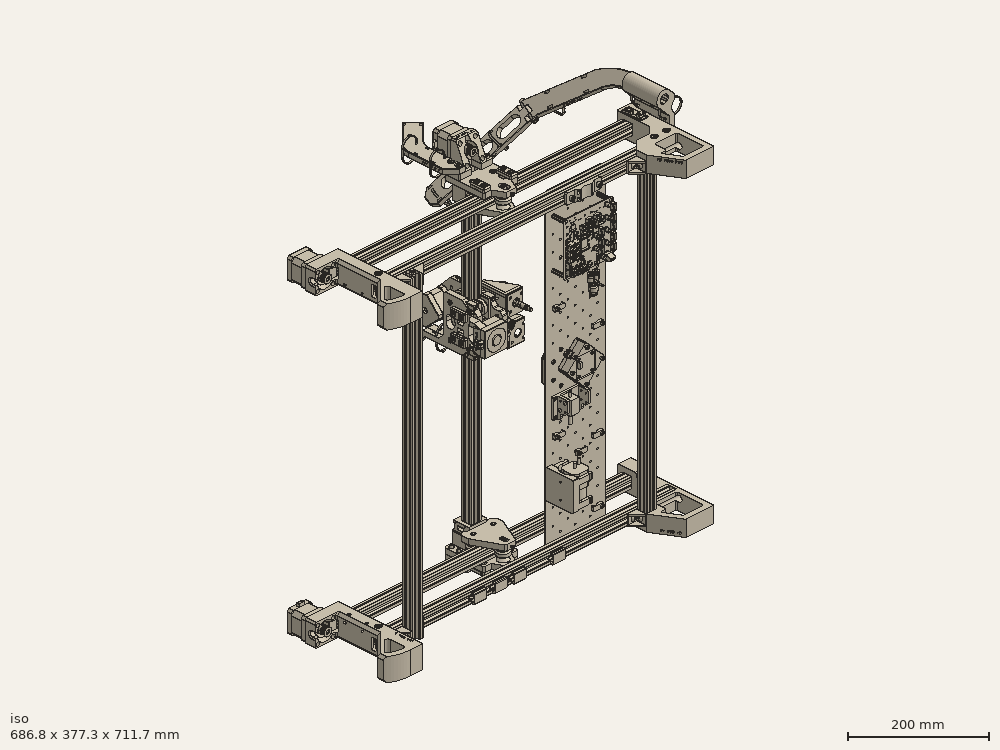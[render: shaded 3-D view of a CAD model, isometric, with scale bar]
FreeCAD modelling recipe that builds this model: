
FCSTD DOCUMENT  (FreeCAD 0.19R24291 (Git))
Label: assembly
Comment: LumenPnP
License: All rights reserved
LicenseURL: http://en.wikipedia.org/wiki/All_rights_reserved
objects: Part::FeaturePython×410, App::DocumentObjectGroup×16, Spreadsheet::Sheet×2
note: 410 computed .brp shape members not serialized (recipe doc carries the construction recipe); baked Part::Feature solids carry a one-line shape summary decoded from their .brp

FEATURE [Part::FeaturePython] b_MakerBot_LimitSwitchBoard1_001_001  label="MakerBot LimitSwitchBoard1_MakerBot LimitSwitchBoard_002"  # a2plus imported part (geometry in sourceFile) (typed FeaturePython)
  Placement = pos=(-192.209,155.993,-27.8326) rot=(0,0,-1;1.5708rad)
  Visibility1 = true
  a2p_Version = V0.1
  fixedPosition = false
  objectType = a2pPart
  sourceFile = ./OTS/OTS-0019_limit-switch-PCBA.STEP
  sourcePart = MakerBot LimitSwitchBoard
  subassemblyImport = false
  timeLastImport = 1.64563e+09
  updateColors = true
FEATURE [Part::FeaturePython] b_FDM_0005_y_gantry_001_  label="FDM-0005_y-gantry_Body_001"  # a2plus imported part (geometry in sourceFile) (typed FeaturePython)
  Placement = pos=(-209.128,133.935,11.9352) rot=(0,1,0;3.14159rad)
  Visibility1 = true
  a2p_Version = V0.1
  fixedPosition = false
  objectType = a2pPart
  sourceFile = ./FDM/FDM-0005_y-gantry.FCStd
  sourcePart = Body
  subassemblyImport = false
  timeLastImport = 1.64563e+09
  updateColors = true
FEATURE [Part::FeaturePython] b_OTS_0009_20x20_v_slot_600mm1_001_003  label="OTS-0009_20x20_v_slot_600mm1_20x20_v_slot_600mm v2_004"  # a2plus imported part (geometry in sourceFile) (typed FeaturePython)
  Placement = pos=(-219.183,133.936,0.0573608) rot=(0,0,1;0rad)
  Visibility1 = true
  a2p_Version = V0.1
  fixedPosition = false
  objectType = a2pPart
  sourceFile = ./OTS/OTS-0010_20x20-v-slot-600mm.step
  sourcePart = 20x20_v_slot_600mm v2
  subassemblyImport = false
  timeLastImport = 1.64563e+09
  updateColors = true
FEATURE [Part::FeaturePython] b_FDM_0005_y_gantry_001_001  label="FDM-0005_y-gantry_Body_002"  # a2plus imported part (geometry in sourceFile) (typed FeaturePython)
  Placement = pos=(-209.114,134.019,-612.218) rot=(0,0,1;0rad)
  Visibility1 = true
  a2p_Version = V0.1
  fixedPosition = false
  objectType = a2pPart
  sourceFile = ./FDM/FDM-0005_y-gantry.FCStd
  sourcePart = Body
  subassemblyImport = false
  timeLastImport = 1.64563e+09
  updateColors = true
FEATURE [Part::FeaturePython] b_FDM_0006_x_motor_mount_001_  label="FDM-0006_x-motor-mount_Body_001"  # a2plus imported part (geometry in sourceFile) (typed FeaturePython)
  Placement = pos=(-209.153,133.985,21.9455) rot=(0,1,0;3.14159rad)
  Visibility1 = true
  a2p_Version = V0.1
  fixedPosition = false
  objectType = a2pPart
  sourceFile = ./FDM/FDM-0006_x-motor-mount.FCStd
  sourcePart = Body
  subassemblyImport = false
  timeLastImport = 1.64668e+09
  updateColors = true
FEATURE [Part::FeaturePython] b_FDM_0013_x_idler_mount_001_  label="FDM-0013_x-idler-mount_Body_001"  # a2plus imported part (geometry in sourceFile) (typed FeaturePython)
  Placement = pos=(-209.106,124.037,-622.237) rot=(0,0,1;0rad)
  Visibility1 = true
  a2p_Version = V0.1
  fixedPosition = false
  objectType = a2pPart
  sourceFile = ./FDM/FDM-0013_x-idler-mount.FCStd
  sourcePart = Body
  subassemblyImport = false
  timeLastImport = 1.64563e+09
  updateColors = true
FEATURE [Part::FeaturePython] b_FDM_0010_y_gantry_umbilical_mount_001_  label="FDM-0010_y-gantry-umbilical-mount_Body_001"  # a2plus imported part (geometry in sourceFile) (typed FeaturePython)
  Placement = pos=(-260.596,133.978,22.038) rot=(0,0.707107,0.707107;3.14159rad)
  Visibility1 = true
  a2p_Version = V0.1
  fixedPosition = false
  objectType = a2pPart
  sourceFile = ./FDM/FDM-0010_y-gantry-umbilical-mount.FCStd
  sourcePart = Body
  subassemblyImport = false
  timeLastImport = 1.64563e+09
  updateColors = true
FEATURE [Part::FeaturePython] b_FDM_0008_y_gantry_support_001_  label="FDM-0008_y-gantry-support_Body_001"  # a2plus imported part (geometry in sourceFile) (typed FeaturePython)
  Placement = pos=(-209.134,74.2154,-32.0603) rot=(0,0,1;0rad)
  Visibility1 = true
  a2p_Version = V0.1
  fixedPosition = false
  objectType = a2pPart
  sourceFile = ./FDM/FDM-0008_y-gantry-support.FCStd
  sourcePart = Body
  subassemblyImport = false
  timeLastImport = 1.64563e+09
  updateColors = true
FEATURE [Part::FeaturePython] b_FDM_0008_y_gantry_support_001_001  label="FDM-0008_y-gantry-support_Body_002"  # a2plus imported part (geometry in sourceFile) (typed FeaturePython)
  Placement = pos=(-209.119,74.2225,-568.145) rot=(0,1,0;3.14159rad)
  Visibility1 = true
  a2p_Version = V0.1
  fixedPosition = false
  objectType = a2pPart
  sourceFile = ./FDM/FDM-0008_y-gantry-support.FCStd
  sourcePart = Body
  subassemblyImport = false
  timeLastImport = 1.64563e+09
  updateColors = true
FEATURE [Part::FeaturePython] b_FDM_0009_roller_spacer_001_  label="FDM-0009_roller-spacer_Body_001"  # a2plus imported part (geometry in sourceFile) (typed FeaturePython)
  Placement = pos=(-209.128,80.348,-22.0728) rot=(1,0,0;1.5708rad)
  Visibility1 = true
  a2p_Version = V0.1
  fixedPosition = false
  objectType = a2pPart
  sourceFile = ./FDM/FDM-0009_roller-spacer.FCStd
  sourcePart = Body
  subassemblyImport = false
  timeLastImport = 1.64563e+09
  updateColors = true
FEATURE [Part::FeaturePython] b_v_slot_roller1_001_  label="v-slot-roller1_Fusion_001"  # a2plus imported part (geometry in sourceFile) (typed FeaturePython)
  Placement = pos=(-213.864,116.699,-10.7746) rot=(-1,0,0;1.5708rad)
  Visibility1 = true
  a2p_Version = V0.1
  fixedPosition = false
  objectType = a2pPart
  sourceFile = ./OTS/OTS-0011_v-slot-roller.step
  sourcePart = Fusion
  subassemblyImport = false
  timeLastImport = 1.64563e+09
  updateColors = true
FEATURE [Part::FeaturePython] b_v_slot_roller1_001_001  label="v-slot-roller1_Fusion_002"  # a2plus imported part (geometry in sourceFile) (typed FeaturePython)
  Placement = pos=(-173.877,116.658,-10.7212) rot=(-1,0,0;1.5708rad)
  Visibility1 = true
  a2p_Version = V0.1
  fixedPosition = false
  objectType = a2pPart
  sourceFile = ./OTS/OTS-0011_v-slot-roller.step
  sourcePart = Fusion
  subassemblyImport = false
  timeLastImport = 1.64563e+09
  updateColors = true
FEATURE [Part::FeaturePython] b_FDM_0009_roller_spacer_001_001  label="FDM-0009_roller-spacer_Body_002"  # a2plus imported part (geometry in sourceFile) (typed FeaturePython)
  Placement = pos=(-209.167,80.3524,1.94462) rot=(-1,0,0;1.5708rad)
  Visibility1 = true
  a2p_Version = V0.1
  fixedPosition = false
  objectType = a2pPart
  sourceFile = ./FDM/FDM-0009_roller-spacer.FCStd
  sourcePart = Body
  subassemblyImport = false
  timeLastImport = 1.64563e+09
  updateColors = true
FEATURE [Part::FeaturePython] b_v_slot_roller1_001_002  label="v-slot-roller1_Fusion_003"  # a2plus imported part (geometry in sourceFile) (typed FeaturePython)
  Placement = pos=(-193.862,77.3523,-10.791) rot=(-1,0,0;1.5708rad)
  Visibility1 = true
  a2p_Version = V0.1
  fixedPosition = false
  objectType = a2pPart
  sourceFile = ./OTS/OTS-0011_v-slot-roller.step
  sourcePart = Fusion
  subassemblyImport = false
  timeLastImport = 1.64563e+09
  updateColors = true
FEATURE [Part::FeaturePython] Screw003  label="M5x40-Screw"  # Fasteners workbench fastener (typed FeaturePython)
  Placement = pos=(-189.16,119.74,6.95) rot=(0,0,1;0rad)
  Visibility1 = true
  diameter = 6
  invert = false
  length = 12
  lengthCustom = 40
  matchOuter = false
  offset = 0
  thread = false
  type = 33
FEATURE [Part::FeaturePython] Screw004  label="M5x40-Screw291"  # Fasteners workbench fastener (typed FeaturePython)
  Placement = pos=(-229.11,119.74,6.95) rot=(0,0,1;0rad)
  Visibility1 = true
  diameter = 6
  invert = false
  length = 12
  lengthCustom = 40
  matchOuter = false
  offset = 0
  thread = false
  type = 33
FEATURE [Part::FeaturePython] Screw005  label="M5x40-Screw292"  # Fasteners workbench fastener (typed FeaturePython)
  Placement = pos=(-209.15,80.34,6.95) rot=(0,0,1;0rad)
  Visibility1 = true
  diameter = 6
  invert = false
  length = 12
  lengthCustom = 40
  matchOuter = false
  offset = 0
  thread = false
  type = 33
FEATURE [Part::FeaturePython] Nut003  label="M5-Nut"  # Fasteners workbench fastener (typed FeaturePython)
  Placement = pos=(-229.05,119.689,-28.1459) rot=(-0.258819,0.965926,0;3.14159rad)
  Visibility1 = true
  diameter = 7
  invert = false
  matchOuter = false
  offset = 0
  thread = false
  type = 7
FEATURE [Part::FeaturePython] Nut004  label="M5-Nut208"  # Fasteners workbench fastener (typed FeaturePython)
  Placement = pos=(-189.008,119.713,-28.1459) rot=(-0.258819,0.965926,0;3.14159rad)
  Visibility1 = true
  diameter = 7
  invert = false
  matchOuter = false
  offset = 0
  thread = false
  type = 7
FEATURE [Part::FeaturePython] Nut005  label="M5-Nut209"  # Fasteners workbench fastener (typed FeaturePython)
  Placement = pos=(-209.108,80.3492,-28.1459) rot=(-0.258819,0.965926,0;3.14159rad)
  Visibility1 = true
  diameter = 7
  invert = false
  matchOuter = false
  offset = 0
  thread = false
  type = 7
FEATURE [Part::FeaturePython] Screw006  label="M3x16-Screw"  # Fasteners workbench fastener (typed FeaturePython)
  Placement = pos=(-209.15,61.89,-26.03) rot=(1,0,0;1.5708rad)
  Visibility1 = true
  diameter = 4
  invert = false
  length = 6
  lengthCustom = 16
  matchOuter = false
  offset = 0
  thread = false
  type = 33
FEATURE [Part::FeaturePython] Screw007  label="M3x16-Screw036"  # Fasteners workbench fastener (typed FeaturePython)
  Placement = pos=(-209.15,61.89,5.93) rot=(1,0,0;1.5708rad)
  Visibility1 = true
  diameter = 4
  invert = false
  length = 6
  lengthCustom = 16
  matchOuter = false
  offset = 0
  thread = false
  type = 33
FEATURE [Part::FeaturePython] Nut006  label="M3-Nut"  # Fasteners workbench fastener (typed FeaturePython)
  Placement = pos=(-209.156,68.38,5.75438) rot=(0.935113,-0.250563,0.250563;1.63783rad)
  Visibility1 = true
  diameter = 4
  invert = false
  matchOuter = false
  offset = 0
  thread = false
  type = 7
FEATURE [Part::FeaturePython] Nut007  label="M3-Nut178"  # Fasteners workbench fastener (typed FeaturePython)
  Placement = pos=(-209.069,68.45,-26.1349) rot=(0.935113,-0.250563,0.250563;1.63783rad)
  Visibility1 = true
  diameter = 4
  invert = false
  matchOuter = false
  offset = 0
  thread = false
  type = 7
FEATURE [Part::FeaturePython] Nut008  label="M5-Nut210"  # Fasteners workbench fastener (typed FeaturePython)
  Placement = pos=(-181.652,141.373,6.70406) rot=(-0.258819,0.965926,0;3.14159rad)
  Visibility1 = true
  diameter = 7
  invert = false
  matchOuter = false
  offset = 0
  thread = false
  type = 7
FEATURE [Part::FeaturePython] Nut009  label="M5-Nut211"  # Fasteners workbench fastener (typed FeaturePython)
  Placement = pos=(-181.604,156.47,6.70406) rot=(-0.258819,0.965926,0;3.14159rad)
  Visibility1 = true
  diameter = 7
  invert = false
  matchOuter = false
  offset = 0
  thread = false
  type = 7
FEATURE [Part::FeaturePython] Nut010  label="M5-Nut212"  # Fasteners workbench fastener (typed FeaturePython)
  Placement = pos=(-236.604,156.412,6.70406) rot=(-0.258819,0.965926,0;3.14159rad)
  Visibility1 = true
  diameter = 7
  invert = false
  matchOuter = false
  offset = 0
  thread = false
  type = 7
FEATURE [Part::FeaturePython] Nut011  label="M5-Nut213"  # Fasteners workbench fastener (typed FeaturePython)
  Placement = pos=(-236.631,141.42,6.70406) rot=(-0.258819,0.965926,0;3.14159rad)
  Visibility1 = true
  diameter = 7
  invert = false
  matchOuter = false
  offset = 0
  thread = false
  type = 7
FEATURE [Part::FeaturePython] Screw008  label="M5x25-Screw"  # Fasteners workbench fastener (typed FeaturePython)
  Placement = pos=(-236.29,141.5,27.32) rot=(0,0,1;0rad)
  Visibility1 = true
  diameter = 6
  invert = false
  length = 6
  lengthCustom = 25
  matchOuter = false
  offset = 0
  thread = false
  type = 33
FEATURE [Part::FeaturePython] Screw009  label="M5x25-Screw068"  # Fasteners workbench fastener (typed FeaturePython)
  Placement = pos=(-181.43,141.29,22.2) rot=(0,0,1;0rad)
  Visibility1 = true
  diameter = 6
  invert = false
  length = 6
  lengthCustom = 25
  matchOuter = false
  offset = 0
  thread = false
  type = 33
FEATURE [Part::FeaturePython] Screw010  label="M5x25-Screw069"  # Fasteners workbench fastener (typed FeaturePython)
  Placement = pos=(-181.43,156.5,22.2) rot=(0,0,1;0rad)
  Visibility1 = true
  diameter = 6
  invert = false
  length = 6
  lengthCustom = 25
  matchOuter = false
  offset = 0
  thread = false
  type = 33
FEATURE [Part::FeaturePython] Screw011  label="M5x25-Screw070"  # Fasteners workbench fastener (typed FeaturePython)
  Placement = pos=(-236.29,156.25,27.32) rot=(0,0,1;0rad)
  Visibility1 = true
  diameter = 6
  invert = false
  length = 6
  lengthCustom = 25
  matchOuter = false
  offset = 0
  thread = false
  type = 33
FEATURE [Part::FeaturePython] Screw012  label="M5x25-Screw071"  # Fasteners workbench fastener (typed FeaturePython)
  Placement = pos=(-181.5,156.55,-622.24) rot=(0,1,0;3.14159rad)
  Visibility1 = true
  diameter = 6
  invert = false
  length = 6
  lengthCustom = 25
  matchOuter = false
  offset = 0
  thread = false
  type = 33
FEATURE [Part::FeaturePython] Screw013  label="M5x25-Screw072"  # Fasteners workbench fastener (typed FeaturePython)
  Placement = pos=(-181.5,141.61,-622.18) rot=(0,1,0;3.14159rad)
  Visibility1 = true
  diameter = 6
  invert = false
  length = 6
  lengthCustom = 25
  matchOuter = false
  offset = 0
  thread = false
  type = 33
FEATURE [Part::FeaturePython] Screw014  label="M5x25-Screw073"  # Fasteners workbench fastener (typed FeaturePython)
  Placement = pos=(-236.54,141.56,-622.22) rot=(0,1,0;3.14159rad)
  Visibility1 = true
  diameter = 6
  invert = false
  length = 6
  lengthCustom = 25
  matchOuter = false
  offset = 0
  thread = false
  type = 33
FEATURE [Part::FeaturePython] Screw015  label="M5x25-Screw074"  # Fasteners workbench fastener (typed FeaturePython)
  Placement = pos=(-236.54,156.5,-622.24) rot=(0,1,0;3.14159rad)
  Visibility1 = true
  diameter = 6
  invert = false
  length = 6
  lengthCustom = 25
  matchOuter = false
  offset = 0
  thread = false
  type = 33
FEATURE [Part::FeaturePython] Nut012  label="M5-Nut214"  # Fasteners workbench fastener (typed FeaturePython)
  Placement = pos=(-236.619,141.519,-603.606) rot=(-0.258819,0.965926,0;3.14159rad)
  Visibility1 = true
  diameter = 7
  invert = false
  matchOuter = false
  offset = 0
  thread = false
  type = 7
FEATURE [Part::FeaturePython] Nut013  label="M5-Nut215"  # Fasteners workbench fastener (typed FeaturePython)
  Placement = pos=(-236.602,156.529,-603.536) rot=(-0.258819,0.965926,0;3.14159rad)
  Visibility1 = true
  diameter = 7
  invert = false
  matchOuter = false
  offset = 0
  thread = false
  type = 7
FEATURE [Part::FeaturePython] Nut014  label="M5-Nut216"  # Fasteners workbench fastener (typed FeaturePython)
  Placement = pos=(-181.656,156.52,-603.666) rot=(-0.258819,0.965926,0;3.14159rad)
  Visibility1 = true
  diameter = 7
  invert = false
  matchOuter = false
  offset = 0
  thread = false
  type = 7
FEATURE [Part::FeaturePython] Nut015  label="M5-Nut217"  # Fasteners workbench fastener (typed FeaturePython)
  Placement = pos=(-181.56,141.553,-603.646) rot=(-0.258819,0.965926,0;3.14159rad)
  Visibility1 = true
  diameter = 7
  invert = false
  matchOuter = false
  offset = 0
  thread = false
  type = 7
FEATURE [Part::FeaturePython] Screw016  label="M5x40-Screw293"  # Fasteners workbench fastener (typed FeaturePython)
  Placement = pos=(-189.09,119.82,-607.25) rot=(0,1,0;3.14159rad)
  Visibility1 = true
  diameter = 6
  invert = false
  length = 12
  lengthCustom = 40
  matchOuter = false
  offset = 0
  thread = false
  type = 33
FEATURE [Part::FeaturePython] b_v_slot_roller1_001_006  label="v-slot-roller1_Fusion_007"  # a2plus imported part (geometry in sourceFile) (typed FeaturePython)
  Placement = pos=(-186.117,135.005,-590.83) rot=(0.57735,0.57735,-0.57735;4.18879rad)
  Visibility1 = true
  a2p_Version = V0.1
  fixedPosition = false
  objectType = a2pPart
  sourceFile = ./OTS/OTS-0011_v-slot-roller.step
  sourcePart = Fusion
  subassemblyImport = false
  timeLastImport = 1.64563e+09
  updateColors = true
FEATURE [Part::FeaturePython] b_v_slot_roller1_001_007  label="v-slot-roller1_Fusion_008"  # a2plus imported part (geometry in sourceFile) (typed FeaturePython)
  Placement = pos=(-213.81,116.722,-590.853) rot=(-1,0,0;1.5708rad)
  Visibility1 = true
  a2p_Version = V0.1
  fixedPosition = false
  objectType = a2pPart
  sourceFile = ./OTS/OTS-0011_v-slot-roller.step
  sourcePart = Fusion
  subassemblyImport = false
  timeLastImport = 1.64563e+09
  updateColors = true
FEATURE [Part::FeaturePython] Screw017  label="M5x40-Screw294"  # Fasteners workbench fastener (typed FeaturePython)
  Placement = pos=(-229.1,119.82,-607.25) rot=(0,1,0;3.14159rad)
  Visibility1 = true
  diameter = 6
  invert = false
  length = 12
  lengthCustom = 40
  matchOuter = false
  offset = 0
  thread = false
  type = 33
FEATURE [Part::FeaturePython] Screw018  label="M5x40-Screw295"  # Fasteners workbench fastener (typed FeaturePython)
  Placement = pos=(-209.12,80.38,-607.25) rot=(0,1,0;3.14159rad)
  Visibility1 = true
  diameter = 6
  invert = false
  length = 12
  lengthCustom = 40
  matchOuter = false
  offset = 0
  thread = false
  type = 33
FEATURE [Part::FeaturePython] b_v_slot_roller1_001_008  label="v-slot-roller1_Fusion_009"  # a2plus imported part (geometry in sourceFile) (typed FeaturePython)
  Placement = pos=(-193.81,77.3723,-590.853) rot=(-1,0,0;1.5708rad)
  Visibility1 = true
  a2p_Version = V0.1
  fixedPosition = false
  objectType = a2pPart
  sourceFile = ./OTS/OTS-0011_v-slot-roller.step
  sourcePart = Fusion
  subassemblyImport = false
  timeLastImport = 1.64563e+09
  updateColors = true
FEATURE [Part::FeaturePython] Nut016  label="M5-Nut218"  # Fasteners workbench fastener (typed FeaturePython)
  Placement = pos=(-209.08,80.4002,-568.626) rot=(-0.258819,0.965926,0;3.14159rad)
  Visibility1 = true
  diameter = 7
  invert = false
  matchOuter = false
  offset = 0
  thread = false
  type = 7
FEATURE [Part::FeaturePython] Nut017  label="M5-Nut219"  # Fasteners workbench fastener (typed FeaturePython)
  Placement = pos=(-189.034,119.779,-568.626) rot=(-0.258819,0.965926,0;3.14159rad)
  Visibility1 = true
  diameter = 7
  invert = false
  matchOuter = false
  offset = 0
  thread = false
  type = 7
FEATURE [Part::FeaturePython] Nut018  label="M5-Nut220"  # Fasteners workbench fastener (typed FeaturePython)
  Placement = pos=(-229.099,119.753,-568.626) rot=(-0.258819,0.965926,0;3.14159rad)
  Visibility1 = true
  diameter = 7
  invert = false
  matchOuter = false
  offset = 0
  thread = false
  type = 7
FEATURE [Part::FeaturePython] Screw019  label="M3x16-Screw037"  # Fasteners workbench fastener (typed FeaturePython)
  Placement = pos=(-209.15,61.89,-574.13) rot=(1,0,0;1.5708rad)
  Visibility1 = true
  diameter = 4
  invert = false
  length = 6
  lengthCustom = 16
  matchOuter = false
  offset = 0
  thread = false
  type = 33
FEATURE [Part::FeaturePython] Screw020  label="M3x16-Screw043"  # Fasteners workbench fastener (typed FeaturePython)
  Placement = pos=(-209.12,61.89,-605.22) rot=(1,0,0;1.5708rad)
  Visibility1 = true
  diameter = 4
  invert = false
  length = 6
  lengthCustom = 16
  matchOuter = false
  offset = 0
  thread = false
  type = 33
FEATURE [Part::FeaturePython] Nut019  label="M3-Nut179"  # Fasteners workbench fastener (typed FeaturePython)
  Placement = pos=(-209.236,68.44,-574.367) rot=(0.935113,-0.250563,0.250563;1.63783rad)
  Visibility1 = true
  diameter = 4
  invert = false
  matchOuter = false
  offset = 0
  thread = false
  type = 7
FEATURE [Part::FeaturePython] Nut020  label="M3-Nut232"  # Fasteners workbench fastener (typed FeaturePython)
  Placement = pos=(-209.133,68.46,-605.236) rot=(0.57735,-0.57735,0.57735;2.0944rad)
  Visibility1 = true
  diameter = 4
  invert = false
  matchOuter = false
  offset = 0
  thread = false
  type = 7
FEATURE [Part::FeaturePython] b_FDM_0009_roller_spacer_001_002  label="FDM-0009_roller-spacer_Body_003"  # a2plus imported part (geometry in sourceFile) (typed FeaturePython)
  Placement = pos=(-209.167,80.3524,-578.105) rot=(-1,0,0;1.5708rad)
  Visibility1 = true
  a2p_Version = V0.1
  fixedPosition = false
  objectType = a2pPart
  sourceFile = ./FDM/FDM-0009_roller-spacer.FCStd
  sourcePart = Body
  subassemblyImport = false
  timeLastImport = 1.64563e+09
  updateColors = true
FEATURE [Part::FeaturePython] b_FDM_0009_roller_spacer_001_003  label="FDM-0009_roller-spacer_Body_004"  # a2plus imported part (geometry in sourceFile) (typed FeaturePython)
  Placement = pos=(-209.167,80.3524,-602.155) rot=(0,0.707107,0.707107;3.14159rad)
  Visibility1 = true
  a2p_Version = V0.1
  fixedPosition = false
  objectType = a2pPart
  sourceFile = ./FDM/FDM-0009_roller-spacer.FCStd
  sourcePart = Body
  subassemblyImport = false
  timeLastImport = 1.64563e+09
  updateColors = true
FEATURE [Part::FeaturePython] Screw021  label="M5x40-Screw289"  # Fasteners workbench fastener (typed FeaturePython)
  Placement = pos=(-194.1,163.97,-634.23) rot=(0,0.707107,0.707107;3.14159rad)
  Visibility1 = true
  diameter = 6
  invert = false
  length = 12
  lengthCustom = 40
  matchOuter = false
  offset = 0
  thread = false
  type = 33
FEATURE [Part::FeaturePython] Screw022  label="M5x10-Screw"  # Fasteners workbench fastener (typed FeaturePython)
  Placement = pos=(-209.22,158.94,-18.1) rot=(-1,0,0;1.5708rad)
  Visibility1 = true
  diameter = 6
  invert = false
  length = 1
  lengthCustom = 10
  matchOuter = false
  offset = 0
  thread = false
  type = 33
FEATURE [Part::FeaturePython] b_M5_tslot_nut1_001_  label="M5-tslot-nut1_T_Slot_Nut_Dropin_M5 v1_001"  # a2plus imported part (geometry in sourceFile) (typed FeaturePython)
  Placement = pos=(-209.412,148.905,-18.0282) rot=(0.57735,-0.57735,-0.57735;4.18879rad)
  Visibility1 = true
  a2p_Version = V0.1
  fixedPosition = false
  objectType = a2pPart
  sourceFile = ./FST/FST-0016_M5-tslot-nut.step
  sourcePart = T_Slot_Nut_Dropin_M5 v1
  subassemblyImport = false
  timeLastImport = 1.64563e+09
  updateColors = true
FEATURE [Part::FeaturePython] b_M5_tslot_nut1_001_001  label="M5-tslot-nut1_T_Slot_Nut_Dropin_M5 v1_002"  # a2plus imported part (geometry in sourceFile) (typed FeaturePython)
  Placement = pos=(-209.412,148.905,-582.128) rot=(0.57735,-0.57735,-0.57735;4.18879rad)
  Visibility1 = true
  a2p_Version = V0.1
  fixedPosition = false
  objectType = a2pPart
  sourceFile = ./FST/FST-0016_M5-tslot-nut.step
  sourcePart = T_Slot_Nut_Dropin_M5 v1
  subassemblyImport = false
  timeLastImport = 1.64563e+09
  updateColors = true
FEATURE [Part::FeaturePython] Screw023  label="M5x10-Screw187"  # Fasteners workbench fastener (typed FeaturePython)
  Placement = pos=(-209.22,158.94,-582.17) rot=(-1,0,0;1.5708rad)
  Visibility1 = true
  diameter = 6
  invert = false
  length = 1
  lengthCustom = 10
  matchOuter = false
  offset = 0
  thread = false
  type = 33
FEATURE [Part::FeaturePython] Screw025  label="M5x10-Screw188"  # Fasteners workbench fastener (typed FeaturePython)
  Placement = pos=(-236.1,91.45,15.24) rot=(0,0,1;0rad)
  Visibility1 = true
  diameter = 6
  invert = false
  length = 1
  lengthCustom = 10
  matchOuter = false
  offset = 0
  thread = false
  type = 33
FEATURE [Part::FeaturePython] b_FDM_0027_belt_clamp_001_  label="FDM-0027_belt-clamp_Body_001"  # a2plus imported part (geometry in sourceFile) (typed FeaturePython)
  Placement = pos=(-236.126,98.9408,12.0481) rot=(0,0,1;0rad)
  Visibility1 = true
  a2p_Version = V0.1
  fixedPosition = false
  objectType = a2pPart
  sourceFile = ./FDM/FDM-0027_belt-clamp.FCStd
  sourcePart = Body
  subassemblyImport = false
  timeLastImport = 1.64563e+09
  updateColors = true
FEATURE [Part::FeaturePython] Screw026  label="M5x10-Screw189"  # Fasteners workbench fastener (typed FeaturePython)
  Placement = pos=(-236.1,106.47,15.24) rot=(0,0,1;0rad)
  Visibility1 = true
  diameter = 6
  invert = false
  length = 1
  lengthCustom = 10
  matchOuter = false
  offset = 0
  thread = false
  type = 33
FEATURE [Part::FeaturePython] Screw027  label="M5x10-Screw190"  # Fasteners workbench fastener (typed FeaturePython)
  Placement = pos=(-182.19,106.47,15.24) rot=(0,0,1;0rad)
  Visibility1 = true
  diameter = 6
  invert = false
  length = 1
  lengthCustom = 10
  matchOuter = false
  offset = 0
  thread = false
  type = 33
FEATURE [Part::FeaturePython] Screw028  label="M5x10-Screw191"  # Fasteners workbench fastener (typed FeaturePython)
  Placement = pos=(-182.19,91.5,15.24) rot=(0,0,1;0rad)
  Visibility1 = true
  diameter = 6
  invert = false
  length = 1
  lengthCustom = 10
  matchOuter = false
  offset = 0
  thread = false
  type = 33
FEATURE [Part::FeaturePython] b_FDM_0027_belt_clamp_001_001  label="FDM-0027_belt-clamp_Body_002"  # a2plus imported part (geometry in sourceFile) (typed FeaturePython)
  Placement = pos=(-182.176,98.9408,12.0481) rot=(0,0,1;0rad)
  Visibility1 = true
  a2p_Version = V0.1
  fixedPosition = false
  objectType = a2pPart
  sourceFile = ./FDM/FDM-0027_belt-clamp.FCStd
  sourcePart = Body
  subassemblyImport = false
  timeLastImport = 1.64563e+09
  updateColors = true
FEATURE [Part::FeaturePython] Screw121  label="M3x8-Screw"  # Fasteners workbench fastener (typed FeaturePython)
  Placement = pos=(-190.65,158.35,-32.97) rot=(0,1,0;1.5708rad)
  Visibility1 = true
  diameter = 1
  invert = false
  length = 1
  lengthCustom = 8
  matchOuter = false
  offset = 0
  thread = false
  type = 39
FEATURE [Part::FeaturePython] Screw122  label="M3x8-Screw273"  # Fasteners workbench fastener (typed FeaturePython)
  Placement = pos=(-190.65,139.49,-33.02) rot=(0,1,0;1.5708rad)
  Visibility1 = true
  diameter = 1
  invert = false
  length = 1
  lengthCustom = 8
  matchOuter = false
  offset = 0
  thread = false
  type = 39
FEATURE [Part::FeaturePython] Screw099  label="M3x8-Screw278"  # Fasteners workbench fastener (typed FeaturePython)
  Placement = pos=(-224.63,158.88,58.97) rot=(0.57735,0.57735,-0.57735;2.0944rad)
  Visibility1 = true
  diameter = 1
  invert = false
  length = 1
  lengthCustom = 8
  matchOuter = false
  offset = 0
  thread = false
  type = 39
FEATURE [Part::FeaturePython] Screw097  label="M3x8-Screw279"  # Fasteners workbench fastener (typed FeaturePython)
  Placement = pos=(-224.63,158.88,27.96) rot=(0.57735,0.57735,-0.57735;2.0944rad)
  Visibility1 = true
  diameter = 1
  invert = false
  length = 1
  lengthCustom = 8
  matchOuter = false
  offset = 0
  thread = false
  type = 39
FEATURE [Part::FeaturePython] Screw100  label="M3x8-Screw280"  # Fasteners workbench fastener (typed FeaturePython)
  Placement = pos=(-193.61,158.88,58.97) rot=(0.57735,0.57735,-0.57735;2.0944rad)
  Visibility1 = true
  diameter = 1
  invert = false
  length = 1
  lengthCustom = 8
  matchOuter = false
  offset = 0
  thread = false
  type = 39
FEATURE [Part::FeaturePython] Screw098  label="M3x8-Screw281"  # Fasteners workbench fastener (typed FeaturePython)
  Placement = pos=(-193.61,158.88,27.96) rot=(0.57735,0.57735,-0.57735;2.0944rad)
  Visibility1 = true
  diameter = 1
  invert = false
  length = 1
  lengthCustom = 8
  matchOuter = false
  offset = 0
  thread = false
  type = 39
FEATURE [Part::FeaturePython] Screw059  label="M5x25-Screw075"  # Fasteners workbench fastener (typed FeaturePython)
  Placement = pos=(-209.27,154.08,-634.17) rot=(0,0.707107,0.707107;3.14159rad)
  Visibility1 = true
  diameter = 6
  invert = false
  length = 6
  lengthCustom = 25
  matchOuter = false
  offset = 0
  thread = false
  type = 33
FEATURE [Part::FeaturePython] b_front_leg_tensioner_001_001  label="front-leg-tensioner_Body_002"  # a2plus imported part (geometry in sourceFile) (typed FeaturePython)
  Placement = pos=(-189.226,134.067,-629.163) rot=(0,1,0;3.14159rad)
  Visibility1 = true
  a2p_Version = V0.1
  fixedPosition = false
  objectType = a2pPart
  sourceFile = ./FDM/FDM-0037_belt-tension-arm.FCStd
  sourcePart = Body
  subassemblyImport = false
  timeLastImport = 1.64563e+09
  updateColors = true
FEATURE [Part::FeaturePython] Screw060  label="M3x16-Screw039"  # Fasteners workbench fastener (typed FeaturePython)
  Placement = pos=(-224.21,144.08,-638.25) rot=(1,0,0;3.14159rad)
  Visibility1 = true
  diameter = 4
  invert = false
  length = 6
  lengthCustom = 16
  matchOuter = false
  offset = 0
  thread = false
  type = 33
FEATURE [Part::FeaturePython] Screw058  label="M5x10-Screw192"  # Fasteners workbench fastener (typed FeaturePython)
  Placement = pos=(-236.11,106.53,-615.37) rot=(0,1,0;3.14159rad)
  Visibility1 = true
  diameter = 6
  invert = false
  length = 1
  lengthCustom = 10
  matchOuter = false
  offset = 0
  thread = false
  type = 33
FEATURE [Part::FeaturePython] Screw057  label="M5x10-Screw193"  # Fasteners workbench fastener (typed FeaturePython)
  Placement = pos=(-236.11,91.54,-615.37) rot=(0,1,0;3.14159rad)
  Visibility1 = true
  diameter = 6
  invert = false
  length = 1
  lengthCustom = 10
  matchOuter = false
  offset = 0
  thread = false
  type = 33
FEATURE [Part::FeaturePython] Screw056  label="M5x10-Screw194"  # Fasteners workbench fastener (typed FeaturePython)
  Placement = pos=(-182.19,91.54,-615.37) rot=(0,1,0;3.14159rad)
  Visibility1 = true
  diameter = 6
  invert = false
  length = 1
  lengthCustom = 10
  matchOuter = false
  offset = 0
  thread = false
  type = 33
FEATURE [Part::FeaturePython] b_FDM_0027_belt_clamp_001_005  label="FDM-0027_belt-clamp_Body_006"  # a2plus imported part (geometry in sourceFile) (typed FeaturePython)
  Placement = pos=(-182.156,98.9408,-612.402) rot=(0,1,0;3.14159rad)
  Visibility1 = true
  a2p_Version = V0.1
  fixedPosition = false
  objectType = a2pPart
  sourceFile = ./FDM/FDM-0027_belt-clamp.FCStd
  sourcePart = Body
  subassemblyImport = false
  timeLastImport = 1.64563e+09
  updateColors = true
FEATURE [Part::FeaturePython] b_FDM_0027_belt_clamp_001_004  label="FDM-0027_belt-clamp_Body_005"  # a2plus imported part (geometry in sourceFile) (typed FeaturePython)
  Placement = pos=(-236.126,99.0108,-612.402) rot=(0,1,0;3.14159rad)
  Visibility1 = true
  a2p_Version = V0.1
  fixedPosition = false
  objectType = a2pPart
  sourceFile = ./FDM/FDM-0027_belt-clamp.FCStd
  sourcePart = Body
  subassemblyImport = false
  timeLastImport = 1.64563e+09
  updateColors = true
FEATURE [Part::FeaturePython] b_Nema_17_42A02C_v21_001_001  label="Nema 17 42A02C v21_ Nema 17 42A02C v2_002"  # a2plus imported part (geometry in sourceFile) (typed FeaturePython)
  Placement = pos=(-209.138,153.958,43.4338) rot=(0.57735,0.57735,-0.57735;2.0944rad)
  Visibility1 = true
  a2p_Version = V0.1
  fixedPosition = false
  objectType = a2pPart
  sourceFile = ./OTS/OTS-0012_nema17-stepper.step
  sourcePart =  Nema 17 42A02C v2
  subassemblyImport = false
  timeLastImport = 1.64563e+09
  updateColors = true
FEATURE [Part::FeaturePython] Nut043  label="M5-Nut472"  # Fasteners workbench fastener (typed FeaturePython)
  Placement = pos=(-209.269,134.219,-634.166) rot=(1,0,0;1.5708rad)
  Visibility1 = true
  diameter = 3
  invert = false
  matchOuter = false
  offset = 0
  thread = false
  type = 5
FEATURE [Part::FeaturePython] Nut042  label="M5-Nut471"  # Fasteners workbench fastener (typed FeaturePython)
  Placement = pos=(-194.15,128.957,-634.224) rot=(-0.186157,-0.694747,0.694747;3.50969rad)
  Visibility1 = true
  diameter = 3
  invert = false
  matchOuter = false
  offset = 0
  thread = false
  type = 5
FEATURE [Part::FeaturePython] b_Gates_2GT_20T_Toothed_Pulley1_001_001  label="Gates_2GT_20T_Toothed_Pulley1_Gates_2GT_20T_Toothed_Pulley_002"  # a2plus imported part (geometry in sourceFile) (typed FeaturePython)
  Placement = pos=(-209.139,155.221,43.4196) rot=(0,0,1;3.14159rad)
  Visibility1 = true
  a2p_Version = V0.1
  fixedPosition = false
  objectType = a2pPart
  sourceFile = ./OTS/OTS-0017_GT2-20-tooth-pulley.STEP
  sourcePart = Gates_2GT_20T_Toothed_Pulley
  subassemblyImport = false
  timeLastImport = 1.64563e+09
  updateColors = true
FEATURE [Part::FeaturePython] b_Gates_2GT_20T_Toothed_Idler1_001_002  label="Gates_2GT_20T_Toothed_Idler1_Gates_2GT_20T_Toothed_Idler_003"  # a2plus imported part (geometry in sourceFile) (typed FeaturePython)
  Placement = pos=(-209.286,138.99,-634.179) rot=(0,0,1;0rad)
  Visibility1 = true
  a2p_Version = V0.1
  fixedPosition = false
  objectType = a2pPart
  sourceFile = ./OTS/OTS-0016_GT2-20-tooth-idler.STEP
  sourcePart = Gates_2GT_20T_Toothed_Idler
  subassemblyImport = false
  timeLastImport = 1.64563e+09
  updateColors = true
FEATURE [Part::FeaturePython] Screw055  label="M5x10-Screw195"  # Fasteners workbench fastener (typed FeaturePython)
  Placement = pos=(-182.19,106.47,-615.37) rot=(0,1,0;3.14159rad)
  Visibility1 = true
  diameter = 6
  invert = false
  length = 1
  lengthCustom = 10
  matchOuter = false
  offset = 0
  thread = false
  type = 33
FEATURE [Part::FeaturePython] Nut037  label="M5-Nut223"  # Fasteners workbench fastener (typed FeaturePython)
  Placement = pos=(-182.185,91.4364,8.89406) rot=(-0.258819,0.965926,0;3.14159rad)
  Visibility1 = true
  diameter = 7
  invert = false
  matchOuter = false
  offset = 0
  thread = false
  type = 7
FEATURE [Part::FeaturePython] Nut035  label="M5-Nut224"  # Fasteners workbench fastener (typed FeaturePython)
  Placement = pos=(-236.086,106.516,8.89406) rot=(-0.258819,0.965926,0;3.14159rad)
  Visibility1 = true
  diameter = 7
  invert = false
  matchOuter = false
  offset = 0
  thread = false
  type = 7
FEATURE [Part::FeaturePython] Nut041  label="M5-Nut225"  # Fasteners workbench fastener (typed FeaturePython)
  Placement = pos=(-236.093,106.547,-605.676) rot=(-0.258819,0.965926,0;3.14159rad)
  Visibility1 = true
  diameter = 7
  invert = false
  matchOuter = false
  offset = 0
  thread = false
  type = 7
FEATURE [Part::FeaturePython] Nut040  label="M5-Nut226"  # Fasteners workbench fastener (typed FeaturePython)
  Placement = pos=(-236.072,91.571,-605.676) rot=(-0.258819,0.965926,0;3.14159rad)
  Visibility1 = true
  diameter = 7
  invert = false
  matchOuter = false
  offset = 0
  thread = false
  type = 7
FEATURE [Part::FeaturePython] Nut036  label="M5-Nut227"  # Fasteners workbench fastener (typed FeaturePython)
  Placement = pos=(-182.149,106.434,8.89406) rot=(-0.258819,0.965926,0;3.14159rad)
  Visibility1 = true
  diameter = 7
  invert = false
  matchOuter = false
  offset = 0
  thread = false
  type = 7
FEATURE [Part::FeaturePython] Nut034  label="M5-Nut228"  # Fasteners workbench fastener (typed FeaturePython)
  Placement = pos=(-236.073,91.5127,8.89406) rot=(-0.258819,0.965926,0;3.14159rad)
  Visibility1 = true
  diameter = 7
  invert = false
  matchOuter = false
  offset = 0
  thread = false
  type = 7
FEATURE [Part::FeaturePython] Nut039  label="M5-Nut229"  # Fasteners workbench fastener (typed FeaturePython)
  Placement = pos=(-182.149,106.514,-605.676) rot=(-0.258819,0.965926,0;3.14159rad)
  Visibility1 = true
  diameter = 7
  invert = false
  matchOuter = false
  offset = 0
  thread = false
  type = 7
FEATURE [Part::FeaturePython] Nut038  label="M5-Nut230"  # Fasteners workbench fastener (typed FeaturePython)
  Placement = pos=(-182.168,91.527,-605.676) rot=(-0.258819,0.965926,0;3.14159rad)
  Visibility1 = true
  diameter = 7
  invert = false
  matchOuter = false
  offset = 0
  thread = false
  type = 7
FEATURE [Part::FeaturePython] Nut044  label="M3-Nut181"  # Fasteners workbench fastener (typed FeaturePython)
  Placement = pos=(-224.209,144.071,-632.154) rot=(0,0,1;0.523599rad)
  Visibility1 = true
  diameter = 4
  invert = false
  matchOuter = false
  offset = 0
  thread = false
  type = 7
FEATURE [Part::FeaturePython] b_OTS_0005_00_zip_tie_001_004  label="OTS-0005-00_zip-tie_Body_005"  # a2plus imported part (geometry in sourceFile) (typed FeaturePython)
  Placement = pos=(-250.941,228.177,50.7715) rot=(1,0,0;1.5708rad)
  a2p_Version = V0.1
  fixedPosition = false
  objectType = a2pPart
  sourceFile = ./OTS/OTS-0005-00_zip-tie.FCStd
  sourcePart = Body
  subassemblyImport = false
  timeLastImport = 1.64563e+09
  updateColors = true
FEATURE [Part::FeaturePython] b_OTS_0005_00_zip_tie_001_005  label="OTS-0005-00_zip-tie_Body_006"  # a2plus imported part (geometry in sourceFile) (typed FeaturePython)
  Placement = pos=(-250.941,172.877,50.7715) rot=(1,0,0;1.5708rad)
  a2p_Version = V0.1
  fixedPosition = false
  objectType = a2pPart
  sourceFile = ./OTS/OTS-0005-00_zip-tie.FCStd
  sourcePart = Body
  subassemblyImport = false
  timeLastImport = 1.64563e+09
  updateColors = true
FEATURE [Part::FeaturePython] b_MakerBot_LimitSwitchBoard1_001_002  label="MakerBot LimitSwitchBoard1_MakerBot LimitSwitchBoard_003"  # a2plus imported part (geometry in sourceFile) (typed FeaturePython)
  Placement = pos=(-187.439,201.553,-280.333) rot=(0.57735,0.57735,0.57735;4.18879rad)
  Visibility1 = true
  a2p_Version = V0.1
  fixedPosition = false
  objectType = a2pPart
  sourceFile = ./OTS/OTS-0019_limit-switch-PCBA.STEP
  sourcePart = MakerBot LimitSwitchBoard
  subassemblyImport = false
  timeLastImport = 1.64563e+09
  updateColors = true
FEATURE [Part::FeaturePython] b_OTS_0002_00_usb_webcam_001_  label="OTS-0002-00_usb-webcam_Body_001"  # a2plus imported part (geometry in sourceFile) (typed FeaturePython)
  Placement = pos=(-221.423,101.39,-237.284) rot=(0.57735,0.57735,-0.57735;2.0944rad)
  Visibility1 = true
  a2p_Version = V0.1
  fixedPosition = false
  objectType = a2pPart
  sourceFile = ./OTS/OTS-0002-00_usb-webcam.FCStd
  sourcePart = Body
  subassemblyImport = false
  timeLastImport = 1.64563e+09
  updateColors = true
FEATURE [Part::FeaturePython] b_FDM_0011_x_gantry_front_001_  label="FDM-0011_x-gantry-front_Body_001"  # a2plus imported part (geometry in sourceFile) (typed FeaturePython)
  Placement = pos=(-197.353,123.214,-236.743) rot=(0,1,0;1.5708rad)
  Visibility1 = true
  a2p_Version = V0.1
  fixedPosition = false
  objectType = a2pPart
  sourceFile = ./FDM/FDM-0011_x-gantry-front.FCStd
  sourcePart = Body
  subassemblyImport = false
  timeLastImport = 1.64668e+09
  updateColors = true
FEATURE [Part::FeaturePython] b_FDM_0012_x_gantry_back_001_  label="FDM-0012_x-gantry-back_Body_001"  # a2plus imported part (geometry in sourceFile) (typed FeaturePython)
  Placement = pos=(-231.252,123.314,-236.82) rot=(0,1,0;1.5708rad)
  Visibility1 = true
  a2p_Version = V0.1
  fixedPosition = true
  objectType = a2pPart
  sourceFile = ./FDM/FDM-0012_x-gantry-back.FCStd
  sourcePart = Body
  subassemblyImport = false
  timeLastImport = 1.64563e+09
  updateColors = true
FEATURE [Part::FeaturePython] b_FDM_0014_down_camera_mount_001_  label="FDM-0014_down-camera-mount_Body_001"  # a2plus imported part (geometry in sourceFile) (typed FeaturePython)
  Placement = pos=(-221.392,104.569,-237.094) rot=(0.57735,0.57735,0.57735;4.18879rad)
  Visibility1 = true
  a2p_Version = V0.1
  fixedPosition = false
  objectType = a2pPart
  sourceFile = ./FDM/FDM-0014_down-camera-mount.FCStd
  sourcePart = Body
  subassemblyImport = false
  timeLastImport = 1.64563e+09
  updateColors = true
FEATURE [Part::FeaturePython] b_FDM_0015_down_light_mount_001_  label="FDM-0015_down-light-mount_Body_001"  # a2plus imported part (geometry in sourceFile) (typed FeaturePython)
  Placement = pos=(-221.445,81.0718,-237.05) rot=(0.57735,-0.57735,-0.57735;4.18879rad)
  Visibility1 = true
  a2p_Version = V0.1
  fixedPosition = false
  objectType = a2pPart
  sourceFile = ./FDM/FDM-0015_down-light-mount.FCStd
  sourcePart = Body
  subassemblyImport = false
  timeLastImport = 1.64677e+09
  updateColors = true
FEATURE [Part::FeaturePython] b_v_slot_roller1_001_003  label="v-slot-roller1_Fusion_004"  # a2plus imported part (geometry in sourceFile) (typed FeaturePython)
  Placement = pos=(-209.423,180.083,-208.819) rot=(0,0,1;1.5708rad)
  Visibility1 = true
  a2p_Version = V0.1
  fixedPosition = false
  objectType = a2pPart
  sourceFile = ./OTS/OTS-0011_v-slot-roller.step
  sourcePart = Fusion
  subassemblyImport = false
  timeLastImport = 1.64563e+09
  updateColors = true
FEATURE [Part::FeaturePython] b_v_slot_roller1_001_004  label="v-slot-roller1_Fusion_005"  # a2plus imported part (geometry in sourceFile) (typed FeaturePython)
  Placement = pos=(-209.423,180.083,-270.819) rot=(0,0,1;1.5708rad)
  Visibility1 = true
  a2p_Version = V0.1
  fixedPosition = false
  objectType = a2pPart
  sourceFile = ./OTS/OTS-0011_v-slot-roller.step
  sourcePart = Fusion
  subassemblyImport = false
  timeLastImport = 1.64563e+09
  updateColors = true
FEATURE [Part::FeaturePython] b_FDM_0027_belt_clamp_001_002  label="FDM-0027_belt-clamp_Body_003"  # a2plus imported part (geometry in sourceFile) (typed FeaturePython)
  Placement = pos=(-231.252,143.964,-215.82) rot=(-0.707107,0,0.707107;3.14159rad)
  Visibility1 = true
  a2p_Version = V0.1
  fixedPosition = false
  objectType = a2pPart
  sourceFile = ./FDM/FDM-0027_belt-clamp.FCStd
  sourcePart = Body
  subassemblyImport = false
  timeLastImport = 1.64563e+09
  updateColors = true
FEATURE [Part::FeaturePython] Nut021  label="M5-Nut476"  # Fasteners workbench fastener (typed FeaturePython)
  Placement = pos=(-225.2,151.517,-257.836) rot=(0.250563,-0.935113,-0.250563;1.63783rad)
  Visibility1 = true
  diameter = 7
  invert = false
  matchOuter = false
  offset = 0
  thread = false
  type = 7
FEATURE [Part::FeaturePython] Nut022  label="M5-Nut475"  # Fasteners workbench fastener (typed FeaturePython)
  Placement = pos=(-225.2,136.591,-257.776) rot=(0.250563,-0.935113,-0.250563;1.63783rad)
  Visibility1 = true
  diameter = 7
  invert = false
  matchOuter = false
  offset = 0
  thread = false
  type = 7
FEATURE [Part::FeaturePython] Screw038  label="M5x10-Screw222"  # Fasteners workbench fastener (typed FeaturePython)
  Placement = pos=(-234.23,136.48,-257.84) rot=(0.57735,0.57735,-0.57735;4.18879rad)
  Visibility1 = true
  diameter = 6
  invert = false
  length = 1
  lengthCustom = 10
  matchOuter = false
  offset = 0
  thread = false
  type = 33
FEATURE [Part::FeaturePython] Screw039  label="M5x10-Screw223"  # Fasteners workbench fastener (typed FeaturePython)
  Placement = pos=(-234.23,151.54,-257.74) rot=(0.57735,0.57735,-0.57735;4.18879rad)
  Visibility1 = true
  diameter = 6
  invert = false
  length = 1
  lengthCustom = 10
  matchOuter = false
  offset = 0
  thread = false
  type = 33
FEATURE [Part::FeaturePython] Nut023  label="M5-Nut473"  # Fasteners workbench fastener (typed FeaturePython)
  Placement = pos=(-225.2,136.517,-215.834) rot=(0.250563,-0.935113,-0.250563;1.63783rad)
  Visibility1 = true
  diameter = 7
  invert = false
  matchOuter = false
  offset = 0
  thread = false
  type = 7
FEATURE [Part::FeaturePython] Nut024  label="M5-Nut474"  # Fasteners workbench fastener (typed FeaturePython)
  Placement = pos=(-225.2,151.519,-215.794) rot=(0.250563,-0.935113,-0.250563;1.63783rad)
  Visibility1 = true
  diameter = 7
  invert = false
  matchOuter = false
  offset = 0
  thread = false
  type = 7
FEATURE [Part::FeaturePython] Screw040  label="M5x10-Screw225"  # Fasteners workbench fastener (typed FeaturePython)
  Placement = pos=(-234.23,151.54,-215.86) rot=(0.57735,0.57735,-0.57735;4.18879rad)
  Visibility1 = true
  diameter = 6
  invert = false
  length = 1
  lengthCustom = 10
  matchOuter = false
  offset = 0
  thread = false
  type = 33
FEATURE [Part::FeaturePython] b_FDM_0027_belt_clamp_001_003  label="FDM-0027_belt-clamp_Body_004"  # a2plus imported part (geometry in sourceFile) (typed FeaturePython)
  Placement = pos=(-231.252,144.064,-257.82) rot=(0,-1,0;1.5708rad)
  Visibility1 = true
  a2p_Version = V0.1
  fixedPosition = false
  objectType = a2pPart
  sourceFile = ./FDM/FDM-0027_belt-clamp.FCStd
  sourcePart = Body
  subassemblyImport = false
  timeLastImport = 1.64563e+09
  updateColors = true
FEATURE [Part::FeaturePython] Screw123  label="M3x8-Screw242"  # Fasteners workbench fastener (typed FeaturePython)
  Placement = pos=(-185.17,196.26,-282.62) rot=(0,1,0;1.5708rad)
  Visibility1 = true
  diameter = 1
  invert = false
  length = 1
  lengthCustom = 8
  matchOuter = false
  offset = 0
  thread = false
  type = 39
FEATURE [Part::FeaturePython] Screw124  label="M3x8-Screw248"  # Fasteners workbench fastener (typed FeaturePython)
  Placement = pos=(-185.17,196.26,-263.78) rot=(0,1,0;1.5708rad)
  Visibility1 = true
  diameter = 1
  invert = false
  length = 1
  lengthCustom = 8
  matchOuter = false
  offset = 0
  thread = false
  type = 39
FEATURE [Part::FeaturePython] b_Nema_17_42A02C_v21_001_  label="Nema 17 42A02C v21_ Nema 17 42A02C v2_001"  # a2plus imported part (geometry in sourceFile) (typed FeaturePython)
  Placement = pos=(-187.252,212.248,-236.776) rot=(0.681153,0.268444,0.681153;2.61707rad)
  Visibility1 = true
  a2p_Version = V0.1
  fixedPosition = false
  objectType = a2pPart
  sourceFile = ./OTS/OTS-0012_nema17-stepper.step
  sourcePart =  Nema 17 42A02C v2
  subassemblyImport = false
  timeLastImport = 1.64563e+09
  updateColors = true
FEATURE [Part::FeaturePython] b_Gates_2GT_20T_Toothed_Idler1_001_  label="Gates_2GT_20T_Toothed_Idler1_Gates_2GT_20T_Toothed_Idler_001"  # a2plus imported part (geometry in sourceFile) (typed FeaturePython)
  Placement = pos=(-185,99.0503,-236.78) rot=(0,0,-1;1.5708rad)
  Visibility1 = true
  a2p_Version = V0.1
  fixedPosition = false
  objectType = a2pPart
  sourceFile = ./OTS/OTS-0016_GT2-20-tooth-idler.STEP
  sourcePart = Gates_2GT_20T_Toothed_Idler
  subassemblyImport = false
  timeLastImport = 1.64563e+09
  updateColors = true
FEATURE [Part::FeaturePython] Screw045  label="M3x14-Screw"  # Fasteners workbench fastener (typed FeaturePython)
  Placement = pos=(-183.29,183.99,-216.76) rot=(0,1,0;1.5708rad)
  Visibility1 = true
  diameter = 1
  invert = false
  length = 9
  lengthCustom = 14
  matchOuter = false
  offset = 0
  thread = false
  type = 39
FEATURE [Part::FeaturePython] Screw046  label="M3x14-Screw076"  # Fasteners workbench fastener (typed FeaturePython)
  Placement = pos=(-183.29,143.9,-216.76) rot=(0,1,0;1.5708rad)
  Visibility1 = true
  diameter = 1
  invert = false
  length = 9
  lengthCustom = 14
  matchOuter = false
  offset = 0
  thread = false
  type = 39
FEATURE [Part::FeaturePython] Screw047  label="M3x14-Screw075"  # Fasteners workbench fastener (typed FeaturePython)
  Placement = pos=(-183.29,103.98,-216.76) rot=(0,1,0;1.5708rad)
  Visibility1 = true
  diameter = 1
  invert = false
  length = 9
  lengthCustom = 14
  matchOuter = false
  offset = 0
  thread = false
  type = 39
FEATURE [Part::FeaturePython] Screw049  label="M3x14-Screw077"  # Fasteners workbench fastener (typed FeaturePython)
  Placement = pos=(-183.29,143.94,-256.82) rot=(0,1,0;1.5708rad)
  Visibility1 = true
  diameter = 1
  invert = false
  length = 9
  lengthCustom = 14
  matchOuter = false
  offset = 0
  thread = false
  type = 39
FEATURE [Part::FeaturePython] Screw050  label="M3x14-Screw078"  # Fasteners workbench fastener (typed FeaturePython)
  Placement = pos=(-183.29,183.95,-256.82) rot=(0,1,0;1.5708rad)
  Visibility1 = true
  diameter = 1
  invert = false
  length = 9
  lengthCustom = 14
  matchOuter = false
  offset = 0
  thread = false
  type = 39
FEATURE [Part::FeaturePython] Screw086  label="M3x8-Screw249"  # Fasteners workbench fastener (typed FeaturePython)
  Placement = pos=(-191.38,190.34,-236.74) rot=(0,1,0;1.5708rad)
  Visibility1 = true
  diameter = 1
  invert = false
  length = 1
  lengthCustom = 8
  matchOuter = false
  offset = 0
  thread = false
  type = 39
FEATURE [Part::FeaturePython] Screw087  label="M3x8-Screw255"  # Fasteners workbench fastener (typed FeaturePython)
  Placement = pos=(-191.38,212.29,-258.75) rot=(0,1,0;1.5708rad)
  Visibility1 = true
  diameter = 1
  invert = false
  length = 1
  lengthCustom = 8
  matchOuter = false
  offset = 0
  thread = false
  type = 39
FEATURE [Part::FeaturePython] Screw088  label="M3x8-Screw256"  # Fasteners workbench fastener (typed FeaturePython)
  Placement = pos=(-191.38,212.25,-214.83) rot=(0,1,0;1.5708rad)
  Visibility1 = true
  diameter = 1
  invert = false
  length = 1
  lengthCustom = 8
  matchOuter = false
  offset = 0
  thread = false
  type = 39
FEATURE [Part::FeaturePython] Nut032  label="M3-Nut188"  # Fasteners workbench fastener (typed FeaturePython)
  Placement = pos=(-196.87,104.003,-216.74) rot=(-0.250563,0.935113,-0.250563;1.63783rad)
  Visibility1 = true
  diameter = 4
  invert = false
  matchOuter = false
  offset = 0
  thread = false
  type = 7
FEATURE [Part::FeaturePython] Nut028  label="M3-Nut189"  # Fasteners workbench fastener (typed FeaturePython)
  Placement = pos=(-196.87,143.899,-216.738) rot=(-0.250563,0.935113,-0.250563;1.63783rad)
  Visibility1 = true
  diameter = 4
  invert = false
  matchOuter = false
  offset = 0
  thread = false
  type = 7
FEATURE [Part::FeaturePython] Nut027  label="M3-Nut190"  # Fasteners workbench fastener (typed FeaturePython)
  Placement = pos=(-196.87,183.96,-216.75) rot=(-0.250563,0.935113,-0.250563;1.63783rad)
  Visibility1 = true
  diameter = 4
  invert = false
  matchOuter = false
  offset = 0
  thread = false
  type = 7
FEATURE [Part::FeaturePython] Nut031  label="M3-Nut191"  # Fasteners workbench fastener (typed FeaturePython)
  Placement = pos=(-196.87,184.111,-256.628) rot=(-0.250563,0.935113,-0.250563;1.63783rad)
  Visibility1 = true
  diameter = 4
  invert = false
  matchOuter = false
  offset = 0
  thread = false
  type = 7
FEATURE [Part::FeaturePython] Nut029  label="M3-Nut192"  # Fasteners workbench fastener (typed FeaturePython)
  Placement = pos=(-196.87,104.059,-256.702) rot=(-0.250563,0.935113,-0.250563;1.63783rad)
  Visibility1 = true
  diameter = 4
  invert = false
  matchOuter = false
  offset = 0
  thread = false
  type = 7
FEATURE [Part::FeaturePython] Nut030  label="M3-Nut193"  # Fasteners workbench fastener (typed FeaturePython)
  Placement = pos=(-196.87,144.204,-256.67) rot=(-0.250563,0.935113,-0.250563;1.63783rad)
  Visibility1 = true
  diameter = 4
  invert = false
  matchOuter = false
  offset = 0
  thread = false
  type = 7
FEATURE [Part::FeaturePython] Screw044  label="M5x25-Screw084"  # Fasteners workbench fastener (typed FeaturePython)
  Placement = pos=(-174.752,99.2534,-236.782) rot=(0,1,0;1.5708rad)
  Visibility1 = true
  baseObject = -> b_FDM_0011_x_gantry_front_001_ [Edge1081]
  diameter = 6
  invert = false
  length = 6
  lengthCustom = 25
  matchOuter = false
  offset = 10.5
  thread = false
  type = 33
FEATURE [Part::FeaturePython] b_v_slot_roller1_001_005  label="v-slot-roller1_Fusion_006"  # a2plus imported part (geometry in sourceFile) (typed FeaturePython)
  Placement = pos=(-210.523,140.88,-208.379) rot=(0,0,1;1.5708rad)
  Visibility1 = true
  a2p_Version = V0.1
  fixedPosition = false
  objectType = a2pPart
  sourceFile = ./OTS/OTS-0011_v-slot-roller.step
  sourcePart = Fusion
  subassemblyImport = false
  timeLastImport = 1.64563e+09
  updateColors = true
FEATURE [Part::FeaturePython] Screw041  label="M5x10-Screw224"  # Fasteners workbench fastener (typed FeaturePython)
  Placement = pos=(-234.23,136.48,-215.89) rot=(0.57735,0.57735,-0.57735;4.18879rad)
  Visibility1 = true
  diameter = 6
  invert = false
  length = 1
  lengthCustom = 10
  matchOuter = false
  offset = 0
  thread = false
  type = 33
FEATURE [Part::FeaturePython] b_Gates_2GT_20T_Toothed_Pulley1_001_  label="Gates_2GT_20T_Toothed_Pulley1_Gates_2GT_20T_Toothed_Pulley_001"  # a2plus imported part (geometry in sourceFile) (typed FeaturePython)
  Placement = pos=(-192,212.28,-236.79) rot=(0,0,-1;1.5708rad)
  Visibility1 = true
  a2p_Version = V0.1
  fixedPosition = false
  objectType = a2pPart
  sourceFile = ./OTS/OTS-0017_GT2-20-tooth-pulley.STEP
  sourcePart = Gates_2GT_20T_Toothed_Pulley
  subassemblyImport = false
  timeLastImport = 1.64563e+09
  updateColors = true
FEATURE [Part::FeaturePython] b_FDM_0040_z_gantry_backplate_left_001_  label="FDM-0040_z-gantry-backplate-left_001"  # a2plus imported part (geometry in sourceFile) (typed FeaturePython)
  Placement = pos=(-177.8,114.9,-198.5) rot=(0,1,0;1.5708rad)
  a2p_Version = V0.1
  fixedPosition = false
  objectType = a2pPart
  sourceFile = .\FDM\FDM-0040_z-gantry-backplate-left.FCStd
  subassemblyImport = false
  timeLastImport = 1.64563e+09
  updateColors = true
FEATURE [Part::FeaturePython] Screw144  label="M3x8-Screw308"  # Fasteners workbench fastener (typed FeaturePython)
  Placement = pos=(-171.94,152.98,-209.22) rot=(0,1,0;1.5708rad)
  Visibility1 = true
  diameter = 1
  invert = false
  length = 1
  lengthCustom = 8
  matchOuter = false
  offset = 0
  thread = false
  type = 39
FEATURE [Part::FeaturePython] Screw146  label="M3x8-Screw309"  # Fasteners workbench fastener (typed FeaturePython)
  Placement = pos=(-171.94,152.87,-224.25) rot=(0,1,0;1.5708rad)
  Visibility1 = true
  diameter = 1
  invert = false
  length = 1
  lengthCustom = 8
  matchOuter = false
  offset = 0
  thread = false
  type = 39
FEATURE [Part::FeaturePython] b_FDM_0017_z_gantry_left_001_  label="FDM-0017_z-gantry-left_Body_001"  # a2plus imported part (geometry in sourceFile) (typed FeaturePython)
  Placement = pos=(-174.9,114.907,-198.489) rot=(0,1,0;1.5708rad)
  Visibility1 = true
  a2p_Version = V0.1
  fixedPosition = false
  objectType = a2pPart
  sourceFile = ./FDM/FDM-0017_z-gantry-left.FCStd
  sourcePart = Body
  subassemblyImport = false
  timeLastImport = 1.64668e+09
  updateColors = true
FEATURE [Part::FeaturePython] b_OTS_0001_00_CP40_nozzle_holder_001_  label="OTS-0001-00_CP40-nozzle-holder_Body_001"  # a2plus imported part (geometry in sourceFile) (typed FeaturePython)
  Placement = pos=(-155.29,77.1245,-212.648) rot=(0,0,1;0rad)
  Visibility1 = true
  a2p_Version = V0.1
  fixedPosition = false
  objectType = a2pPart
  sourceFile = ./OTS/OTS-0001-00_CP40-nozzle-holder.FCStd
  sourcePart = Body
  subassemblyImport = false
  timeLastImport = 1.64082e+09
  updateColors = true
FEATURE [Part::FeaturePython] b_MS4M_M51_001_  label="MS4M-M51_MS4M-M5_001"  # a2plus imported part (geometry in sourceFile) (typed FeaturePython)
  Placement = pos=(-155.33,151.852,-212.752) rot=(0,0,1;0rad)
  Visibility1 = true
  a2p_Version = V0.1
  fixedPosition = false
  objectType = a2pPart
  sourceFile = ./OTS/OTS-0018_pneumatic-coupler-MS4M-M5.STEP
  sourcePart = MS4M-M5
  subassemblyImport = false
  timeLastImport = 1.64563e+09
  updateColors = true
FEATURE [Part::FeaturePython] b_smc_stepper1_001_  label="nema11-hollow-shaft-stepper"  # a2plus imported part (geometry in sourceFile) (typed FeaturePython)
  Placement = pos=(-155.327,131.695,-212.608) rot=(1,0,0;1.5708rad)
  Visibility1 = true
  a2p_Version = V0.1
  fixedPosition = false
  objectType = a2pPart
  sourceFile = ./OTS/OTS-0013_nema11-hollow-shaft-stepper.stp
  subassemblyImport = false
  timeLastImport = 1.64563e+09
  updateColors = true
FEATURE [Part::FeaturePython] Screw148  label="M3x8-Screw304"  # Fasteners workbench fastener (typed FeaturePython)
  Placement = pos=(-171.94,149.05,-249.42) rot=(0,1,0;1.5708rad)
  Visibility1 = true
  diameter = 1
  invert = false
  length = 1
  lengthCustom = 8
  matchOuter = false
  offset = 0
  thread = false
  type = 39
FEATURE [Part::FeaturePython] Screw149  label="M3x8-Screw305"  # Fasteners workbench fastener (typed FeaturePython)
  Placement = pos=(-171.94,149.05,-264.41) rot=(0,1,0;1.5708rad)
  Visibility1 = true
  diameter = 1
  invert = false
  length = 1
  lengthCustom = 8
  matchOuter = false
  offset = 0
  thread = false
  type = 39
FEATURE [Part::FeaturePython] b_FDM_0041_z_gantry_backplate_right_001_  label="FDM-0041_z-gantry-backplate-right_Body_001"  # a2plus imported part (geometry in sourceFile) (typed FeaturePython)
  Placement = pos=(-178.019,111.086,-275.233) rot=(0,1,0;1.5708rad)
  a2p_Version = V0.1
  fixedPosition = false
  objectType = a2pPart
  sourceFile = ./FDM/FDM-0041_z-gantry-backplate-right.FCStd
  sourcePart = Body
  subassemblyImport = false
  timeLastImport = 1.64563e+09
  updateColors = true
FEATURE [Part::FeaturePython] b_FDM_0039_z_gantry_right_001_  label="FDM-0039_z-gantry-right_Body_001"  # a2plus imported part (geometry in sourceFile) (typed FeaturePython)
  Placement = pos=(-174.979,111.087,-275.15) rot=(0,1,0;1.5708rad)
  a2p_Version = V0.1
  fixedPosition = false
  objectType = a2pPart
  sourceFile = ./FDM/FDM-0039_z-gantry-right.FCStd
  sourcePart = Body
  subassemblyImport = false
  timeLastImport = 1.64668e+09
  updateColors = true
FEATURE [Part::FeaturePython] Screw048  label="M3x14-Screw079"  # Fasteners workbench fastener (typed FeaturePython)
  Placement = pos=(-183.29,103.98,-256.82) rot=(0,1,0;1.5708rad)
  Visibility1 = true
  diameter = 1
  invert = false
  length = 9
  lengthCustom = 14
  matchOuter = false
  offset = 0
  thread = false
  type = 39
FEATURE [Part::FeaturePython] Screw085  label="M3x8-Screw254"  # Fasteners workbench fastener (typed FeaturePython)
  Placement = pos=(-191.38,234.2,-236.74) rot=(0,1,0;1.5708rad)
  Visibility1 = true
  diameter = 1
  invert = false
  length = 1
  lengthCustom = 8
  matchOuter = false
  offset = 0
  thread = false
  type = 39
FEATURE [Part::FeaturePython] b_OTS_0005_00_zip_tie_001_006  label="OTS-0005-00_zip-tie_Body_007"  # a2plus imported part (geometry in sourceFile) (typed FeaturePython)
  Placement = pos=(-216.241,242.077,-301.428) rot=(0,0.707107,-0.707107;3.14159rad)
  a2p_Version = V0.1
  fixedPosition = false
  objectType = a2pPart
  sourceFile = ./OTS/OTS-0005-00_zip-tie.FCStd
  sourcePart = Body
  subassemblyImport = false
  timeLastImport = 1.64563e+09
  updateColors = true
FEATURE [Part::FeaturePython] b_OTS_0005_00_zip_tie_001_007  label="OTS-0005-00_zip-tie_Body_008"  # a2plus imported part (geometry in sourceFile) (typed FeaturePython)
  Placement = pos=(-216.241,194.377,-301.428) rot=(0,0.707107,-0.707107;3.14159rad)
  a2p_Version = V0.1
  fixedPosition = false
  objectType = a2pPart
  sourceFile = ./OTS/OTS-0005-00_zip-tie.FCStd
  sourcePart = Body
  subassemblyImport = false
  timeLastImport = 1.64563e+09
  updateColors = true
FEATURE [Part::FeaturePython] b_FDM_0009_roller_spacer_001_004  label="FDM-0009_roller-spacer_001"  # a2plus imported part (geometry in sourceFile) (typed FeaturePython)
  Placement = pos=(-196.252,164.814,-205.82) rot=(-0.57735,0.57735,-0.57735;4.18879rad)
  a2p_Version = V0.1
  fixedPosition = false
  objectType = a2pPart
  sourceFile = .\FDM\FDM-0009_roller-spacer.FCStd
  subassemblyImport = false
  timeLastImport = 1.64563e+09
  updateColors = true
FEATURE [Part::FeaturePython] b_FDM_0009_roller_spacer_001_005  label="FDM-0009_roller-spacer_002"  # a2plus imported part (geometry in sourceFile) (typed FeaturePython)
  Placement = pos=(-196.252,164.814,-267.82) rot=(-0.57735,0.57735,-0.57735;4.18879rad)
  a2p_Version = V0.1
  fixedPosition = false
  objectType = a2pPart
  sourceFile = .\FDM\FDM-0009_roller-spacer.FCStd
  subassemblyImport = false
  timeLastImport = 1.64563e+09
  updateColors = true
FEATURE [Part::FeaturePython] b_FDM_0043_001_  label="FDM-0043_001"  # a2plus imported part (geometry in sourceFile) (typed FeaturePython)
  Placement = pos=(-202.352,125.61,-236.63) rot=(0,1,0;1.5708rad)
  a2p_Version = V0.1
  fixedPosition = false
  objectType = a2pPart
  sourceFile = ./FDM/FDM-0044_x-gantry-tension-bar.FCStd
  subassemblyImport = false
  timeLastImport = 1.64563e+09
  updateColors = true
FEATURE [Part::FeaturePython] Screw164  label="M3x30-Screw"  # Fasteners workbench fastener (typed FeaturePython)
  Placement = pos=(-204.352,125.61,-205.38) rot=(0,-1,0;1.5708rad)
  baseObject = -> b_FDM_0043_001_ [Edge665]
  diameter = 4
  invert = false
  length = 9
  lengthCustom = 30
  matchOuter = false
  offset = 0
  thread = false
  type = 33
FEATURE [Part::FeaturePython] Screw165  label="M3x30-Screw111"  # Fasteners workbench fastener (typed FeaturePython)
  Placement = pos=(-192.352,121.01,-195.38) rot=(1,0,0;1.5708rad)
  baseObject = -> b_FDM_0043_001_ [Edge671]
  diameter = 4
  invert = false
  length = 9
  lengthCustom = 30
  matchOuter = false
  offset = 0
  thread = false
  type = 33
FEATURE [Part::FeaturePython] b_FDM_0043_001_001  label="FDM-0043_002"  # a2plus imported part (geometry in sourceFile) (typed FeaturePython)
  Placement = pos=(-216.445,125.95,-237.23) rot=(0.000545,-1,0.000545;1.5708rad)
  a2p_Version = V0.1
  fixedPosition = false
  objectType = a2pPart
  sourceFile = ./FDM/FDM-0044_x-gantry-tension-bar.FCStd
  subassemblyImport = false
  timeLastImport = 1.64563e+09
  updateColors = true
FEATURE [Part::FeaturePython] Screw166  label="M3x30-Screw112"  # Fasteners workbench fastener (typed FeaturePython)
  Placement = pos=(-226.29,121.01,-195.38) rot=(1,0,0;1.5708rad)
  baseObject = -> b_FDM_0043_001_001 [Edge60]
  diameter = 4
  invert = false
  length = 9
  lengthCustom = 30
  matchOuter = false
  offset = 0
  thread = false
  type = 33
FEATURE [Part::FeaturePython] Screw167  label="M3x30-Screw113"  # Fasteners workbench fastener (typed FeaturePython)
  Placement = pos=(-226.287,121.01,-277.88) rot=(1,0,0;1.5708rad)
  baseObject = -> b_FDM_0043_001_001 [Edge69]
  diameter = 4
  invert = false
  length = 9
  lengthCustom = 30
  matchOuter = false
  offset = 0
  thread = false
  type = 33
FEATURE [Part::FeaturePython] Screw  label="M5x40-Screw283"  # Fasteners workbench fastener (typed FeaturePython)
  Placement = pos=(-191.252,164.814,-267.82) rot=(0,1,0;1.5708rad)
  diameter = 6
  invert = true
  length = 9
  lengthCustom = 40
  matchOuter = false
  offset = 0
  thread = false
  type = 33
FEATURE [Part::FeaturePython] Screw168  label="M5x40-Screw296"  # Fasteners workbench fastener (typed FeaturePython)
  Placement = pos=(-192.252,164.814,-205.82) rot=(0,1,0;1.5708rad)
  diameter = 6
  invert = true
  length = 9
  lengthCustom = 40
  matchOuter = false
  offset = 0
  thread = false
  type = 33
FEATURE [Part::FeaturePython] Screw169  label="M5x40-Screw285"  # Fasteners workbench fastener (typed FeaturePython)
  Placement = pos=(-191.25,125.61,-205.38) rot=(0,1,0;1.5708rad)
  diameter = 6
  invert = true
  length = 9
  lengthCustom = 40
  matchOuter = false
  offset = 0
  thread = false
  type = 33
FEATURE [Part::FeaturePython] Screw170  label="M5x40-Screw286"  # Fasteners workbench fastener (typed FeaturePython)
  Placement = pos=(-191.331,125.61,-267.88) rot=(0,1,0;1.5708rad)
  diameter = 6
  invert = true
  length = 9
  lengthCustom = 40
  matchOuter = false
  offset = 0
  thread = false
  type = 33
FEATURE [Part::FeaturePython] Nut068  label="M3-Nut267"  # Fasteners workbench fastener (typed FeaturePython)
  Placement = pos=(-226.287,146.5,-195.38) rot=(1,0,0;1.5708rad)
  diameter = 4
  invert = false
  matchOuter = false
  offset = 0
  thread = false
  type = 7
FEATURE [Part::FeaturePython] Nut069  label="M3-Nut265"  # Fasteners workbench fastener (typed FeaturePython)
  Placement = pos=(-226.287,146.5,-278.08) rot=(1,0,0;1.5708rad)
  diameter = 4
  invert = false
  matchOuter = false
  offset = 0
  thread = false
  type = 7
FEATURE [Part::FeaturePython] Nut070  label="M3-Nut196"  # Fasteners workbench fastener (typed FeaturePython)
  Placement = pos=(-192.653,146.5,-277.881) rot=(1,0,0;1.5708rad)
  diameter = 4
  invert = false
  matchOuter = false
  offset = 0
  thread = false
  type = 7
FEATURE [Part::FeaturePython] Nut071  label="M3-Nut197"  # Fasteners workbench fastener (typed FeaturePython)
  Placement = pos=(-192.653,146.5,-195.381) rot=(1,0,0;1.5708rad)
  diameter = 4
  invert = false
  matchOuter = false
  offset = 0
  thread = false
  type = 7
FEATURE [Part::FeaturePython] Screw171  label="M3x14-Screw104"  # Fasteners workbench fastener (typed FeaturePython)
  Placement = pos=(-236.252,118.069,-259.574) rot=(0,-1,0;1.5708rad)
  baseObject = -> b_FDM_0014_down_camera_mount_001_ [Edge38]
  diameter = 1
  invert = false
  length = 9
  lengthCustom = 14
  matchOuter = false
  offset = 0
  thread = false
  type = 39
FEATURE [Part::FeaturePython] Nut077  label="M3-Nut268"  # Fasteners workbench fastener (typed FeaturePython)
  Placement = pos=(-226.18,118.324,-214.319) rot=(0,-1,0;1.5708rad)
  diameter = 4
  invert = false
  matchOuter = false
  offset = 0
  thread = false
  type = 7
FEATURE [Part::FeaturePython] Nut079  label="M3-Nut264"  # Fasteners workbench fastener (typed FeaturePython)
  Placement = pos=(-226.18,118.32,-259.319) rot=(-0.250563,-0.935113,0.250563;1.63783rad)
  diameter = 4
  invert = false
  matchOuter = false
  offset = 0
  thread = false
  type = 7
FEATURE [Part::FeaturePython] b_OTS_0011_v_slot_roller1_001_  label="OTS-0011_v-slot-roller1_001"  # a2plus imported part (geometry in sourceFile) (typed FeaturePython)
  Placement = pos=(-210.523,140.88,-270.879) rot=(0,0,1;1.5708rad)
  a2p_Version = V0.1
  fixedPosition = false
  objectType = a2pPart
  sourceFile = .\OTS\OTS-0011_v-slot-roller.step
  subassemblyImport = false
  timeLastImport = 1.64563e+09
  updateColors = true
FEATURE [Part::FeaturePython] Screw125  label="M3x8-Screw263"  # Fasteners workbench fastener (typed FeaturePython)
  Placement = pos=(64.09,109.94,11.7) rot=(0,0,1;0rad)
  Visibility1 = true
  diameter = 1
  invert = false
  length = 1
  lengthCustom = 8
  matchOuter = false
  offset = 0
  thread = false
  type = 39
FEATURE [Part::FeaturePython] Screw126  label="M3x8-Screw264"  # Fasteners workbench fastener (typed FeaturePython)
  Placement = pos=(64.09,90.95,11.84) rot=(0,0,1;0rad)
  Visibility1 = true
  diameter = 1
  invert = false
  length = 1
  lengthCustom = 8
  matchOuter = false
  offset = 0
  thread = false
  type = 39
FEATURE [Part::FeaturePython] Screw101  label="M5x25-Screw080"  # Fasteners workbench fastener (typed FeaturePython)
  Placement = pos=(95.23,64.96,-4.92) rot=(0.57735,-0.57735,0.57735;4.18879rad)
  Visibility1 = true
  diameter = 6
  invert = false
  length = 6
  lengthCustom = 25
  matchOuter = false
  offset = 0
  thread = false
  type = 33
FEATURE [Part::FeaturePython] Screw102  label="M5x25-Screw081"  # Fasteners workbench fastener (typed FeaturePython)
  Placement = pos=(95.23,49.94,-4.92) rot=(0.57735,-0.57735,0.57735;4.18879rad)
  Visibility1 = true
  diameter = 6
  invert = false
  length = 6
  lengthCustom = 25
  matchOuter = false
  offset = 0
  thread = false
  type = 33
FEATURE [Part::FeaturePython] b_M5_tslot_nut1_001_008  label="M5-tslot-nut1_T_Slot_Nut_Dropin_M5 v1_009"  # a2plus imported part (geometry in sourceFile) (typed FeaturePython)
  Placement = pos=(70.1584,105.165,-9.94821) rot=(0,0.707107,0.707107;3.14159rad)
  Visibility1 = true
  a2p_Version = V0.1
  fixedPosition = false
  objectType = a2pPart
  sourceFile = ./FST/FST-0016_M5-tslot-nut.step
  sourcePart = T_Slot_Nut_Dropin_M5 v1
  subassemblyImport = false
  timeLastImport = 1.64563e+09
  updateColors = true
FEATURE [Part::FeaturePython] Nut048  label="M3-Nut202"  # Fasteners workbench fastener (typed FeaturePython)
  Placement = pos=(93.169,99.99,-24.9656) rot=(0.57735,0.57735,0.57735;2.0944rad)
  Visibility1 = true
  diameter = 4
  invert = false
  matchOuter = false
  offset = 0
  thread = false
  type = 7
FEATURE [Part::FeaturePython] Nut045  label="M5-Nut467"  # Fasteners workbench fastener (typed FeaturePython)
  Placement = pos=(97.4915,83.9035,5.03877) rot=(-0.186157,-0.694747,0.694747;3.50969rad)
  Visibility1 = true
  diameter = 3
  invert = false
  matchOuter = false
  offset = 0
  thread = false
  type = 5
FEATURE [Part::FeaturePython] b_Gates_2GT_20T_Toothed_Idler1_001_001  label="Gates_2GT_20T_Toothed_Idler1_Gates_2GT_20T_Toothed_Idler_002"  # a2plus imported part (geometry in sourceFile) (typed FeaturePython)
  Placement = pos=(97.7236,95.0003,-10.0586) rot=(0,0,1;0rad)
  Visibility1 = true
  a2p_Version = V0.1
  fixedPosition = false
  objectType = a2pPart
  sourceFile = ./OTS/OTS-0016_GT2-20-tooth-idler.STEP
  sourcePart = Gates_2GT_20T_Toothed_Idler
  subassemblyImport = false
  timeLastImport = 1.64563e+09
  updateColors = true
FEATURE [Part::FeaturePython] Nut033  label="M5-Nut466"  # Fasteners workbench fastener (typed FeaturePython)
  Placement = pos=(97.5692,89.9635,-9.97594) rot=(0,0.707107,-0.707107;3.14159rad)
  Visibility1 = true
  diameter = 3
  invert = false
  matchOuter = false
  offset = 0
  thread = false
  type = 5
FEATURE [Part::FeaturePython] Screw052  label="M3x16-Screw041"  # Fasteners workbench fastener (typed FeaturePython)
  Placement = pos=(102.16,100,-24.99) rot=(0.57735,0.57735,0.57735;2.0944rad)
  Visibility1 = true
  diameter = 4
  invert = false
  length = 6
  lengthCustom = 16
  matchOuter = false
  offset = 0
  thread = false
  type = 33
FEATURE [Part::FeaturePython] Screw053  label="M5x10-Screw206"  # Fasteners workbench fastener (typed FeaturePython)
  Placement = pos=(70.16,114.96,-9.89) rot=(-1,0,0;1.5708rad)
  Visibility1 = true
  diameter = 6
  invert = false
  length = 1
  lengthCustom = 10
  matchOuter = false
  offset = 0
  thread = false
  type = 33
FEATURE [Part::FeaturePython] Screw054  label="M5x25-Screw082"  # Fasteners workbench fastener (typed FeaturePython)
  Placement = pos=(97.57,109.98,-9.99) rot=(-1,0,0;1.5708rad)
  Visibility1 = true
  diameter = 6
  invert = false
  length = 6
  lengthCustom = 25
  matchOuter = false
  offset = 0
  thread = false
  type = 33
FEATURE [Part::FeaturePython] Screw035  label="M5x10-Screw207"  # Fasteners workbench fastener (typed FeaturePython)
  Placement = pos=(45.15,30.1,4.92) rot=(0,0,1;0rad)
  Visibility1 = true
  diameter = 6
  invert = false
  length = 1
  lengthCustom = 10
  matchOuter = false
  offset = 0
  thread = false
  type = 33
FEATURE [Part::FeaturePython] Screw036  label="M5x10-Screw208"  # Fasteners workbench fastener (typed FeaturePython)
  Placement = pos=(70.14,30.1,4.92) rot=(0,0,1;0rad)
  Visibility1 = true
  diameter = 6
  invert = false
  length = 1
  lengthCustom = 10
  matchOuter = false
  offset = 0
  thread = false
  type = 33
FEATURE [Part::FeaturePython] Screw037  label="M5x10-Screw209"  # Fasteners workbench fastener (typed FeaturePython)
  Placement = pos=(25.33,9.99,-9.96) rot=(0,1,0;1.5708rad)
  Visibility1 = true
  diameter = 6
  invert = false
  length = 1
  lengthCustom = 10
  matchOuter = false
  offset = 0
  thread = false
  type = 33
FEATURE [Part::FeaturePython] Screw051  label="M5x40-Screw288"  # Fasteners workbench fastener (typed FeaturePython)
  Placement = pos=(97.58,119.74,4.98) rot=(-1,0,0;1.5708rad)
  Visibility1 = true
  diameter = 6
  invert = false
  length = 12
  lengthCustom = 40
  matchOuter = false
  offset = 0
  thread = false
  type = 33
FEATURE [Part::FeaturePython] b_M5_tslot_nut1_001_009  label="M5-tslot-nut1_T_Slot_Nut_Dropin_M5 v1_010"  # a2plus imported part (geometry in sourceFile) (typed FeaturePython)
  Placement = pos=(70.1584,30.1746,-4.76821) rot=(0,0,1;3.14159rad)
  Visibility1 = true
  a2p_Version = V0.1
  fixedPosition = false
  objectType = a2pPart
  sourceFile = ./FST/FST-0016_M5-tslot-nut.step
  sourcePart = T_Slot_Nut_Dropin_M5 v1
  subassemblyImport = false
  timeLastImport = 1.64563e+09
  updateColors = true
FEATURE [Part::FeaturePython] b_M5_tslot_nut1_001_010  label="M5-tslot-nut1_T_Slot_Nut_Dropin_M5 v1_011"  # a2plus imported part (geometry in sourceFile) (typed FeaturePython)
  Placement = pos=(45.2084,30.1746,-4.76821) rot=(0,0,1;3.14159rad)
  Visibility1 = true
  a2p_Version = V0.1
  fixedPosition = false
  objectType = a2pPart
  sourceFile = ./FST/FST-0016_M5-tslot-nut.step
  sourcePart = T_Slot_Nut_Dropin_M5 v1
  subassemblyImport = false
  timeLastImport = 1.64563e+09
  updateColors = true
FEATURE [Part::FeaturePython] b_M5_tslot_nut1_001_011  label="M5-tslot-nut1_T_Slot_Nut_Dropin_M5 v1_012"  # a2plus imported part (geometry in sourceFile) (typed FeaturePython)
  Placement = pos=(15.0384,9.95457,-9.85821) rot=(0.707107,0,0.707107;3.14159rad)
  Visibility1 = true
  a2p_Version = V0.1
  fixedPosition = false
  objectType = a2pPart
  sourceFile = ./FST/FST-0016_M5-tslot-nut.step
  sourcePart = T_Slot_Nut_Dropin_M5 v1
  subassemblyImport = false
  timeLastImport = 1.64563e+09
  updateColors = true
FEATURE [Part::FeaturePython] b_FDM_0001_front_left_leg_001_  label="FDM-0001_front-left-leg_Body_001"  # a2plus imported part (geometry in sourceFile) (typed FeaturePython)
  Placement = pos=(0.0519684,19.9889,-19.9755) rot=(0,0,1;0rad)
  Visibility1 = true
  a2p_Version = V0.1
  fixedPosition = false
  objectType = a2pPart
  sourceFile = ./FDM/FDM-0001_front-left-leg.FCStd
  sourcePart = Body
  subassemblyImport = false
  timeLastImport = 1.64563e+09
  updateColors = true
FEATURE [Part::FeaturePython] b_front_leg_tensioner_001_  label="front-leg-tensioner_Body_001"  # a2plus imported part (geometry in sourceFile) (typed FeaturePython)
  Placement = pos=(92.5935,89.9815,10.0388) rot=(0,1,0;1.5708rad)
  Visibility1 = true
  a2p_Version = V0.1
  fixedPosition = false
  objectType = a2pPart
  sourceFile = ./FDM/FDM-0037_belt-tension-arm.FCStd
  sourcePart = Body
  subassemblyImport = false
  timeLastImport = 1.64563e+09
  updateColors = true
FEATURE [Part::FeaturePython] b_FDM_0007_frame_umbilical_mount_001_  label="FDM-0007_frame-umbilical-mount_Body_001"  # a2plus imported part (geometry in sourceFile) (typed FeaturePython)
  Placement = pos=(85.0258,109.915,-19.9467) rot=(0.57735,0.57735,-0.57735;2.0944rad)
  Visibility1 = true
  a2p_Version = V0.1
  fixedPosition = false
  objectType = a2pPart
  sourceFile = ./FDM/FDM-0007_frame-umbilical-mount.FCStd
  sourcePart = Body
  subassemblyImport = false
  timeLastImport = 1.64563e+09
  updateColors = true
FEATURE [Part::FeaturePython] b_MakerBot_LimitSwitchBoard1_001_  label="MakerBot LimitSwitchBoard1_MakerBot LimitSwitchBoard_001"  # a2plus imported part (geometry in sourceFile) (typed FeaturePython)
  Placement = pos=(69.4012,93.4234,10.0674) rot=(0.57735,0.57735,0.57735;2.0944rad)
  Visibility1 = true
  a2p_Version = V0.1
  fixedPosition = false
  objectType = a2pPart
  sourceFile = ./OTS/OTS-0019_limit-switch-PCBA.STEP
  sourcePart = MakerBot LimitSwitchBoard
  subassemblyImport = false
  timeLastImport = 1.64563e+09
  updateColors = true
FEATURE [Part::FeaturePython] b_OTS_0005_00_zip_tie_001_002  label="OTS-0005-00_zip-tie_Body_003"  # a2plus imported part (geometry in sourceFile) (typed FeaturePython)
  Placement = pos=(116.859,105.377,30.0715) rot=(0.57735,0.57735,-0.57735;2.0944rad)
  a2p_Version = V0.1
  fixedPosition = false
  objectType = a2pPart
  sourceFile = ./OTS/OTS-0005-00_zip-tie.FCStd
  sourcePart = Body
  subassemblyImport = false
  timeLastImport = 1.64563e+09
  updateColors = true
FEATURE [Part::FeaturePython] b_OTS_0005_00_zip_tie_001_003  label="OTS-0005-00_zip-tie_Body_004"  # a2plus imported part (geometry in sourceFile) (typed FeaturePython)
  Placement = pos=(116.859,49.1766,30.0715) rot=(0.57735,0.57735,-0.57735;2.0944rad)
  a2p_Version = V0.1
  fixedPosition = false
  objectType = a2pPart
  sourceFile = ./OTS/OTS-0005-00_zip-tie.FCStd
  sourcePart = Body
  subassemblyImport = false
  timeLastImport = 1.64563e+09
  updateColors = true
FEATURE [Part::FeaturePython] b_FDM_0002_front_right_leg_001_001  label="FDM-0002_front-right-leg_Body_001"  # a2plus imported part (geometry in sourceFile) (typed FeaturePython)
  Placement = pos=(0.021554,20.0136,-580.091) rot=(0,0,1;0rad)
  a2p_Version = V0.1
  fixedPosition = false
  objectType = a2pPart
  sourceFile = ./FDM/FDM-0002_front-right-leg.FCStd
  sourcePart = Body
  subassemblyImport = false
  timeLastImport = 1.64563e+09
  updateColors = true
FEATURE [Part::FeaturePython] Screw061  label="M5x40-Screw287"  # Fasteners workbench fastener (typed FeaturePython)
  Placement = pos=(97.58,119.74,-605.12) rot=(-1,0,0;1.5708rad)
  Visibility1 = true
  diameter = 6
  invert = false
  length = 12
  lengthCustom = 40
  matchOuter = false
  offset = 0
  thread = false
  type = 33
FEATURE [Part::FeaturePython] b_front_leg_tensioner_001_002  label="front-leg-tensioner_Body_003"  # a2plus imported part (geometry in sourceFile) (typed FeaturePython)
  Placement = pos=(92.5035,110.071,-610.041) rot=(0.707107,0,0.707107;3.14159rad)
  Visibility1 = true
  a2p_Version = V0.1
  fixedPosition = false
  objectType = a2pPart
  sourceFile = ./FDM/FDM-0037_belt-tension-arm.FCStd
  sourcePart = Body
  subassemblyImport = false
  timeLastImport = 1.64563e+09
  updateColors = true
FEATURE [Part::FeaturePython] b_Gates_2GT_20T_Toothed_Idler1_001_003  label="Gates_2GT_20T_Toothed_Idler1_Gates_2GT_20T_Toothed_Idler_004"  # a2plus imported part (geometry in sourceFile) (typed FeaturePython)
  Placement = pos=(97.7236,95.0003,-590.059) rot=(0,0,1;0rad)
  Visibility1 = true
  a2p_Version = V0.1
  fixedPosition = false
  objectType = a2pPart
  sourceFile = ./OTS/OTS-0016_GT2-20-tooth-idler.STEP
  sourcePart = Gates_2GT_20T_Toothed_Idler
  subassemblyImport = false
  timeLastImport = 1.64563e+09
  updateColors = true
FEATURE [Part::FeaturePython] Nut046  label="M5-Nut469"  # Fasteners workbench fastener (typed FeaturePython)
  Placement = pos=(97.4581,83.9035,-605.043) rot=(-0.186157,-0.694747,0.694747;3.50969rad)
  Visibility1 = true
  diameter = 3
  invert = false
  matchOuter = false
  offset = 0
  thread = false
  type = 5
FEATURE [Part::FeaturePython] Screw062  label="M5x25-Screw083"  # Fasteners workbench fastener (typed FeaturePython)
  Placement = pos=(97.57,109.98,-590.06) rot=(-1,0,0;1.5708rad)
  Visibility1 = true
  diameter = 6
  invert = false
  length = 6
  lengthCustom = 25
  matchOuter = false
  offset = 0
  thread = false
  type = 33
FEATURE [Part::FeaturePython] Nut047  label="M5-Nut468"  # Fasteners workbench fastener (typed FeaturePython)
  Placement = pos=(97.5092,89.9635,-590.046) rot=(0,0.707107,-0.707107;3.14159rad)
  Visibility1 = true
  diameter = 3
  invert = false
  matchOuter = false
  offset = 0
  thread = false
  type = 5
FEATURE [Part::FeaturePython] Screw063  label="M3x16-Screw042"  # Fasteners workbench fastener (typed FeaturePython)
  Placement = pos=(101,100,-574.97) rot=(0.57735,0.57735,0.57735;2.0944rad)
  Visibility1 = true
  diameter = 4
  invert = false
  length = 6
  lengthCustom = 16
  matchOuter = false
  offset = 0
  thread = false
  type = 33
FEATURE [Part::FeaturePython] Nut049  label="M3-Nut203"  # Fasteners workbench fastener (typed FeaturePython)
  Placement = pos=(93.169,99.99,-575.026) rot=(0.57735,0.57735,0.57735;2.0944rad)
  Visibility1 = true
  diameter = 4
  invert = false
  matchOuter = false
  offset = 0
  thread = false
  type = 7
FEATURE [Part::FeaturePython] Screw064  label="M5x10-Screw210"  # Fasteners workbench fastener (typed FeaturePython)
  Placement = pos=(70.16,114.96,-590.19) rot=(-1,0,0;1.5708rad)
  Visibility1 = true
  diameter = 6
  invert = false
  length = 1
  lengthCustom = 10
  matchOuter = false
  offset = 0
  thread = false
  type = 33
FEATURE [Part::FeaturePython] Screw070  label="M5x10-Screw211"  # Fasteners workbench fastener (typed FeaturePython)
  Placement = pos=(70,29.99,-605) rot=(1,0,0;3.14159rad)
  Visibility1 = true
  diameter = 6
  invert = false
  length = 1
  lengthCustom = 10
  matchOuter = false
  offset = 0
  thread = false
  type = 33
FEATURE [Part::FeaturePython] Screw071  label="M5x10-Screw212"  # Fasteners workbench fastener (typed FeaturePython)
  Placement = pos=(44.99,29.99,-605) rot=(1,0,0;3.14159rad)
  Visibility1 = true
  diameter = 6
  invert = false
  length = 1
  lengthCustom = 10
  matchOuter = false
  offset = 0
  thread = false
  type = 33
FEATURE [Part::FeaturePython] Screw072  label="M5x10-Screw213"  # Fasteners workbench fastener (typed FeaturePython)
  Placement = pos=(24.98,10.2,-589.91) rot=(0.707107,0,0.707107;3.14159rad)
  Visibility1 = true
  diameter = 6
  invert = false
  length = 1
  lengthCustom = 10
  matchOuter = false
  offset = 0
  thread = false
  type = 33
FEATURE [Part::FeaturePython] b_M5_tslot_nut1_001_012  label="M5-tslot-nut1_T_Slot_Nut_Dropin_M5 v1_013"  # a2plus imported part (geometry in sourceFile) (typed FeaturePython)
  Placement = pos=(15.0384,10.1446,-590.068) rot=(0.707107,0,0.707107;3.14159rad)
  Visibility1 = true
  a2p_Version = V0.1
  fixedPosition = false
  objectType = a2pPart
  sourceFile = ./FST/FST-0016_M5-tslot-nut.step
  sourcePart = T_Slot_Nut_Dropin_M5 v1
  subassemblyImport = false
  timeLastImport = 1.64563e+09
  updateColors = true
FEATURE [Part::FeaturePython] b_M5_tslot_nut1_001_013  label="M5-tslot-nut1_T_Slot_Nut_Dropin_M5 v1_014"  # a2plus imported part (geometry in sourceFile) (typed FeaturePython)
  Placement = pos=(70.0184,30.1846,-595.208) rot=(1,0,0;3.14159rad)
  Visibility1 = true
  a2p_Version = V0.1
  fixedPosition = false
  objectType = a2pPart
  sourceFile = ./FST/FST-0016_M5-tslot-nut.step
  sourcePart = T_Slot_Nut_Dropin_M5 v1
  subassemblyImport = false
  timeLastImport = 1.64563e+09
  updateColors = true
FEATURE [Part::FeaturePython] b_M5_tslot_nut1_001_014  label="M5-tslot-nut1_T_Slot_Nut_Dropin_M5 v1_015"  # a2plus imported part (geometry in sourceFile) (typed FeaturePython)
  Placement = pos=(44.9784,30.1846,-595.208) rot=(1,0,0;3.14159rad)
  Visibility1 = true
  a2p_Version = V0.1
  fixedPosition = false
  objectType = a2pPart
  sourceFile = ./FST/FST-0016_M5-tslot-nut.step
  sourcePart = T_Slot_Nut_Dropin_M5 v1
  subassemblyImport = false
  timeLastImport = 1.64563e+09
  updateColors = true
FEATURE [Part::FeaturePython] b_M5_tslot_nut1_001_015  label="M5-tslot-nut1_T_Slot_Nut_Dropin_M5 v1_016"  # a2plus imported part (geometry in sourceFile) (typed FeaturePython)
  Placement = pos=(70.0484,105.085,-589.988) rot=(-1,0,0;1.5708rad)
  Visibility1 = true
  a2p_Version = V0.1
  fixedPosition = false
  objectType = a2pPart
  sourceFile = ./FST/FST-0016_M5-tslot-nut.step
  sourcePart = T_Slot_Nut_Dropin_M5 v1
  subassemblyImport = false
  timeLastImport = 1.64563e+09
  updateColors = true
FEATURE [Part::FeaturePython] Screw089  label="M3x8-Screw265"  # Fasteners workbench fastener (typed FeaturePython)
  Placement = pos=(-531.08,115.09,5.54) rot=(0.57735,0.57735,-0.57735;2.0944rad)
  Visibility1 = true
  diameter = 1
  invert = false
  length = 1
  lengthCustom = 8
  matchOuter = false
  offset = 0
  thread = false
  type = 39
FEATURE [Part::FeaturePython] Screw090  label="M3x8-Screw266"  # Fasteners workbench fastener (typed FeaturePython)
  Placement = pos=(-562.08,115.09,5.54) rot=(0.57735,0.57735,-0.57735;2.0944rad)
  Visibility1 = true
  diameter = 1
  invert = false
  length = 1
  lengthCustom = 8
  matchOuter = false
  offset = 0
  thread = false
  type = 39
FEATURE [Part::FeaturePython] Screw091  label="M3x8-Screw267"  # Fasteners workbench fastener (typed FeaturePython)
  Placement = pos=(-562.08,115.09,-25.34) rot=(0.57735,0.57735,-0.57735;2.0944rad)
  Visibility1 = true
  diameter = 1
  invert = false
  length = 1
  lengthCustom = 8
  matchOuter = false
  offset = 0
  thread = false
  type = 39
FEATURE [Part::FeaturePython] Screw092  label="M3x8-Screw268"  # Fasteners workbench fastener (typed FeaturePython)
  Placement = pos=(-531.13,115.09,-25.34) rot=(0.57735,0.57735,-0.57735;2.0944rad)
  Visibility1 = true
  diameter = 1
  invert = false
  length = 1
  lengthCustom = 8
  matchOuter = false
  offset = 0
  thread = false
  type = 39
FEATURE [Part::FeaturePython] b_Nema_17_42A02C_v21_001_002  label="Nema 17 42A02C v21_ Nema 17 42A02C v2_003"  # a2plus imported part (geometry in sourceFile) (typed FeaturePython)
  Placement = pos=(-546.538,110.248,-9.83619) rot=(1,0,0;1.5708rad)
  Visibility1 = true
  a2p_Version = V0.1
  fixedPosition = false
  objectType = a2pPart
  sourceFile = ./OTS/OTS-0012_nema17-stepper.step
  sourcePart =  Nema 17 42A02C v2
  subassemblyImport = false
  timeLastImport = 1.64563e+09
  updateColors = true
FEATURE [Part::FeaturePython] b_Gates_2GT_20T_Toothed_Pulley1_001_002  label="Gates_2GT_20T_Toothed_Pulley1_Gates_2GT_20T_Toothed_Pulley_003"  # a2plus imported part (geometry in sourceFile) (typed FeaturePython)
  Placement = pos=(-546.519,111.281,-9.82042) rot=(0,0,1;3.14159rad)
  Visibility1 = true
  a2p_Version = V0.1
  fixedPosition = false
  objectType = a2pPart
  sourceFile = ./OTS/OTS-0017_GT2-20-tooth-pulley.STEP
  sourcePart = Gates_2GT_20T_Toothed_Pulley
  subassemblyImport = false
  timeLastImport = 1.64563e+09
  updateColors = true
FEATURE [Part::FeaturePython] Screw029  label="M5x10-Screw214"  # Fasteners workbench fastener (typed FeaturePython)
  Placement = pos=(-510.06,115.05,-9.89) rot=(-1,0,0;1.5708rad)
  Visibility1 = true
  diameter = 6
  invert = false
  length = 1
  lengthCustom = 10
  matchOuter = false
  offset = 0
  thread = false
  type = 33
FEATURE [Part::FeaturePython] Screw030  label="M5x10-Screw215"  # Fasteners workbench fastener (typed FeaturePython)
  Placement = pos=(-510.06,30.11,6.57) rot=(0,0,1;0rad)
  Visibility1 = true
  diameter = 6
  invert = false
  length = 1
  lengthCustom = 10
  matchOuter = false
  offset = 0
  thread = false
  type = 33
FEATURE [Part::FeaturePython] Screw031  label="M5x10-Screw216"  # Fasteners workbench fastener (typed FeaturePython)
  Placement = pos=(-510.06,30.11,-26.33) rot=(1,0,0;3.14159rad)
  Visibility1 = true
  diameter = 6
  invert = false
  length = 1
  lengthCustom = 10
  matchOuter = false
  offset = 0
  thread = false
  type = 33
FEATURE [Part::FeaturePython] b_M5_tslot_nut1_001_002  label="M5-tslot-nut1_T_Slot_Nut_Dropin_M5 v1_003"  # a2plus imported part (geometry in sourceFile) (typed FeaturePython)
  Placement = pos=(-510.062,105.175,-9.95821) rot=(-1,0,0;1.5708rad)
  Visibility1 = true
  a2p_Version = V0.1
  fixedPosition = false
  objectType = a2pPart
  sourceFile = ./FST/FST-0016_M5-tslot-nut.step
  sourcePart = T_Slot_Nut_Dropin_M5 v1
  subassemblyImport = false
  timeLastImport = 1.64563e+09
  updateColors = true
FEATURE [Part::FeaturePython] b_M5_tslot_nut1_001_003  label="M5-tslot-nut1_T_Slot_Nut_Dropin_M5 v1_004"  # a2plus imported part (geometry in sourceFile) (typed FeaturePython)
  Placement = pos=(-510.062,30.0846,-4.86821) rot=(0,0,1;0rad)
  Visibility1 = true
  a2p_Version = V0.1
  fixedPosition = false
  objectType = a2pPart
  sourceFile = ./FST/FST-0016_M5-tslot-nut.step
  sourcePart = T_Slot_Nut_Dropin_M5 v1
  subassemblyImport = false
  timeLastImport = 1.64563e+09
  updateColors = true
FEATURE [Part::FeaturePython] b_M5_tslot_nut1_001_004  label="M5-tslot-nut1_T_Slot_Nut_Dropin_M5 v1_005"  # a2plus imported part (geometry in sourceFile) (typed FeaturePython)
  Placement = pos=(-510.062,30.0846,-14.8982) rot=(1,0,0;3.14159rad)
  Visibility1 = true
  a2p_Version = V0.1
  fixedPosition = false
  objectType = a2pPart
  sourceFile = ./FST/FST-0016_M5-tslot-nut.step
  sourcePart = T_Slot_Nut_Dropin_M5 v1
  subassemblyImport = false
  timeLastImport = 1.64563e+09
  updateColors = true
FEATURE [Part::FeaturePython] b_FDM_0003_back_left_leg_001_  label="FDM-0003_back-left-leg_Body_001"  # a2plus imported part (geometry in sourceFile) (typed FeaturePython)
  Placement = pos=(-500.067,-49.8885,-31.4133) rot=(0,0,1;0rad)
  Visibility1 = true
  a2p_Version = V0.1
  fixedPosition = false
  objectType = a2pPart
  sourceFile = ./FDM/FDM-0003_back-left-leg.FCStd
  sourcePart = Body
  subassemblyImport = false
  timeLastImport = 1.64563e+09
  updateColors = true
FEATURE [App::DocumentObjectGroup] Group006  label="Back-Left-Leg"
  Group = -> [Screw089,Screw090,Screw091,Screw092,b_Nema_17_42A02C_v21_001_002,b_Gates_2GT_20T_Toothed_Pulley1_001_002,Screw029,Screw030,Screw031,b_M5_tslot_nut1_001_002,b_M5_tslot_nut1_001_003,b_M5_tslot_nut1_001_004,b_FDM_0003_back_left_leg_001_]
FEATURE [Part::FeaturePython] b_FDM_0004_back_right_leg_001_  label="FDM-0004_back-right-leg_Body_001"  # a2plus imported part (geometry in sourceFile) (typed FeaturePython)
  Placement = pos=(-500.064,-49.9003,-611.504) rot=(0,0,1;0rad)
  Visibility1 = true
  a2p_Version = V0.1
  fixedPosition = false
  objectType = a2pPart
  sourceFile = ./FDM/FDM-0004_back-right-leg.FCStd
  sourcePart = Body
  subassemblyImport = false
  timeLastImport = 1.64563e+09
  updateColors = true
FEATURE [Part::FeaturePython] b_Gates_2GT_20T_Toothed_Pulley1_001_003  label="Gates_2GT_20T_Toothed_Pulley1_Gates_2GT_20T_Toothed_Pulley_004"  # a2plus imported part (geometry in sourceFile) (typed FeaturePython)
  Placement = pos=(-546.519,111.281,-590.02) rot=(0,0,1;3.14159rad)
  Visibility1 = true
  a2p_Version = V0.1
  fixedPosition = false
  objectType = a2pPart
  sourceFile = ./OTS/OTS-0017_GT2-20-tooth-pulley.STEP
  sourcePart = Gates_2GT_20T_Toothed_Pulley
  subassemblyImport = false
  timeLastImport = 1.64563e+09
  updateColors = true
FEATURE [Part::FeaturePython] Screw096  label="M3x8-Screw269"  # Fasteners workbench fastener (typed FeaturePython)
  Placement = pos=(-531.08,115.09,-574.62) rot=(0.57735,0.57735,-0.57735;2.0944rad)
  Visibility1 = true
  diameter = 1
  invert = false
  length = 1
  lengthCustom = 8
  matchOuter = false
  offset = 0
  thread = false
  type = 39
FEATURE [Part::FeaturePython] Screw093  label="M3x8-Screw270"  # Fasteners workbench fastener (typed FeaturePython)
  Placement = pos=(-562.08,115.09,-574.62) rot=(0.57735,0.57735,-0.57735;2.0944rad)
  Visibility1 = true
  diameter = 1
  invert = false
  length = 1
  lengthCustom = 8
  matchOuter = false
  offset = 0
  thread = false
  type = 39
FEATURE [Part::FeaturePython] Screw094  label="M3x8-Screw271"  # Fasteners workbench fastener (typed FeaturePython)
  Placement = pos=(-562.08,115.09,-605.65) rot=(0.57735,0.57735,-0.57735;2.0944rad)
  Visibility1 = true
  diameter = 1
  invert = false
  length = 1
  lengthCustom = 8
  matchOuter = false
  offset = 0
  thread = false
  type = 39
FEATURE [Part::FeaturePython] Screw095  label="M3x8-Screw272"  # Fasteners workbench fastener (typed FeaturePython)
  Placement = pos=(-531.13,115.09,-605.65) rot=(0.57735,0.57735,-0.57735;2.0944rad)
  Visibility1 = true
  diameter = 1
  invert = false
  length = 1
  lengthCustom = 8
  matchOuter = false
  offset = 0
  thread = false
  type = 39
FEATURE [Part::FeaturePython] b_Nema_17_42A02C_v21_001_003  label="Nema 17 42A02C v21_ Nema 17 42A02C v2_004"  # a2plus imported part (geometry in sourceFile) (typed FeaturePython)
  Placement = pos=(-546.538,110.248,-590.076) rot=(0,0.707107,-0.707107;3.14159rad)
  Visibility1 = true
  a2p_Version = V0.1
  fixedPosition = false
  objectType = a2pPart
  sourceFile = ./OTS/OTS-0012_nema17-stepper.step
  sourcePart =  Nema 17 42A02C v2
  subassemblyImport = false
  timeLastImport = 1.64563e+09
  updateColors = true
FEATURE [Part::FeaturePython] Screw032  label="M5x10-Screw217"  # Fasteners workbench fastener (typed FeaturePython)
  Placement = pos=(-510.06,30.11,-606.44) rot=(1,0,0;3.14159rad)
  Visibility1 = true
  diameter = 6
  invert = false
  length = 1
  lengthCustom = 10
  matchOuter = false
  offset = 0
  thread = false
  type = 33
FEATURE [Part::FeaturePython] Screw033  label="M5x10-Screw218"  # Fasteners workbench fastener (typed FeaturePython)
  Placement = pos=(-510.06,30.11,-573.54) rot=(0,0,1;0rad)
  Visibility1 = true
  diameter = 6
  invert = false
  length = 1
  lengthCustom = 10
  matchOuter = false
  offset = 0
  thread = false
  type = 33
FEATURE [Part::FeaturePython] Screw034  label="M5x10-Screw219"  # Fasteners workbench fastener (typed FeaturePython)
  Placement = pos=(-510.06,115.05,-589.94) rot=(-1,0,0;1.5708rad)
  Visibility1 = true
  diameter = 6
  invert = false
  length = 1
  lengthCustom = 10
  matchOuter = false
  offset = 0
  thread = false
  type = 33
FEATURE [Part::FeaturePython] b_M5_tslot_nut1_001_007  label="M5-tslot-nut1_T_Slot_Nut_Dropin_M5 v1_008"  # a2plus imported part (geometry in sourceFile) (typed FeaturePython)
  Placement = pos=(-510.062,30.0846,-595.338) rot=(1,0,0;3.14159rad)
  Visibility1 = true
  a2p_Version = V0.1
  fixedPosition = false
  objectType = a2pPart
  sourceFile = ./FST/FST-0016_M5-tslot-nut.step
  sourcePart = T_Slot_Nut_Dropin_M5 v1
  subassemblyImport = false
  timeLastImport = 1.64563e+09
  updateColors = true
FEATURE [Part::FeaturePython] b_M5_tslot_nut1_001_006  label="M5-tslot-nut1_T_Slot_Nut_Dropin_M5 v1_007"  # a2plus imported part (geometry in sourceFile) (typed FeaturePython)
  Placement = pos=(-510.062,30.0846,-585.028) rot=(0,0,1;0rad)
  Visibility1 = true
  a2p_Version = V0.1
  fixedPosition = false
  objectType = a2pPart
  sourceFile = ./FST/FST-0016_M5-tslot-nut.step
  sourcePart = T_Slot_Nut_Dropin_M5 v1
  subassemblyImport = false
  timeLastImport = 1.64563e+09
  updateColors = true
FEATURE [Part::FeaturePython] b_M5_tslot_nut1_001_005  label="M5-tslot-nut1_T_Slot_Nut_Dropin_M5 v1_006"  # a2plus imported part (geometry in sourceFile) (typed FeaturePython)
  Placement = pos=(-510.062,105.175,-590.098) rot=(-1,0,0;1.5708rad)
  Visibility1 = true
  a2p_Version = V0.1
  fixedPosition = false
  objectType = a2pPart
  sourceFile = ./FST/FST-0016_M5-tslot-nut.step
  sourcePart = T_Slot_Nut_Dropin_M5 v1
  subassemblyImport = false
  timeLastImport = 1.64563e+09
  updateColors = true
FEATURE [App::DocumentObjectGroup] Group007  label="Back-Right-Leg"
  Group = -> [b_FDM_0004_back_right_leg_001_,b_Gates_2GT_20T_Toothed_Pulley1_001_003,Screw096,Screw093,Screw094,Screw095,b_Nema_17_42A02C_v21_001_003,Screw032,Screw033,Screw034,b_M5_tslot_nut1_001_007,b_M5_tslot_nut1_001_006,b_M5_tslot_nut1_001_005]
FEATURE [Part::FeaturePython] b_M5_tslot_nut1_001_028  label="M5-tslot-nut1_T_Slot_Nut_Dropin_M5 v1_029"  # a2plus imported part (geometry in sourceFile) (typed FeaturePython)
  Placement = pos=(-139.79,24.9946,-10.0282) rot=(0,0.707107,-0.707107;3.14159rad)
  Visibility1 = true
  a2p_Version = V0.1
  fixedPosition = false
  objectType = a2pPart
  sourceFile = ./FST/FST-0016_M5-tslot-nut.step
  sourcePart = T_Slot_Nut_Dropin_M5 v1
  subassemblyImport = false
  timeLastImport = 1.64563e+09
  updateColors = true
FEATURE [Part::FeaturePython] b_M5_tslot_nut1_001_029  label="M5-tslot-nut1_T_Slot_Nut_Dropin_M5 v1_030"  # a2plus imported part (geometry in sourceFile) (typed FeaturePython)
  Placement = pos=(-82.6716,24.9946,-10.0282) rot=(0,0.707107,-0.707107;3.14159rad)
  Visibility1 = true
  a2p_Version = V0.1
  fixedPosition = false
  objectType = a2pPart
  sourceFile = ./FST/FST-0016_M5-tslot-nut.step
  sourcePart = T_Slot_Nut_Dropin_M5 v1
  subassemblyImport = false
  timeLastImport = 1.64563e+09
  updateColors = true
FEATURE [Part::FeaturePython] Screw103  label="M5x10-Screw220"  # Fasteners workbench fastener (typed FeaturePython)
  Placement = pos=(-137.73,14.98,-9.98) rot=(1,0,0;1.5708rad)
  Visibility1 = true
  diameter = 6
  invert = false
  length = 1
  lengthCustom = 10
  matchOuter = false
  offset = 0
  thread = false
  type = 33
FEATURE [Part::FeaturePython] Screw104  label="M5x10-Screw221"  # Fasteners workbench fastener (typed FeaturePython)
  Placement = pos=(-82.71,14.98,-9.98) rot=(1,0,0;1.5708rad)
  Visibility1 = true
  diameter = 6
  invert = false
  length = 1
  lengthCustom = 10
  matchOuter = false
  offset = 0
  thread = false
  type = 33
FEATURE [Part::FeaturePython] b_M5_tslot_nut1_001_024  label="M5-tslot-nut1_T_Slot_Nut_Dropin_M5 v1_025"  # a2plus imported part (geometry in sourceFile) (typed FeaturePython)
  Placement = pos=(-441.862,24.9746,-589.918) rot=(1,0,0;1.5708rad)
  Visibility1 = true
  a2p_Version = V0.1
  fixedPosition = false
  objectType = a2pPart
  sourceFile = ./FST/FST-0016_M5-tslot-nut.step
  sourcePart = T_Slot_Nut_Dropin_M5 v1
  subassemblyImport = false
  timeLastImport = 1.64563e+09
  updateColors = true
FEATURE [Part::FeaturePython] b_M5_tslot_nut1_001_025  label="M5-tslot-nut1_T_Slot_Nut_Dropin_M5 v1_026"  # a2plus imported part (geometry in sourceFile) (typed FeaturePython)
  Placement = pos=(-456.992,9.95457,-589.918) rot=(0.707107,0,0.707107;3.14159rad)
  Visibility1 = true
  a2p_Version = V0.1
  fixedPosition = false
  objectType = a2pPart
  sourceFile = ./FST/FST-0016_M5-tslot-nut.step
  sourcePart = T_Slot_Nut_Dropin_M5 v1
  subassemblyImport = false
  timeLastImport = 1.64563e+09
  updateColors = true
FEATURE [Part::FeaturePython] b_M5_tslot_nut1_001_026  label="M5-tslot-nut1_T_Slot_Nut_Dropin_M5 v1_027"  # a2plus imported part (geometry in sourceFile) (typed FeaturePython)
  Placement = pos=(-466.842,9.95457,-589.918) rot=(0,-1,0;1.5708rad)
  Visibility1 = true
  a2p_Version = V0.1
  fixedPosition = false
  objectType = a2pPart
  sourceFile = ./FST/FST-0016_M5-tslot-nut.step
  sourcePart = T_Slot_Nut_Dropin_M5 v1
  subassemblyImport = false
  timeLastImport = 1.64563e+09
  updateColors = true
FEATURE [Part::FeaturePython] b_M5_tslot_nut1_001_027  label="M5-tslot-nut1_T_Slot_Nut_Dropin_M5 v1_028"  # a2plus imported part (geometry in sourceFile) (typed FeaturePython)
  Placement = pos=(-481.962,25.0246,-589.918) rot=(0,0.707107,-0.707107;3.14159rad)
  Visibility1 = true
  a2p_Version = V0.1
  fixedPosition = false
  objectType = a2pPart
  sourceFile = ./FST/FST-0016_M5-tslot-nut.step
  sourcePart = T_Slot_Nut_Dropin_M5 v1
  subassemblyImport = false
  timeLastImport = 1.64563e+09
  updateColors = true
FEATURE [Part::FeaturePython] Screw081  label="M5x8-Screw085"  # Fasteners workbench fastener (typed FeaturePython)
  Placement = pos=(-474.99,9.91,-589.97) rot=(0,-1,0;1.5708rad)
  Visibility1 = true
  diameter = 3
  invert = false
  length = 0
  lengthCustom = 8
  matchOuter = false
  offset = 0
  thread = false
  type = 39
FEATURE [Part::FeaturePython] Screw082  label="M5x8-Screw086"  # Fasteners workbench fastener (typed FeaturePython)
  Placement = pos=(-448.83,9.91,-589.97) rot=(0.707107,0,0.707107;3.14159rad)
  Visibility1 = true
  diameter = 3
  invert = false
  length = 0
  lengthCustom = 8
  matchOuter = false
  offset = 0
  thread = false
  type = 39
FEATURE [Part::FeaturePython] Screw083  label="M5x8-Screw087"  # Fasteners workbench fastener (typed FeaturePython)
  Placement = pos=(-441.8,16.93,-589.88) rot=(0.57735,-0.57735,0.57735;2.0944rad)
  Visibility1 = true
  diameter = 3
  invert = false
  length = 0
  lengthCustom = 8
  matchOuter = false
  offset = 0
  thread = false
  type = 39
FEATURE [Part::FeaturePython] Screw084  label="M5x8-Screw088"  # Fasteners workbench fastener (typed FeaturePython)
  Placement = pos=(-481.98,16.93,-589.88) rot=(0.57735,-0.57735,0.57735;2.0944rad)
  Visibility1 = true
  diameter = 3
  invert = false
  length = 0
  lengthCustom = 8
  matchOuter = false
  offset = 0
  thread = false
  type = 39
FEATURE [Part::FeaturePython] Screw077  label="M5x8-Screw089"  # Fasteners workbench fastener (typed FeaturePython)
  Placement = pos=(-474.99,9.97,-10.02) rot=(0,-1,0;1.5708rad)
  Visibility1 = true
  diameter = 3
  invert = false
  length = 0
  lengthCustom = 8
  matchOuter = false
  offset = 0
  thread = false
  type = 39
FEATURE [Part::FeaturePython] Screw078  label="M5x8-Screw090"  # Fasteners workbench fastener (typed FeaturePython)
  Placement = pos=(-482.04,16.85,-10.02) rot=(0.57735,-0.57735,0.57735;2.0944rad)
  Visibility1 = true
  diameter = 3
  invert = false
  length = 0
  lengthCustom = 8
  matchOuter = false
  offset = 0
  thread = false
  type = 39
FEATURE [Part::FeaturePython] Screw079  label="M5x8-Screw091"  # Fasteners workbench fastener (typed FeaturePython)
  Placement = pos=(-442,16.85,-10.02) rot=(0.57735,-0.57735,0.57735;2.0944rad)
  Visibility1 = true
  diameter = 3
  invert = false
  length = 0
  lengthCustom = 8
  matchOuter = false
  offset = 0
  thread = false
  type = 39
FEATURE [Part::FeaturePython] Screw080  label="M5x8-Screw092"  # Fasteners workbench fastener (typed FeaturePython)
  Placement = pos=(-448.9,9.98,-10.02) rot=(0.707107,0,0.707107;3.14159rad)
  Visibility1 = true
  diameter = 3
  invert = false
  length = 0
  lengthCustom = 8
  matchOuter = false
  offset = 0
  thread = false
  type = 39
FEATURE [Part::FeaturePython] b_M5_tslot_nut1_001_020  label="M5-tslot-nut1_T_Slot_Nut_Dropin_M5 v1_021"  # a2plus imported part (geometry in sourceFile) (typed FeaturePython)
  Placement = pos=(-456.952,9.95457,-9.70821) rot=(0,1,0;1.5708rad)
  Visibility1 = true
  a2p_Version = V0.1
  fixedPosition = false
  objectType = a2pPart
  sourceFile = ./FST/FST-0016_M5-tslot-nut.step
  sourcePart = T_Slot_Nut_Dropin_M5 v1
  subassemblyImport = false
  timeLastImport = 1.64563e+09
  updateColors = true
FEATURE [Part::FeaturePython] b_M5_tslot_nut1_001_021  label="M5-tslot-nut1_T_Slot_Nut_Dropin_M5 v1_022"  # a2plus imported part (geometry in sourceFile) (typed FeaturePython)
  Placement = pos=(-466.872,9.95457,-9.70821) rot=(0.707107,0,-0.707107;3.14159rad)
  Visibility1 = true
  a2p_Version = V0.1
  fixedPosition = false
  objectType = a2pPart
  sourceFile = ./FST/FST-0016_M5-tslot-nut.step
  sourcePart = T_Slot_Nut_Dropin_M5 v1
  subassemblyImport = false
  timeLastImport = 1.64563e+09
  updateColors = true
FEATURE [Part::FeaturePython] b_M5_tslot_nut1_001_022  label="M5-tslot-nut1_T_Slot_Nut_Dropin_M5 v1_023"  # a2plus imported part (geometry in sourceFile) (typed FeaturePython)
  Placement = pos=(-482.042,25.1246,-9.70821) rot=(1,0,0;1.5708rad)
  Visibility1 = true
  a2p_Version = V0.1
  fixedPosition = false
  objectType = a2pPart
  sourceFile = ./FST/FST-0016_M5-tslot-nut.step
  sourcePart = T_Slot_Nut_Dropin_M5 v1
  subassemblyImport = false
  timeLastImport = 1.64563e+09
  updateColors = true
FEATURE [Part::FeaturePython] b_M5_tslot_nut1_001_023  label="M5-tslot-nut1_T_Slot_Nut_Dropin_M5 v1_024"  # a2plus imported part (geometry in sourceFile) (typed FeaturePython)
  Placement = pos=(-441.942,25.1246,-9.70821) rot=(1,0,0;1.5708rad)
  Visibility1 = true
  a2p_Version = V0.1
  fixedPosition = false
  objectType = a2pPart
  sourceFile = ./FST/FST-0016_M5-tslot-nut.step
  sourcePart = T_Slot_Nut_Dropin_M5 v1
  subassemblyImport = false
  timeLastImport = 1.64563e+09
  updateColors = true
FEATURE [Part::FeaturePython] b_2020CornerBracket1_001_002  label="2020CornerBracket1_FusionComponent_003"  # a2plus imported part (geometry in sourceFile) (typed FeaturePython)
  Placement = pos=(-472.055,19.9154,-580.008) rot=(0.57735,-0.57735,0.57735;2.0944rad)
  Visibility1 = true
  a2p_Version = V0.1
  fixedPosition = false
  objectType = a2pPart
  sourceFile = ./OTS/OTS-0015_20x20-corner-bracket.step
  sourcePart = FusionComponent
  subassemblyImport = false
  timeLastImport = 1.64563e+09
  updateColors = true
FEATURE [Part::FeaturePython] b_2020CornerBracket1_001_003  label="2020CornerBracket1_FusionComponent_004"  # a2plus imported part (geometry in sourceFile) (typed FeaturePython)
  Placement = pos=(-451.845,19.9154,-599.918) rot=(0.57735,0.57735,-0.57735;2.0944rad)
  Visibility1 = true
  a2p_Version = V0.1
  fixedPosition = false
  objectType = a2pPart
  sourceFile = ./OTS/OTS-0015_20x20-corner-bracket.step
  sourcePart = FusionComponent
  subassemblyImport = false
  timeLastImport = 1.64563e+09
  updateColors = true
FEATURE [Part::FeaturePython] b_2020CornerBracket1_001_004  label="2020CornerBracket1_FusionComponent_005"  # a2plus imported part (geometry in sourceFile) (typed FeaturePython)
  Placement = pos=(-451.845,19.9154,-20.0179) rot=(0.57735,0.57735,-0.57735;2.0944rad)
  Visibility1 = true
  a2p_Version = V0.1
  fixedPosition = false
  objectType = a2pPart
  sourceFile = ./OTS/OTS-0015_20x20-corner-bracket.step
  sourcePart = FusionComponent
  subassemblyImport = false
  timeLastImport = 1.64563e+09
  updateColors = true
FEATURE [Part::FeaturePython] b_2020CornerBracket1_001_005  label="2020CornerBracket1_FusionComponent_006"  # a2plus imported part (geometry in sourceFile) (typed FeaturePython)
  Placement = pos=(-472.055,19.9154,-0.00786224) rot=(0.57735,-0.57735,0.57735;2.0944rad)
  Visibility1 = true
  a2p_Version = V0.1
  fixedPosition = false
  objectType = a2pPart
  sourceFile = ./OTS/OTS-0015_20x20-corner-bracket.step
  sourcePart = FusionComponent
  subassemblyImport = false
  timeLastImport = 1.64563e+09
  updateColors = true
FEATURE [Part::FeaturePython] b_OTS_0009_20x20_v_slot_600mm1_001_006  label="OTS-0009_20x20_v_slot_600mm1_20x20_v_slot_600mm v2_007"  # a2plus imported part (geometry in sourceFile) (typed FeaturePython)
  Placement = pos=(-471.91,0,0) rot=(0,0,1;0rad)
  Visibility1 = true
  a2p_Version = V0.1
  fixedPosition = true
  objectType = a2pPart
  sourceFile = ./OTS/OTS-0010_20x20-v-slot-600mm.step
  sourcePart = 20x20_v_slot_600mm v2
  subassemblyImport = false
  timeLastImport = 1.64563e+09
  updateColors = true
FEATURE [Part::FeaturePython] b_2020CornerBracket1_001_001  label="2020CornerBracket1_FusionComponent_002"  # a2plus imported part (geometry in sourceFile) (typed FeaturePython)
  Placement = pos=(-0.0247107,19.9154,-580.008) rot=(0.57735,-0.57735,0.57735;2.0944rad)
  Visibility1 = true
  a2p_Version = V0.1
  fixedPosition = false
  objectType = a2pPart
  sourceFile = ./OTS/OTS-0015_20x20-corner-bracket.step
  sourcePart = FusionComponent
  subassemblyImport = false
  timeLastImport = 1.64563e+09
  updateColors = true
FEATURE [Part::FeaturePython] Screw073  label="M5x8-Screw093"  # Fasteners workbench fastener (typed FeaturePython)
  Placement = pos=(-3.07,9.97,-10.02) rot=(0,-1,0;1.5708rad)
  Visibility1 = true
  diameter = 3
  invert = false
  length = 0
  lengthCustom = 8
  matchOuter = false
  offset = 0
  thread = false
  type = 39
FEATURE [Part::FeaturePython] Screw074  label="M5x8-Screw"  # Fasteners workbench fastener (typed FeaturePython)
  Placement = pos=(-10.13,17.05,-10.02) rot=(0.57735,-0.57735,0.57735;2.0944rad)
  Visibility1 = true
  diameter = 3
  invert = false
  length = 0
  lengthCustom = 8
  matchOuter = false
  offset = 0
  thread = false
  type = 39
FEATURE [Part::FeaturePython] b_2020CornerBracket1_001_  label="2020CornerBracket1_FusionComponent_001"  # a2plus imported part (geometry in sourceFile) (typed FeaturePython)
  Placement = pos=(-0.0247107,20.0654,0.0521378) rot=(0.57735,-0.57735,0.57735;2.0944rad)
  Visibility1 = true
  a2p_Version = V0.1
  fixedPosition = false
  objectType = a2pPart
  sourceFile = ./OTS/OTS-0015_20x20-corner-bracket.step
  sourcePart = FusionComponent
  subassemblyImport = false
  timeLastImport = 1.64563e+09
  updateColors = true
FEATURE [Part::FeaturePython] b_M5_tslot_nut1_001_016  label="M5-tslot-nut1_T_Slot_Nut_Dropin_M5 v1_017"  # a2plus imported part (geometry in sourceFile) (typed FeaturePython)
  Placement = pos=(4.9684,9.95457,-9.85821) rot=(0.707107,0,-0.707107;3.14159rad)
  Visibility1 = true
  a2p_Version = V0.1
  fixedPosition = false
  objectType = a2pPart
  sourceFile = ./FST/FST-0016_M5-tslot-nut.step
  sourcePart = T_Slot_Nut_Dropin_M5 v1
  subassemblyImport = false
  timeLastImport = 1.64563e+09
  updateColors = true
FEATURE [Part::FeaturePython] b_M5_tslot_nut1_001_017  label="M5-tslot-nut1_T_Slot_Nut_Dropin_M5 v1_018"  # a2plus imported part (geometry in sourceFile) (typed FeaturePython)
  Placement = pos=(-10.1416,24.9946,-10.0282) rot=(0,0.707107,-0.707107;3.14159rad)
  Visibility1 = true
  a2p_Version = V0.1
  fixedPosition = false
  objectType = a2pPart
  sourceFile = ./FST/FST-0016_M5-tslot-nut.step
  sourcePart = T_Slot_Nut_Dropin_M5 v1
  subassemblyImport = false
  timeLastImport = 1.64563e+09
  updateColors = true
FEATURE [Part::FeaturePython] Screw075  label="M5x8-Screw094"  # Fasteners workbench fastener (typed FeaturePython)
  Placement = pos=(-3.07,9.97,-589.77) rot=(0,-1,0;1.5708rad)
  Visibility1 = true
  diameter = 3
  invert = false
  length = 0
  lengthCustom = 8
  matchOuter = false
  offset = 0
  thread = false
  type = 39
FEATURE [Part::FeaturePython] Screw076  label="M5x8-Screw095"  # Fasteners workbench fastener (typed FeaturePython)
  Placement = pos=(-9.87,16.9,-589.89) rot=(0.57735,-0.57735,0.57735;2.0944rad)
  Visibility1 = true
  diameter = 3
  invert = false
  length = 0
  lengthCustom = 8
  matchOuter = false
  offset = 0
  thread = false
  type = 39
FEATURE [Part::FeaturePython] b_M5_tslot_nut1_001_018  label="M5-tslot-nut1_T_Slot_Nut_Dropin_M5 v1_019"  # a2plus imported part (geometry in sourceFile) (typed FeaturePython)
  Placement = pos=(4.9684,9.95457,-589.718) rot=(0.707107,0,-0.707107;3.14159rad)
  Visibility1 = true
  a2p_Version = V0.1
  fixedPosition = false
  objectType = a2pPart
  sourceFile = ./FST/FST-0016_M5-tslot-nut.step
  sourcePart = T_Slot_Nut_Dropin_M5 v1
  subassemblyImport = false
  timeLastImport = 1.64563e+09
  updateColors = true
FEATURE [Part::FeaturePython] b_M5_tslot_nut1_001_019  label="M5-tslot-nut1_T_Slot_Nut_Dropin_M5 v1_020"  # a2plus imported part (geometry in sourceFile) (typed FeaturePython)
  Placement = pos=(-10.0016,24.5446,-589.718) rot=(0,0.707107,-0.707107;3.14159rad)
  Visibility1 = true
  a2p_Version = V0.1
  fixedPosition = false
  objectType = a2pPart
  sourceFile = ./FST/FST-0016_M5-tslot-nut.step
  sourcePart = T_Slot_Nut_Dropin_M5 v1
  subassemblyImport = false
  timeLastImport = 1.64563e+09
  updateColors = true
FEATURE [Part::FeaturePython] b_OTS_0009_20x20_v_slot_600mm1_001_002  label="OTS-0009_20x20_v_slot_600mm1_20x20_v_slot_600mm v2_003"  # a2plus imported part (geometry in sourceFile) (typed FeaturePython)
  Placement = pos=(79.9716,90.0176,0.00959473) rot=(0,1,0;1.5708rad)
  Visibility1 = true
  a2p_Version = V0.1
  fixedPosition = false
  objectType = a2pPart
  sourceFile = ./OTS/OTS-0010_20x20-v-slot-600mm.step
  sourcePart = 20x20_v_slot_600mm v2
  subassemblyImport = false
  timeLastImport = 1.64563e+09
  updateColors = true
FEATURE [Part::FeaturePython] b_OTS_0009_20x20_v_slot_600mm1_001_004  label="OTS-0009_20x20_v_slot_600mm1_20x20_v_slot_600mm v2_005"  # a2plus imported part (geometry in sourceFile) (typed FeaturePython)
  Placement = pos=(79.9849,20.0043,-580.068) rot=(0,1,0;1.5708rad)
  Visibility1 = true
  a2p_Version = V0.1
  fixedPosition = false
  objectType = a2pPart
  sourceFile = ./OTS/OTS-0010_20x20-v-slot-600mm.step
  sourcePart = 20x20_v_slot_600mm v2
  subassemblyImport = false
  timeLastImport = 1.64563e+09
  updateColors = true
FEATURE [Part::FeaturePython] b_OTS_0009_20x20_v_slot_600mm1_001_005  label="OTS-0009_20x20_v_slot_600mm1_20x20_v_slot_600mm v2_006"  # a2plus imported part (geometry in sourceFile) (typed FeaturePython)
  Placement = pos=(79.9481,90.0477,-580.088) rot=(0,1,0;1.5708rad)
  Visibility1 = true
  a2p_Version = V0.1
  fixedPosition = false
  objectType = a2pPart
  sourceFile = ./OTS/OTS-0010_20x20-v-slot-600mm.step
  sourcePart = 20x20_v_slot_600mm v2
  subassemblyImport = false
  timeLastImport = 1.64563e+09
  updateColors = true
FEATURE [Part::FeaturePython] b_OTS_0009_20x20_v_slot_600mm1_001_001  label="OTS-0009_20x20_v_slot_600mm1_20x20_v_slot_600mm v2_002"  # a2plus imported part (geometry in sourceFile) (typed FeaturePython)
  Placement = pos=(80.0926,20.0674,0.0637482) rot=(0,1,0;1.5708rad)
  Visibility1 = true
  a2p_Version = V0.1
  fixedPosition = false
  objectType = a2pPart
  sourceFile = ./OTS/OTS-0010_20x20-v-slot-600mm.step
  sourcePart = 20x20_v_slot_600mm v2
  subassemblyImport = false
  timeLastImport = 1.64563e+09
  updateColors = true
FEATURE [Part::FeaturePython] b_OTS_0009_20x20_v_slot_600mm1_001_  label="OTS-0009_20x20_v_slot_600mm1_20x20_v_slot_600mm v2_001"  # a2plus imported part (geometry in sourceFile) (typed FeaturePython)
  Visibility1 = true
  a2p_Version = V0.1
  fixedPosition = true
  objectType = a2pPart
  sourceFile = ./OTS/OTS-0010_20x20-v-slot-600mm.step
  sourcePart = 20x20_v_slot_600mm v2
  subassemblyImport = false
  timeLastImport = 1.64563e+09
  updateColors = true
FEATURE [Part::FeaturePython] b_FDM_0022_umbilical_guide_001_  label="FDM-0022_umbilical-guide_Body_001"  # a2plus imported part (geometry in sourceFile) (typed FeaturePython)
  Placement = pos=(-111.205,19.9983,-10.0067) rot=(1,0,0;3.14159rad)
  Visibility1 = true
  a2p_Version = V0.1
  fixedPosition = false
  objectType = a2pPart
  sourceFile = ./FDM/FDM-0022_umbilical-guide.FCStd
  sourcePart = Body
  subassemblyImport = false
  timeLastImport = 1.64563e+09
  updateColors = true
FEATURE [Part::FeaturePython] b_FDM_0019_up_light_mount_001_  label="FDM-0019_up-light-mount_Body_001"  # a2plus imported part (geometry in sourceFile) (typed FeaturePython)
  Placement = pos=(-103.979,32.2367,-300.398) rot=(0.57735,-0.57735,0.57735;2.0944rad)
  Visibility1 = true
  a2p_Version = V0.1
  fixedPosition = false
  objectType = a2pPart
  sourceFile = ./FDM/FDM-0019_up-light-mount.FCStd
  sourcePart = Body
  subassemblyImport = false
  timeLastImport = 1.64677e+09
  updateColors = true
FEATURE [Part::FeaturePython] b_FDM_0020_up_camera_mount_001_  label="FDM-0020_up-camera-mount_Body_001"  # a2plus imported part (geometry in sourceFile) (typed FeaturePython)
  Placement = pos=(-104.009,18.7487,-300.369) rot=(0.57735,-0.57735,-0.57735;4.18879rad)
  Visibility1 = true
  a2p_Version = V0.1
  fixedPosition = false
  objectType = a2pPart
  sourceFile = ./FDM/FDM-0020_up-camera-mount.FCStd
  sourcePart = Body
  subassemblyImport = false
  timeLastImport = 1.64563e+09
  updateColors = true
FEATURE [Part::FeaturePython] Screw174  label="M3x30-Screw062"  # Fasteners workbench fastener (typed FeaturePython)
  Placement = pos=(-74.04,43.1,-300.41) rot=(-1,0,0;1.5708rad)
  Visibility1 = true
  diameter = 4
  invert = false
  length = 9
  lengthCustom = 30
  matchOuter = false
  offset = 0
  thread = false
  type = 33
FEATURE [Part::FeaturePython] Screw175  label="M3x30-Screw063"  # Fasteners workbench fastener (typed FeaturePython)
  Placement = pos=(-134.05,43.1,-300.41) rot=(-1,0,0;1.5708rad)
  Visibility1 = true
  diameter = 4
  invert = false
  length = 9
  lengthCustom = 30
  matchOuter = false
  offset = 0
  thread = false
  type = 33
FEATURE [Part::FeaturePython] Screw176  label="M3x30-Screw064"  # Fasteners workbench fastener (typed FeaturePython)
  Placement = pos=(-104.04,43.1,-330.33) rot=(-1,0,0;1.5708rad)
  Visibility1 = true
  diameter = 4
  invert = false
  length = 9
  lengthCustom = 30
  matchOuter = false
  offset = 0
  thread = false
  type = 33
FEATURE [Part::FeaturePython] Screw177  label="M3x30-Screw065"  # Fasteners workbench fastener (typed FeaturePython)
  Placement = pos=(-104,43.1,-270.39) rot=(-1,0,0;1.5708rad)
  Visibility1 = true
  diameter = 4
  invert = false
  length = 9
  lengthCustom = 30
  matchOuter = false
  offset = 0
  thread = false
  type = 33
FEATURE [Part::FeaturePython] Nut052  label="M3-Nut205"  # Fasteners workbench fastener (typed FeaturePython)
  Placement = pos=(-74.0612,15.97,-300.387) rot=(1,0,0;1.5708rad)
  Visibility1 = true
  diameter = 4
  invert = false
  matchOuter = false
  offset = 0
  thread = false
  type = 7
FEATURE [Part::FeaturePython] Nut053  label="M3-Nut206"  # Fasteners workbench fastener (typed FeaturePython)
  Placement = pos=(-104.031,16.27,-270.417) rot=(0.57735,0.57735,-0.57735;2.0944rad)
  Visibility1 = true
  diameter = 4
  invert = false
  matchOuter = false
  offset = 0
  thread = false
  type = 7
FEATURE [Part::FeaturePython] Nut054  label="M3-Nut207"  # Fasteners workbench fastener (typed FeaturePython)
  Placement = pos=(-104.031,16.2,-330.287) rot=(0.57735,0.57735,-0.57735;2.0944rad)
  Visibility1 = true
  diameter = 4
  invert = false
  matchOuter = false
  offset = 0
  thread = false
  type = 7
FEATURE [Part::FeaturePython] Nut055  label="M3-Nut208"  # Fasteners workbench fastener (typed FeaturePython)
  Placement = pos=(-134.051,16.05,-300.387) rot=(1,0,0;1.5708rad)
  Visibility1 = true
  diameter = 4
  invert = false
  matchOuter = false
  offset = 0
  thread = false
  type = 7
FEATURE [Part::FeaturePython] Screw139  label="M3x10-Screw051"  # Fasteners workbench fastener (typed FeaturePython)
  Placement = pos=(-148.95,42.98,-465.5) rot=(0.57735,-0.57735,-0.57735;4.18879rad)
  Visibility1 = true
  diameter = 1
  invert = false
  length = 2
  lengthCustom = 10
  matchOuter = false
  offset = 0
  thread = false
  type = 39
FEATURE [Part::FeaturePython] Screw142  label="M3x10-Screw050"  # Fasteners workbench fastener (typed FeaturePython)
  Placement = pos=(-148.95,42.98,-495.4) rot=(0.57735,-0.57735,-0.57735;4.18879rad)
  Visibility1 = true
  diameter = 1
  invert = false
  length = 2
  lengthCustom = 10
  matchOuter = false
  offset = 0
  thread = false
  type = 39
FEATURE [Part::FeaturePython] Nut057  label="M3-Nut243"  # Fasteners workbench fastener (typed FeaturePython)
  Placement = pos=(-148.95,35.75,-495.5) rot=(0.57735,0.57735,-0.57735;2.0944rad)
  Visibility1 = true
  diameter = 4
  invert = false
  matchOuter = false
  offset = 0
  thread = false
  type = 7
FEATURE [Part::FeaturePython] Nut058  label="M3-Nut244"  # Fasteners workbench fastener (typed FeaturePython)
  Placement = pos=(-148.95,35.75,-465.6) rot=(0.57735,0.57735,-0.57735;2.0944rad)
  Visibility1 = true
  diameter = 4
  invert = false
  matchOuter = false
  offset = 0
  thread = false
  type = 7
FEATURE [Part::FeaturePython] Screw178  label="M5x8-Screw104"  # Fasteners workbench fastener (typed FeaturePython)
  Placement = pos=(-54.33,43.32,-10.02) rot=(0.57735,0.57735,0.57735;4.18879rad)
  Visibility1 = true
  diameter = 3
  invert = false
  length = 0
  lengthCustom = 8
  matchOuter = false
  offset = 0
  thread = false
  type = 39
FEATURE [Part::FeaturePython] Screw179  label="M5x8-Screw105"  # Fasteners workbench fastener (typed FeaturePython)
  Placement = pos=(-153.93,43.19,-10.14) rot=(0.57735,0.57735,0.57735;4.18879rad)
  Visibility1 = true
  diameter = 3
  invert = false
  length = 0
  lengthCustom = 8
  matchOuter = false
  offset = 0
  thread = false
  type = 39
FEATURE [Part::FeaturePython] Screw180  label="M5x8-Screw106"  # Fasteners workbench fastener (typed FeaturePython)
  Placement = pos=(-153.93,43.19,-590.11) rot=(0.57735,0.57735,0.57735;4.18879rad)
  Visibility1 = true
  diameter = 3
  invert = false
  length = 0
  lengthCustom = 8
  matchOuter = false
  offset = 0
  thread = false
  type = 39
FEATURE [Part::FeaturePython] Screw134  label="M5x8-Screw107"  # Fasteners workbench fastener (typed FeaturePython)
  Placement = pos=(-54.35,43.19,-590.11) rot=(0.57735,0.57735,0.57735;4.18879rad)
  Visibility1 = true
  diameter = 3
  invert = false
  length = 0
  lengthCustom = 8
  matchOuter = false
  offset = 0
  thread = false
  type = 39
FEATURE [Part::FeaturePython] b_FDM_0024_nozzle_holder_001_  label="FDM-0024_nozzle-holder_Body_001"  # a2plus imported part (geometry in sourceFile) (typed FeaturePython)
  Placement = pos=(-141.955,42.9477,-115.208) rot=(0,1,0;1.5708rad)
  a2p_Version = V0.1
  fixedPosition = false
  objectType = a2pPart
  sourceFile = ./FDM/FDM-0024_nozzle-holder.FCStd
  sourcePart = Body
  subassemblyImport = false
  timeLastImport = 1.64563e+09
  updateColors = true
FEATURE [Part::FeaturePython] Nut064  label="M3-Nut269"  # Fasteners workbench fastener (typed FeaturePython)
  Placement = pos=(-73.9412,47.93,-120) rot=(0.57735,0.57735,-0.57735;2.0944rad)
  Visibility1 = true
  diameter = 4
  invert = false
  matchOuter = false
  offset = 0
  thread = false
  type = 7
FEATURE [Part::FeaturePython] Nut065  label="M3-Nut270"  # Fasteners workbench fastener (typed FeaturePython)
  Placement = pos=(-103.951,47.93,-120) rot=(0.57735,0.57735,-0.57735;2.0944rad)
  Visibility1 = true
  diameter = 4
  invert = false
  matchOuter = false
  offset = 0
  thread = false
  type = 7
FEATURE [Part::FeaturePython] Nut066  label="M3-Nut271"  # Fasteners workbench fastener (typed FeaturePython)
  Placement = pos=(-133.981,47.93,-120) rot=(0.57735,0.57735,-0.57735;2.0944rad)
  Visibility1 = true
  diameter = 4
  invert = false
  matchOuter = false
  offset = 0
  thread = false
  type = 7
FEATURE [Part::FeaturePython] Screw156  label="M3x8-Screw301"  # Fasteners workbench fastener (typed FeaturePython)
  Placement = pos=(-73.95,39.94,-120) rot=(0.57735,-0.57735,0.57735;2.0944rad)
  Visibility1 = true
  diameter = 1
  invert = false
  length = 1
  lengthCustom = 8
  matchOuter = false
  offset = 0
  thread = false
  type = 39
FEATURE [Part::FeaturePython] Screw157  label="M3x8-Screw302"  # Fasteners workbench fastener (typed FeaturePython)
  Placement = pos=(-103.97,39.94,-120) rot=(0.57735,-0.57735,0.57735;2.0944rad)
  Visibility1 = true
  diameter = 1
  invert = false
  length = 1
  lengthCustom = 8
  matchOuter = false
  offset = 0
  thread = false
  type = 39
FEATURE [Part::FeaturePython] Screw158  label="M3x8-Screw303"  # Fasteners workbench fastener (typed FeaturePython)
  Placement = pos=(-133.99,39.94,-120) rot=(0.57735,-0.57735,0.57735;2.0944rad)
  Visibility1 = true
  diameter = 1
  invert = false
  length = 1
  lengthCustom = 8
  matchOuter = false
  offset = 0
  thread = false
  type = 39
FEATURE [Part::FeaturePython] b_OTS_0002_00_usb_webcam_001_001  label="OTS-0002-00_usb-webcam_Body_002"  # a2plus imported part (geometry in sourceFile) (typed FeaturePython)
  Placement = pos=(-104.103,22.2002,-299.834) rot=(0.57735,0.57735,0.57735;4.18879rad)
  Visibility1 = true
  a2p_Version = V0.1
  fixedPosition = false
  objectType = a2pPart
  sourceFile = ./OTS/OTS-0002-00_usb-webcam.FCStd
  sourcePart = Body
  subassemblyImport = false
  timeLastImport = 1.64563e+09
  updateColors = true
FEATURE [Part::FeaturePython] Screw159  label="M2.5x8-Screw059"  # Fasteners workbench fastener (typed FeaturePython)
  Placement = pos=(-118.1,20.61,-313.87) rot=(0,0.707107,-0.707107;3.14159rad)
  Visibility1 = true
  diameter = 3
  invert = false
  length = 3
  lengthCustom = 8
  matchOuter = false
  offset = 0
  thread = false
  type = 33
FEATURE [Part::FeaturePython] Screw160  label="M2.5x8-Screw060"  # Fasteners workbench fastener (typed FeaturePython)
  Placement = pos=(-118.1,20.61,-285.89) rot=(0,0.707107,-0.707107;3.14159rad)
  Visibility1 = true
  diameter = 3
  invert = false
  length = 3
  lengthCustom = 8
  matchOuter = false
  offset = 0
  thread = false
  type = 33
FEATURE [Part::FeaturePython] Screw161  label="M2.5x8-Screw061"  # Fasteners workbench fastener (typed FeaturePython)
  Placement = pos=(-90.09,20.61,-285.89) rot=(0,0.707107,-0.707107;3.14159rad)
  Visibility1 = true
  diameter = 3
  invert = false
  length = 3
  lengthCustom = 8
  matchOuter = false
  offset = 0
  thread = false
  type = 33
FEATURE [Part::FeaturePython] Screw162  label="M2.5x8-Screw062"  # Fasteners workbench fastener (typed FeaturePython)
  Placement = pos=(-90.09,20.61,-313.87) rot=(0,0.707107,-0.707107;3.14159rad)
  Visibility1 = true
  diameter = 3
  invert = false
  length = 3
  lengthCustom = 8
  matchOuter = false
  offset = 0
  thread = false
  type = 33
FEATURE [Part::FeaturePython] b_CSM_0001_staging_plate_001_  label="CSM-0001_staging-plate_Body_001"  # a2plus imported part (geometry in sourceFile) (typed FeaturePython)
  Placement = pos=(-163.951,42.9729,-0.410743) rot=(0.57735,0.57735,-0.57735;2.0944rad)
  Visibility1 = true
  a2p_Version = V0.1
  fixedPosition = false
  objectType = a2pPart
  sourceFile = ./CSM/CSM-0001_staging-plate.FCStd
  sourcePart = Body
  subassemblyImport = false
  timeLastImport = 1.64563e+09
  updateColors = true
FEATURE [Part::FeaturePython] b_M5_tslot_nut1_001_030  label="M5-tslot-nut1_T_Slot_Nut_Dropin_M5 v1_031"  # a2plus imported part (geometry in sourceFile) (typed FeaturePython)
  Placement = pos=(-54.2216,34.9746,-589.718) rot=(0,0.707107,0.707107;3.14159rad)
  Visibility1 = true
  a2p_Version = V0.1
  fixedPosition = false
  objectType = a2pPart
  sourceFile = ./FST/FST-0016_M5-tslot-nut.step
  sourcePart = T_Slot_Nut_Dropin_M5 v1
  subassemblyImport = false
  timeLastImport = 1.64563e+09
  updateColors = true
FEATURE [Part::FeaturePython] b_M5_tslot_nut1_001_031  label="M5-tslot-nut1_T_Slot_Nut_Dropin_M5 v1_032"  # a2plus imported part (geometry in sourceFile) (typed FeaturePython)
  Placement = pos=(-153.872,34.9746,-589.718) rot=(0,0.707107,0.707107;3.14159rad)
  Visibility1 = true
  a2p_Version = V0.1
  fixedPosition = false
  objectType = a2pPart
  sourceFile = ./FST/FST-0016_M5-tslot-nut.step
  sourcePart = T_Slot_Nut_Dropin_M5 v1
  subassemblyImport = false
  timeLastImport = 1.64563e+09
  updateColors = true
FEATURE [Part::FeaturePython] b_M5_tslot_nut1_001_032  label="M5-tslot-nut1_T_Slot_Nut_Dropin_M5 v1_033"  # a2plus imported part (geometry in sourceFile) (typed FeaturePython)
  Placement = pos=(-153.872,34.9746,-9.85821) rot=(0,0.707107,0.707107;3.14159rad)
  Visibility1 = true
  a2p_Version = V0.1
  fixedPosition = false
  objectType = a2pPart
  sourceFile = ./FST/FST-0016_M5-tslot-nut.step
  sourcePart = T_Slot_Nut_Dropin_M5 v1
  subassemblyImport = false
  timeLastImport = 1.64563e+09
  updateColors = true
FEATURE [Part::FeaturePython] b_M5_tslot_nut1_001_033  label="M5-tslot-nut1_T_Slot_Nut_Dropin_M5 v1_034"  # a2plus imported part (geometry in sourceFile) (typed FeaturePython)
  Placement = pos=(-54.2716,34.9746,-9.85821) rot=(0,0.707107,0.707107;3.14159rad)
  Visibility1 = true
  a2p_Version = V0.1
  fixedPosition = false
  objectType = a2pPart
  sourceFile = ./FST/FST-0016_M5-tslot-nut.step
  sourcePart = T_Slot_Nut_Dropin_M5 v1
  subassemblyImport = false
  timeLastImport = 1.64563e+09
  updateColors = true
FEATURE [Part::FeaturePython] b_OTS_0003_00_vacuum_pump_001_001  label="OTS-0003-00_vacuum-pump_Body_002"  # a2plus imported part (geometry in sourceFile) (typed FeaturePython)
  Placement = pos=(-133.936,10.2256,-481.281) rot=(0,0,-1;1.5708rad)
  Visibility1 = true
  a2p_Version = V0.1
  fixedPosition = false
  objectType = a2pPart
  sourceFile = ./OTS/OTS-0003-00_vacuum-pump.FCStd
  sourcePart = Body
  subassemblyImport = false
  timeLastImport = 1.64563e+09
  updateColors = true
FEATURE [Part::FeaturePython] b_FDM_0025_pump_mount_001_001  label="FDM-0025_pump-mount_Body_002"  # a2plus imported part (geometry in sourceFile) (typed FeaturePython)
  Placement = pos=(-163.524,-15.2591,-452.615) rot=(-1,0,0;1.5708rad)
  Visibility1 = true
  a2p_Version = V0.1
  fixedPosition = false
  objectType = a2pPart
  sourceFile = ./FDM/FDM-0025_pump-mount.FCStd
  sourcePart = Body
  subassemblyImport = false
  timeLastImport = 1.64563e+09
  updateColors = true
FEATURE [Part::FeaturePython] b_24v_3_Way_Solenoid_Valve_0526T_www_fspump_cn_001_  label="24v_3-Way_Solenoid_Valve_0526T_www.fspump.cn_001"  # a2plus imported part (geometry in sourceFile) (typed FeaturePython)
  Placement = pos=(-139.41,33.3489,-368.481) rot=(0.707107,0,0.707107;3.14159rad)
  a2p_Version = V0.1
  fixedPosition = false
  objectType = a2pPart
  sourceFile = ./OTS/OTS-0020-00_24v_3-Way_Solenoid_Valve_0526T_www.fspump.cn.FCStd
  subassemblyImport = false
  timeLastImport = 1.64563e+09
  updateColors = true
FEATURE [Part::FeaturePython] b_OTS_0020_index_motherboard1_001_  label="PCB-0001-00_index_motherboard"  # a2plus imported part (geometry in sourceFile) (typed FeaturePython)
  Placement = pos=(12.3801,14.999,28.6787) rot=(0.57735,0.57735,-0.57735;2.0944rad)
  a2p_Version = V0.1
  fixedPosition = false
  objectType = a2pPart
  sourceFile = ./PCB/PCB-0001-00_index_motherboard.step
  subassemblyImport = false
  timeLastImport = 1.64563e+09
  updateColors = true
FEATURE [Part::FeaturePython] Nut  label="M5-Nut478"  # Fasteners workbench fastener (typed FeaturePython)
  Placement = pos=(-193.752,99.2534,-236.782) rot=(0,-1,0;1.5708rad)
  baseObject = -> Screw044 [Edge16]
  diameter = 3
  invert = true
  matchOuter = false
  offset = -6
  thread = false
  type = 5
FEATURE [Part::FeaturePython] Screw185  label="M2.5x20-Screw"  # Fasteners workbench fastener (typed FeaturePython)
  Placement = pos=(-238.502,103.069,-220.074) rot=(-1,0,0;1.5708rad)
  baseObject = -> b_FDM_0014_down_camera_mount_001_ [Edge333]
  diameter = 3
  invert = false
  length = 8
  lengthCustom = 20
  matchOuter = true
  offset = 2
  thread = false
  type = 34
FEATURE [Part::FeaturePython] Screw186  label="M2.5x20-Screw034"  # Fasteners workbench fastener (typed FeaturePython)
  Placement = pos=(-238.502,103.069,-254.074) rot=(-1,0,0;1.5708rad)
  baseObject = -> b_FDM_0014_down_camera_mount_001_ [Edge337]
  diameter = 3
  invert = false
  length = 8
  lengthCustom = 20
  matchOuter = true
  offset = 2
  thread = false
  type = 34
FEATURE [Part::FeaturePython] Screw187  label="M2.5x20-Screw035"  # Fasteners workbench fastener (typed FeaturePython)
  Placement = pos=(-204.502,103.069,-254.074) rot=(-1,0,0;1.5708rad)
  baseObject = -> b_FDM_0014_down_camera_mount_001_ [Edge107]
  diameter = 3
  invert = false
  length = 8
  lengthCustom = 20
  matchOuter = true
  offset = 2
  thread = false
  type = 34
FEATURE [Part::FeaturePython] Screw188  label="M2.5x20-Screw036"  # Fasteners workbench fastener (typed FeaturePython)
  Placement = pos=(-204.502,103.069,-220.074) rot=(-1,0,0;1.5708rad)
  baseObject = -> b_FDM_0014_down_camera_mount_001_ [Edge343]
  diameter = 3
  invert = false
  length = 8
  lengthCustom = 20
  matchOuter = true
  offset = 2
  thread = false
  type = 34
FEATURE [Part::FeaturePython] Screw189  label="M3x14-Screw105"  # Fasteners workbench fastener (typed FeaturePython)
  Placement = pos=(-236.252,118.069,-214.574) rot=(0,-1,0;1.5708rad)
  baseObject = -> b_FDM_0014_down_camera_mount_001_ [Edge355]
  diameter = 1
  invert = false
  length = 4
  lengthCustom = 14
  matchOuter = true
  offset = 0
  thread = false
  type = 40
FEATURE [App::DocumentObjectGroup] Group013  label="GT2BeltClamp"
  Group = -> [b_FDM_0027_belt_clamp_001_003,b_FDM_0027_belt_clamp_001_002,Screw040,Screw041,Screw038,Screw039]
FEATURE [App::DocumentObjectGroup] Group014  label="Motor"
  Group = -> [b_Nema_17_42A02C_v21_001_,b_Gates_2GT_20T_Toothed_Pulley1_001_,Screw085,Screw086,Screw087,Screw088]
FEATURE [App::DocumentObjectGroup] Group016  label="EndStop"
  Group = -> [b_MakerBot_LimitSwitchBoard1_001_002,Screw123,Screw124]
FEATURE [Part::FeaturePython] b_FDM_0046_umbilical_swivel_base_001_  label="FDM-0046_umbilical-swivel-base_Body_001"  # a2plus imported part (geometry in sourceFile) (typed FeaturePython)
  Placement = pos=(62.725,110.061,49.7822) rot=(0,1,0;2.35619rad)
  a2p_Version = V0.1
  fixedPosition = false
  objectType = a2pPart
  sourceFile = ./FDM/FDM-0046_umbilical-swivel-base.FCStd
  sourcePart = Body
  subassemblyImport = false
  timeLastImport = 1.64563e+09
  updateColors = true
FEATURE [Part::FeaturePython] b_FDM_0047_umbilical_swivel_extension_001_  label="FDM-0047_umbilical-swivel-extension_Body_001"  # a2plus imported part (geometry in sourceFile) (typed FeaturePython)
  Placement = pos=(-8.65789,226.048,-21.6081) rot=(0.194456,0.977599,0.080546;2.37209rad)
  a2p_Version = V0.1
  fixedPosition = false
  objectType = a2pPart
  sourceFile = ./FDM/FDM-0047_umbilical-swivel-extension.FCStd
  sourcePart = Body
  subassemblyImport = false
  timeLastImport = 1.64563e+09
  updateColors = true
FEATURE [Part::FeaturePython] Screw190  label="M5x40-Screw282"  # Fasteners workbench fastener (typed FeaturePython)
  Placement = pos=(8.17264,256.452,-12.0838) rot=(-0.812309,0.496476,0.306047;1.36825rad)
  diameter = 6
  invert = true
  length = 9
  lengthCustom = 40
  matchOuter = false
  offset = 0
  thread = false
  type = 33
FEATURE [Part::FeaturePython] Nut086  label="M5-Nut455"  # Fasteners workbench fastener (typed FeaturePython)
  Placement = pos=(-1.60579,223.505,-21.8483) rot=(0.412043,0.700215,-0.583027;2.86481rad)
  Visibility1 = true
  diameter = 7
  invert = false
  matchOuter = false
  offset = 0
  thread = false
  type = 7
FEATURE [Part::FeaturePython] Screw155  label="M3x10-Screw032"  # Fasteners workbench fastener (typed FeaturePython)
  Placement = pos=(-58.83,42.98,-135.31) rot=(0.57735,-0.57735,-0.57735;4.18879rad)
  Visibility1 = true
  diameter = 1
  invert = false
  length = 9
  lengthCustom = 10
  matchOuter = false
  offset = 0
  thread = false
  type = 39
FEATURE [Part::FeaturePython] Screw154  label="M3x10-Screw031"  # Fasteners workbench fastener (typed FeaturePython)
  Placement = pos=(-148.75,42.98,-135.31) rot=(0.57735,-0.57735,-0.57735;4.18879rad)
  Visibility1 = true
  diameter = 1
  invert = false
  length = 9
  lengthCustom = 10
  matchOuter = false
  offset = 0
  thread = false
  type = 39
FEATURE [Part::FeaturePython] Screw153  label="M3x10-Screw030"  # Fasteners workbench fastener (typed FeaturePython)
  Placement = pos=(-148.75,42.98,-45.39) rot=(0.57735,-0.57735,-0.57735;4.18879rad)
  Visibility1 = true
  diameter = 1
  invert = false
  length = 9
  lengthCustom = 10
  matchOuter = false
  offset = 0
  thread = false
  type = 39
FEATURE [Part::FeaturePython] Screw152  label="M3x10-Screw029"  # Fasteners workbench fastener (typed FeaturePython)
  Placement = pos=(-58.83,42.98,-45.39) rot=(0.57735,-0.57735,-0.57735;4.18879rad)
  Visibility1 = true
  diameter = 1
  invert = false
  length = 9
  lengthCustom = 10
  matchOuter = false
  offset = 0
  thread = false
  type = 39
FEATURE [Part::FeaturePython] Screw191  label="M3x10-Screw041"  # Fasteners workbench fastener (typed FeaturePython)
  Placement = pos=(-58.97,13.5,-45.39) rot=(1,0,0;1.5708rad)
  diameter = 1
  invert = false
  length = 2
  lengthCustom = 10
  matchOuter = false
  offset = 0
  thread = false
  type = 40
FEATURE [Part::FeaturePython] Screw192  label="M3x10-Screw042"  # Fasteners workbench fastener (typed FeaturePython)
  Placement = pos=(-148.62,13.5,-45.34) rot=(1,0,0;1.5708rad)
  diameter = 1
  invert = false
  length = 2
  lengthCustom = 10
  matchOuter = false
  offset = 0
  thread = false
  type = 40
  expr: .Placement.Base.y = 13.5
FEATURE [Part::FeaturePython] Screw193  label="M3x10-Screw043"  # Fasteners workbench fastener (typed FeaturePython)
  Placement = pos=(-148.62,13.5,-135.29) rot=(1,0,0;1.5708rad)
  diameter = 1
  invert = false
  length = 2
  lengthCustom = 10
  matchOuter = false
  offset = 0
  thread = false
  type = 40
FEATURE [Part::FeaturePython] Screw194  label="M3x10-Screw044"  # Fasteners workbench fastener (typed FeaturePython)
  Placement = pos=(-58.77,13.5,-135.29) rot=(1,0,0;1.5708rad)
  diameter = 1
  invert = false
  length = 2
  lengthCustom = 10
  matchOuter = false
  offset = 0
  thread = false
  type = 40
FEATURE [Part::FeaturePython] PcbSpacer  label="M3x5.5x25-Spacer"  # WARN: FeaturePython — macro-defined, semantics opaque (R4)
  Placement = pos=(-148.92,40,-45.39) rot=(1,0,0;1.5708rad)
  diameter = 2
  invert = false
  length = 19
  offset = 0
  width = 1
FEATURE [Part::FeaturePython] PcbSpacer001  label="M3x5.5x25-Spacer001"  # WARN: FeaturePython — macro-defined, semantics opaque (R4)
  Placement = pos=(-148.92,40,-135.34) rot=(1,0,0;1.5708rad)
  diameter = 2
  invert = false
  length = 19
  offset = 0
  width = 1
FEATURE [Part::FeaturePython] PcbSpacer002  label="M3x5.5x25-Spacer002"  # WARN: FeaturePython — macro-defined, semantics opaque (R4)
  Placement = pos=(-58.97,40,-45.39) rot=(1,0,0;1.5708rad)
  diameter = 2
  invert = false
  length = 19
  offset = 0
  width = 1
FEATURE [Part::FeaturePython] PcbSpacer003  label="M3x5.5x25-Spacer003"  # WARN: FeaturePython — macro-defined, semantics opaque (R4)
  Placement = pos=(-58.77,40,-135.34) rot=(1,0,0;1.5708rad)
  diameter = 2
  invert = false
  length = 19
  offset = 0
  width = 1
FEATURE [Part::FeaturePython] b_FDM_0055_datum_board_mount_001_  label="FDM-0055_datum-board-mount_Body_001"  # a2plus imported part (geometry in sourceFile) (typed FeaturePython)
  Placement = pos=(-133.979,42.9044,-270.391) rot=(0.57735,-0.57735,-0.57735;4.18879rad)
  a2p_Version = V0.1
  fixedPosition = false
  objectType = a2pPart
  sourceFile = ./FDM/FDM-0055_datum-board-mount.FCStd
  sourcePart = Body
  subassemblyImport = false
  timeLastImport = 1.64668e+09
  updateColors = true
FEATURE [Part::FeaturePython] Screw195  label="M3x16-Screw044"  # Fasteners workbench fastener (typed FeaturePython)
  Placement = pos=(-133.94,52.9,-330.39) rot=(0,0.707107,0.707107;3.14159rad)
  Visibility1 = true
  diameter = 4
  invert = false
  length = 6
  lengthCustom = 16
  matchOuter = false
  offset = 0
  thread = false
  type = 33
FEATURE [Part::FeaturePython] Nut088  label="M3-Nut233"  # Fasteners workbench fastener (typed FeaturePython)
  Placement = pos=(-133.951,37.57,-330.41) rot=(-1,0,0;1.5708rad)
  diameter = 4
  invert = false
  matchOuter = false
  offset = -2
  thread = false
  type = 7
FEATURE [Part::FeaturePython] Screw196  label="M3x16-Screw048"  # Fasteners workbench fastener (typed FeaturePython)
  Placement = pos=(-133.94,52.9,-270.39) rot=(0,0.707107,0.707107;3.14159rad)
  Visibility1 = true
  diameter = 4
  invert = false
  length = 6
  lengthCustom = 16
  matchOuter = false
  offset = 0
  thread = false
  type = 33
FEATURE [Part::FeaturePython] Screw197  label="M3x16-Screw049"  # Fasteners workbench fastener (typed FeaturePython)
  Placement = pos=(-148.94,52.9,-315.39) rot=(0,0.707107,0.707107;3.14159rad)
  Visibility1 = true
  diameter = 4
  invert = false
  length = 6
  lengthCustom = 16
  matchOuter = false
  offset = 0
  thread = false
  type = 33
FEATURE [Part::FeaturePython] Screw198  label="M3x16-Screw050"  # Fasteners workbench fastener (typed FeaturePython)
  Placement = pos=(-148.94,52.9,-285.39) rot=(0,0.707107,0.707107;3.14159rad)
  Visibility1 = true
  diameter = 4
  invert = false
  length = 6
  lengthCustom = 16
  matchOuter = false
  offset = 0
  thread = false
  type = 33
FEATURE [Part::FeaturePython] Nut089  label="M3-Nut237"  # Fasteners workbench fastener (typed FeaturePython)
  Placement = pos=(-133.951,37.57,-270.41) rot=(-1,0,0;1.5708rad)
  diameter = 4
  invert = false
  matchOuter = false
  offset = -2
  thread = false
  type = 7
FEATURE [Part::FeaturePython] Nut090  label="M3-Nut238"  # Fasteners workbench fastener (typed FeaturePython)
  Placement = pos=(-148.951,37.57,-315.41) rot=(-1,0,0;1.5708rad)
  diameter = 4
  invert = false
  matchOuter = false
  offset = -2
  thread = false
  type = 7
FEATURE [Part::FeaturePython] Nut091  label="M3-Nut239"  # Fasteners workbench fastener (typed FeaturePython)
  Placement = pos=(-148.951,37.57,-285.41) rot=(-1,0,0;1.5708rad)
  diameter = 4
  invert = false
  matchOuter = false
  offset = -2
  thread = false
  type = 7
FEATURE [Part::FeaturePython] Screw199  label="M3x8-Screw306"  # Fasteners workbench fastener (typed FeaturePython)
  Placement = pos=(-171.94,139.05,-249.42) rot=(0,1,0;1.5708rad)
  Visibility1 = true
  diameter = 1
  invert = false
  length = 1
  lengthCustom = 8
  matchOuter = false
  offset = 0
  thread = false
  type = 39
FEATURE [Part::FeaturePython] Screw200  label="M3x8-Screw307"  # Fasteners workbench fastener (typed FeaturePython)
  Placement = pos=(-171.94,139.05,-264.41) rot=(0,1,0;1.5708rad)
  Visibility1 = true
  diameter = 1
  invert = false
  length = 1
  lengthCustom = 8
  matchOuter = false
  offset = 0
  thread = false
  type = 39
FEATURE [App::DocumentObjectGroup] Group010  label="Right-Z-Gantry"
  Group = -> [Screw148,Screw149,b_FDM_0041_z_gantry_backplate_right_001_,b_FDM_0039_z_gantry_right_001_,Screw199,Screw200]
FEATURE [Part::FeaturePython] Screw201  label="M3x8-Screw311"  # Fasteners workbench fastener (typed FeaturePython)
  Placement = pos=(-171.94,143.17,-224.25) rot=(0,1,0;1.5708rad)
  Visibility1 = true
  diameter = 1
  invert = false
  length = 1
  lengthCustom = 8
  matchOuter = false
  offset = 0
  thread = false
  type = 39
FEATURE [Part::FeaturePython] Screw202  label="M3x8-Screw310"  # Fasteners workbench fastener (typed FeaturePython)
  Placement = pos=(-171.94,143.17,-209.15) rot=(0,1,0;1.5708rad)
  Visibility1 = true
  diameter = 1
  invert = false
  length = 1
  lengthCustom = 8
  matchOuter = false
  offset = 0
  thread = false
  type = 39
FEATURE [Part::FeaturePython] b_FDM_0042_valve_mount_001_  label="FDM-0042_valve-mount_001"  # a2plus imported part (geometry in sourceFile) (typed FeaturePython)
  Placement = pos=(-152.52,39.667,-341.576) rot=(-1,0,0;3.14159rad)
  a2p_Version = V0.1
  fixedPosition = false
  objectType = a2pPart
  sourceFile = ./FDM/FDM-0042_valve-mount.FCStd
  subassemblyImport = false
  timeLastImport = 1.64668e+09
  updateColors = true
FEATURE [Part::FeaturePython] Screw203  label="M3x8-Screw318"  # Fasteners workbench fastener (typed FeaturePython)
  Placement = pos=(-144.79,19.64,-347.2) rot=(0.707107,0,-0.707107;3.14159rad)
  Visibility1 = true
  diameter = 1
  invert = false
  length = 1
  lengthCustom = 8
  matchOuter = false
  offset = 0
  thread = false
  type = 39
FEATURE [Part::FeaturePython] Screw204  label="M3x8-Screw313"  # Fasteners workbench fastener (typed FeaturePython)
  Placement = pos=(-144.99,29.64,-362.6) rot=(0.707107,0,-0.707107;3.14159rad)
  Visibility1 = true
  diameter = 1
  invert = false
  length = 1
  lengthCustom = 8
  matchOuter = false
  offset = 0
  thread = false
  type = 39
FEATURE [Part::FeaturePython] Screw205  label="M3x8-Screw314"  # Fasteners workbench fastener (typed FeaturePython)
  Placement = pos=(-148.49,43.04,-375.7) rot=(0.57735,0.57735,0.57735;4.18879rad)
  Visibility1 = true
  diameter = 1
  invert = false
  length = 1
  lengthCustom = 8
  matchOuter = false
  offset = 0
  thread = false
  type = 39
FEATURE [Part::FeaturePython] Screw206  label="M3x8-Screw316"  # Fasteners workbench fastener (typed FeaturePython)
  Placement = pos=(-118.49,43.04,-345.6) rot=(0.57735,0.57735,0.57735;4.18879rad)
  Visibility1 = true
  diameter = 1
  invert = false
  length = 1
  lengthCustom = 8
  matchOuter = false
  offset = 0
  thread = false
  type = 39
FEATURE [Part::FeaturePython] Nut092  label="M3-Nut273"  # Fasteners workbench fastener (typed FeaturePython)
  Placement = pos=(-148.551,35.97,-375.61) rot=(-1,0,0;1.5708rad)
  diameter = 4
  invert = false
  matchOuter = false
  offset = -2
  thread = false
  type = 7
FEATURE [Part::FeaturePython] Nut093  label="M3-Nut276"  # Fasteners workbench fastener (typed FeaturePython)
  Placement = pos=(-118.751,35.97,-345.81) rot=(-1,0,0;1.5708rad)
  diameter = 4
  invert = false
  matchOuter = false
  offset = -2
  thread = false
  type = 7
FEATURE [Part::FeaturePython] Screw207  label="M3x30-Screw108"  # Fasteners workbench fastener (typed FeaturePython)
  Placement = pos=(-74.04,43.1,-180.31) rot=(-1,0,0;1.5708rad)
  Visibility1 = true
  diameter = 4
  invert = false
  length = 9
  lengthCustom = 30
  matchOuter = false
  offset = 0
  thread = false
  type = 33
FEATURE [Part::FeaturePython] Screw208  label="M3x8-Screw317"  # Fasteners workbench fastener (typed FeaturePython)
  Placement = pos=(-148.49,43.04,-345.6) rot=(0.57735,0.57735,0.57735;4.18879rad)
  Visibility1 = true
  diameter = 1
  invert = false
  length = 1
  lengthCustom = 8
  matchOuter = false
  offset = 0
  thread = false
  type = 39
FEATURE [Part::FeaturePython] Nut094  label="M3-Nut275"  # Fasteners workbench fastener (typed FeaturePython)
  Placement = pos=(-148.351,35.97,-345.51) rot=(-1,0,0;1.5708rad)
  diameter = 4
  invert = false
  matchOuter = false
  offset = -2
  thread = false
  type = 7
FEATURE [Part::FeaturePython] Screw209  label="M3x8-Screw315"  # Fasteners workbench fastener (typed FeaturePython)
  Placement = pos=(-118.59,43.04,-375.4) rot=(0.57735,0.57735,0.57735;4.18879rad)
  Visibility1 = true
  diameter = 1
  invert = false
  length = 1
  lengthCustom = 8
  matchOuter = false
  offset = 0
  thread = false
  type = 39
FEATURE [Part::FeaturePython] Nut095  label="M3-Nut274"  # Fasteners workbench fastener (typed FeaturePython)
  Placement = pos=(-118.551,35.97,-375.41) rot=(-1,0,0;1.5708rad)
  diameter = 4
  invert = false
  matchOuter = false
  offset = -2
  thread = false
  type = 7
FEATURE [Part::FeaturePython] Nut096  label="M3-Nut249"  # Fasteners workbench fastener (typed FeaturePython)
  Placement = pos=(-74.0312,27.07,-180.317) rot=(0.57735,0.57735,-0.57735;2.0944rad)
  Visibility1 = true
  diameter = 4
  invert = false
  matchOuter = false
  offset = 0
  thread = false
  type = 7
FEATURE [Part::FeaturePython] Nut097  label="M5-Nut477"  # Fasteners workbench fastener (typed FeaturePython)
  Placement = pos=(-227.808,125.583,-205.48) rot=(-0.250563,-0.935113,0.250563;1.63783rad)
  Visibility1 = true
  diameter = 7
  invert = false
  matchOuter = false
  offset = 0
  thread = false
  type = 7
FEATURE [Part::FeaturePython] Nut098  label="M5-Nut463"  # Fasteners workbench fastener (typed FeaturePython)
  Placement = pos=(-227.808,125.653,-267.758) rot=(-0.250563,-0.935113,0.250563;1.63783rad)
  Visibility1 = true
  diameter = 7
  invert = false
  matchOuter = false
  offset = 0
  thread = false
  type = 7
FEATURE [Part::FeaturePython] Nut099  label="M5-Nut464"  # Fasteners workbench fastener (typed FeaturePython)
  Placement = pos=(-227.808,164.761,-267.821) rot=(-0.250563,-0.935113,0.250563;1.63783rad)
  Visibility1 = true
  diameter = 7
  invert = false
  matchOuter = false
  offset = 0
  thread = false
  type = 7
FEATURE [Part::FeaturePython] Nut100  label="M5-Nut465"  # Fasteners workbench fastener (typed FeaturePython)
  Placement = pos=(-227.808,164.764,-205.815) rot=(-0.250563,-0.935113,0.250563;1.63783rad)
  Visibility1 = true
  diameter = 7
  invert = false
  matchOuter = false
  offset = 0
  thread = false
  type = 7
FEATURE [Part::FeaturePython] b_FDM_0023_peek_cable_guide_001_  label="FDM-0023_peek-cable-guide_001"  # a2plus imported part (geometry in sourceFile) (typed FeaturePython)
  Placement = pos=(-58.8938,36.6196,-555.348) rot=(1,0,0;3.14159rad)
  a2p_Version = V0.1
  fixedPosition = false
  objectType = a2pPart
  sourceFile = ./FDM/FDM-0023_peek-cable-guide.FCStd
  subassemblyImport = false
  timeLastImport = 1.64563e+09
  updateColors = true
FEATURE [Part::FeaturePython] b_FDM_0023_peek_cable_guide_001_001  label="FDM-0023_peek-cable-guide_002"  # a2plus imported part (geometry in sourceFile) (typed FeaturePython)
  Placement = pos=(-58.8938,36.6196,-435.248) rot=(1,0,0;3.14159rad)
  a2p_Version = V0.1
  fixedPosition = false
  objectType = a2pPart
  sourceFile = ./FDM/FDM-0023_peek-cable-guide.FCStd
  subassemblyImport = false
  timeLastImport = 1.64563e+09
  updateColors = true
FEATURE [Part::FeaturePython] b_FDM_0023_peek_cable_guide_001_002  label="FDM-0023_peek-cable-guide_003"  # a2plus imported part (geometry in sourceFile) (typed FeaturePython)
  Placement = pos=(-58.8938,36.6196,-255.048) rot=(1,0,0;3.14159rad)
  a2p_Version = V0.1
  fixedPosition = false
  objectType = a2pPart
  sourceFile = ./FDM/FDM-0023_peek-cable-guide.FCStd
  subassemblyImport = false
  timeLastImport = 1.64563e+09
  updateColors = true
FEATURE [Part::FeaturePython] b_FDM_0023_peek_cable_guide_001_003  label="FDM-0023_peek-cable-guide_004"  # a2plus imported part (geometry in sourceFile) (typed FeaturePython)
  Placement = pos=(-148.894,36.6196,-405.948) rot=(0,0,1;3.14159rad)
  a2p_Version = V0.1
  fixedPosition = false
  objectType = a2pPart
  sourceFile = ./FDM/FDM-0023_peek-cable-guide.FCStd
  subassemblyImport = false
  timeLastImport = 1.64563e+09
  updateColors = true
FEATURE [Part::FeaturePython] b_FDM_0023_peek_cable_guide_001_004  label="FDM-0023_peek-cable-guide_005"  # a2plus imported part (geometry in sourceFile) (typed FeaturePython)
  Placement = pos=(-148.894,36.6196,-195.448) rot=(0,0,1;3.14159rad)
  a2p_Version = V0.1
  fixedPosition = false
  objectType = a2pPart
  sourceFile = ./FDM/FDM-0023_peek-cable-guide.FCStd
  subassemblyImport = false
  timeLastImport = 1.64563e+09
  updateColors = true
FEATURE [Part::FeaturePython] b_FDM_0023_peek_cable_guide_001_005  label="FDM-0023_peek-cable-guide_006"  # a2plus imported part (geometry in sourceFile) (typed FeaturePython)
  Placement = pos=(-103.894,36.6196,-450.348) rot=(0,0,1;3.14159rad)
  a2p_Version = V0.1
  fixedPosition = false
  objectType = a2pPart
  sourceFile = ./FDM/FDM-0023_peek-cable-guide.FCStd
  subassemblyImport = false
  timeLastImport = 1.64563e+09
  updateColors = true
FEATURE [Part::FeaturePython] Nut101  label="M3-Nut250"  # Fasteners workbench fastener (typed FeaturePython)
  Placement = pos=(-148.651,31.45,-195.487) rot=(1,0,0;1.5708rad)
  Visibility1 = true
  diameter = 4
  invert = false
  matchOuter = false
  offset = 0
  thread = false
  type = 7
FEATURE [Part::FeaturePython] Screw210  label="M3x14-Screw090"  # Fasteners workbench fastener (typed FeaturePython)
  Placement = pos=(-148.94,42.8,-195.39) rot=(0,0.707107,0.707107;3.14159rad)
  Visibility1 = true
  diameter = 1
  invert = false
  length = 4
  lengthCustom = 14
  matchOuter = false
  offset = 0
  thread = false
  type = 39
FEATURE [Part::FeaturePython] Screw211  label="M3x14-Screw106"  # Fasteners workbench fastener (typed FeaturePython)
  Placement = pos=(-148.94,42.8,-406.19) rot=(0,0.707107,0.707107;3.14159rad)
  Visibility1 = true
  diameter = 1
  invert = false
  length = 4
  lengthCustom = 14
  matchOuter = false
  offset = 0
  thread = false
  type = 39
FEATURE [Part::FeaturePython] Screw212  label="M3x14-Screw097"  # Fasteners workbench fastener (typed FeaturePython)
  Placement = pos=(-59.04,42.8,-255.39) rot=(0,0.707107,0.707107;3.14159rad)
  Visibility1 = true
  diameter = 1
  invert = false
  length = 4
  lengthCustom = 14
  matchOuter = false
  offset = 0
  thread = false
  type = 39
FEATURE [Part::FeaturePython] Screw213  label="M3x14-Screw098"  # Fasteners workbench fastener (typed FeaturePython)
  Placement = pos=(-103.74,42.8,-450.39) rot=(0,0.707107,0.707107;3.14159rad)
  Visibility1 = true
  diameter = 1
  invert = false
  length = 4
  lengthCustom = 14
  matchOuter = false
  offset = 0
  thread = false
  type = 39
FEATURE [Part::FeaturePython] Screw214  label="M3x14-Screw101"  # Fasteners workbench fastener (typed FeaturePython)
  Placement = pos=(-58.84,42.8,-555.39) rot=(0,0.707107,0.707107;3.14159rad)
  Visibility1 = true
  diameter = 1
  invert = false
  length = 4
  lengthCustom = 14
  matchOuter = false
  offset = 0
  thread = false
  type = 39
FEATURE [Part::FeaturePython] Screw215  label="M3x14-Screw100"  # Fasteners workbench fastener (typed FeaturePython)
  Placement = pos=(-58.84,42.8,-435.19) rot=(0,0.707107,0.707107;3.14159rad)
  Visibility1 = true
  diameter = 1
  invert = false
  length = 4
  lengthCustom = 14
  matchOuter = false
  offset = 0
  thread = false
  type = 39
FEATURE [Part::FeaturePython] Nut102  label="M3-Nut272"  # Fasteners workbench fastener (typed FeaturePython)
  Placement = pos=(-148.651,31.45,-406.087) rot=(1,0,0;1.5708rad)
  Visibility1 = true
  diameter = 4
  invert = false
  matchOuter = false
  offset = 0
  thread = false
  type = 7
FEATURE [Part::FeaturePython] Nut103  label="M3-Nut257"  # Fasteners workbench fastener (typed FeaturePython)
  Placement = pos=(-58.6512,31.45,-255.487) rot=(1,0,0;1.5708rad)
  Visibility1 = true
  diameter = 4
  invert = false
  matchOuter = false
  offset = 0
  thread = false
  type = 7
FEATURE [Part::FeaturePython] Nut104  label="M3-Nut261"  # Fasteners workbench fastener (typed FeaturePython)
  Placement = pos=(-103.851,31.45,-450.487) rot=(1,0,0;1.5708rad)
  Visibility1 = true
  diameter = 4
  invert = false
  matchOuter = false
  offset = 0
  thread = false
  type = 7
FEATURE [Part::FeaturePython] Nut105  label="M3-Nut262"  # Fasteners workbench fastener (typed FeaturePython)
  Placement = pos=(-58.8512,31.45,-435.187) rot=(1,0,0;1.5708rad)
  Visibility1 = true
  diameter = 4
  invert = false
  matchOuter = false
  offset = 0
  thread = false
  type = 7
FEATURE [Part::FeaturePython] Nut106  label="M3-Nut263"  # Fasteners workbench fastener (typed FeaturePython)
  Placement = pos=(-58.8512,31.45,-555.387) rot=(1,0,0;1.5708rad)
  Visibility1 = true
  diameter = 4
  invert = false
  matchOuter = false
  offset = 0
  thread = false
  type = 7
FEATURE [Part::FeaturePython] b_OTS_0005_00_zip_tie_Body_001_  label="OTS-0005-00_zip-tie_Body_001"  # a2plus imported part (geometry in sourceFile) (typed FeaturePython)
  Placement = pos=(-85.5988,312.912,-156.003) rot=(0.691599,0.714463,-0.105987;3.93294rad)
  a2p_Version = V0.1
  fixedPosition = false
  objectType = a2pPart
  sourceFile = ./OTS/OTS-0005-00_zip-tie.FCStd
  sourcePart = Body
  subassemblyImport = false
  timeLastImport = 1.64563e+09
  updateColors = true
FEATURE [Part::FeaturePython] b_OTS_0005_00_zip_tie_Body_001_001  label="OTS-0005-00_zip-tie_Body_002"  # a2plus imported part (geometry in sourceFile) (typed FeaturePython)
  Placement = pos=(-54.977,288.893,-113.363) rot=(0.691599,0.714463,-0.105987;3.93294rad)
  a2p_Version = V0.1
  fixedPosition = false
  objectType = a2pPart
  sourceFile = ./OTS/OTS-0005-00_zip-tie.FCStd
  sourcePart = Body
  subassemblyImport = false
  timeLastImport = 1.64563e+09
  updateColors = true
FEATURE [Part::FeaturePython] b_OTS_0005_00_zip_tie_Body_001_002  label="OTS-0005-00_zip-tie_Body_009"  # a2plus imported part (geometry in sourceFile) (typed FeaturePython)
  Placement = pos=(-17.4078,266.717,-72.7243) rot=(0.691599,0.714463,-0.105987;3.93294rad)
  a2p_Version = V0.1
  fixedPosition = false
  objectType = a2pPart
  sourceFile = ./OTS/OTS-0005-00_zip-tie.FCStd
  sourcePart = Body
  subassemblyImport = false
  timeLastImport = 1.64563e+09
  updateColors = true
FEATURE [Part::FeaturePython] b_OTS_0005_00_zip_tie_Body_001_003  label="OTS-0005-00_zip-tie_Body_010"  # a2plus imported part (geometry in sourceFile) (typed FeaturePython)
  Placement = pos=(53.066,219.575,-23.271) rot=(0.742383,0.669768,0.016681;4.17509rad)
  a2p_Version = V0.1
  fixedPosition = false
  objectType = a2pPart
  sourceFile = ./OTS/OTS-0005-00_zip-tie.FCStd
  sourcePart = Body
  subassemblyImport = false
  timeLastImport = 1.64563e+09
  updateColors = true
FEATURE [Part::FeaturePython] b_PCB_0002_00_Datum_OpenPNPcalibration1_001_  label="PCB-0002-00_Datum-OpenPNPcalibration1_001"  # a2plus imported part (geometry in sourceFile) (typed FeaturePython)
  Placement = pos=(-124.331,51.3924,-260.466) rot=(0.57735,-0.57735,-0.57735;4.18879rad)
  a2p_Version = V0.1
  fixedPosition = false
  objectType = a2pPart
  sourceFile = .\PCB\PCB-0002-00_Datum-OpenPNPcalibration.step
  subassemblyImport = false
  timeLastImport = 1.64563e+09
  updateColors = true
FEATURE [Part::FeaturePython] b_FDM_0016_cable_clip_001_  label="FDM-0016_cable-clip_001"  # a2plus imported part (geometry in sourceFile) (typed FeaturePython)
  Placement = pos=(-334.255,19.7601,-589.786) rot=(0,1,0;1.5708rad)
  a2p_Version = V0.1
  fixedPosition = false
  objectType = a2pPart
  sourceFile = .\FDM\FDM-0016_cable-clip.FCStd
  subassemblyImport = false
  timeLastImport = 1.64563e+09
  updateColors = true
FEATURE [Part::FeaturePython] b_FDM_0016_cable_clip_001_001  label="FDM-0016_cable-clip_002"  # a2plus imported part (geometry in sourceFile) (typed FeaturePython)
  Placement = pos=(-291.599,21.0844,-589.708) rot=(0,1,0;1.5708rad)
  a2p_Version = V0.1
  fixedPosition = false
  objectType = a2pPart
  sourceFile = .\FDM\FDM-0016_cable-clip.FCStd
  subassemblyImport = false
  timeLastImport = 1.64563e+09
  updateColors = true
FEATURE [Part::FeaturePython] b_FDM_0016_cable_clip_001_002  label="FDM-0016_cable-clip_003"  # a2plus imported part (geometry in sourceFile) (typed FeaturePython)
  Placement = pos=(-253.003,20.7641,-589.708) rot=(0,1,0;1.5708rad)
  a2p_Version = V0.1
  fixedPosition = false
  objectType = a2pPart
  sourceFile = .\FDM\FDM-0016_cable-clip.FCStd
  subassemblyImport = false
  timeLastImport = 1.64563e+09
  updateColors = true
FEATURE [Part::FeaturePython] b_FDM_0016_cable_clip_001_003  label="FDM-0016_cable-clip_004"  # a2plus imported part (geometry in sourceFile) (typed FeaturePython)
  Placement = pos=(-174.891,20.1235,-589.708) rot=(0,1,0;1.5708rad)
  a2p_Version = V0.1
  fixedPosition = false
  objectType = a2pPart
  sourceFile = .\FDM\FDM-0016_cable-clip.FCStd
  subassemblyImport = false
  timeLastImport = 1.64563e+09
  updateColors = true
FEATURE [App::DocumentObjectGroup] Group008  label="Extrusion"
  Group = -> [b_M5_tslot_nut1_001_028,b_M5_tslot_nut1_001_029,Screw103,Screw104,b_M5_tslot_nut1_001_024,b_M5_tslot_nut1_001_025,b_M5_tslot_nut1_001_026,b_M5_tslot_nut1_001_027,Screw081,Screw082,Screw083,Screw084,Screw077,Screw078,Screw079,Screw080,b_M5_tslot_nut1_001_020,b_M5_tslot_nut1_001_021,b_M5_tslot_nut1_001_022,b_M5_tslot_nut1_001_023,b_2020CornerBracket1_001_002,b_2020CornerBracket1_001_003,+23 more]
FEATURE [Part::FeaturePython] b_PCB_0003_00_RingLight1_001_  label="PCB-0003-00_RingLight1_001"  # a2plus imported part (geometry in sourceFile) (typed FeaturePython)
  Placement = pos=(-104.466,32.5,-300.339) rot=(-0.274699,0.679905,0.679905;2.60542rad)
  a2p_Version = V0.1
  fixedPosition = false
  objectType = a2pPart
  sourceFile = .\PCB\PCB-0003-00_RingLight.step
  subassemblyImport = false
  timeLastImport = 1.64563e+09
  updateColors = true
FEATURE [Part::FeaturePython] b_PCB_0003_00_RingLight1_001_001  label="PCB-0003-00_RingLight1_002"  # a2plus imported part (geometry in sourceFile) (typed FeaturePython)
  Placement = pos=(-221.73,90.9615,-237.287) rot=(0.57735,-0.57735,0.57735;2.0944rad)
  a2p_Version = V0.1
  fixedPosition = false
  objectType = a2pPart
  sourceFile = .\PCB\PCB-0003-00_RingLight.step
  subassemblyImport = false
  timeLastImport = 1.64563e+09
  updateColors = true
FEATURE [App::DocumentObjectGroup] Group012  label="CameraAndLight"
  Group = -> [b_FDM_0014_down_camera_mount_001_,b_FDM_0015_down_light_mount_001_,Screw171,Screw185,Screw186,Screw187,Screw188,Screw189,b_OTS_0002_00_usb_webcam_001_,b_PCB_0003_00_RingLight1_001_001]
FEATURE [Part::FeaturePython] Screw216  label="M2.5x8-Screw096"  # Fasteners workbench fastener (typed FeaturePython)
  Placement = pos=(-144.4,110,-201.2) rot=(1,0,0;1.5708rad)
  diameter = 3
  invert = false
  length = 3
  lengthCustom = 8
  matchOuter = false
  offset = 0
  thread = false
  type = 34
FEATURE [Part::FeaturePython] Screw217  label="M2.5x8-Screw097"  # Fasteners workbench fastener (typed FeaturePython)
  Placement = pos=(-144.4,110,-224.1) rot=(1,0,0;1.5708rad)
  diameter = 3
  invert = false
  length = 3
  lengthCustom = 8
  matchOuter = false
  offset = 0
  thread = false
  type = 34
FEATURE [Part::FeaturePython] Screw218  label="M2.5x8-Screw"  # Fasteners workbench fastener (typed FeaturePython)
  Placement = pos=(-167.3,110,-201.1) rot=(1,0,0;1.5708rad)
  diameter = 3
  invert = false
  length = 3
  lengthCustom = 8
  matchOuter = false
  offset = 0
  thread = false
  type = 34
FEATURE [Part::FeaturePython] Screw219  label="M2.5x8-Screw098"  # Fasteners workbench fastener (typed FeaturePython)
  Placement = pos=(-167.3,110,-224.1) rot=(1,0,0;1.5708rad)
  diameter = 3
  invert = false
  length = 3
  lengthCustom = 8
  matchOuter = false
  offset = 0
  thread = false
  type = 34
FEATURE [App::DocumentObjectGroup] Group009  label="Left-Z-Gantry"
  Group = -> [b_FDM_0040_z_gantry_backplate_left_001_,Screw144,Screw146,b_FDM_0017_z_gantry_left_001_,b_OTS_0001_00_CP40_nozzle_holder_001_,b_MS4M_M51_001_,b_smc_stepper1_001_,Screw201,Screw202,Screw216,Screw217,Screw218,Screw219]
FEATURE [Part::FeaturePython] b_OTS_0009_pneumatic_splitter_URY6M_4M1_001_  label="OTS-0009_pneumatic-splitter-URY6M-4M1_001"  # a2plus imported part (geometry in sourceFile) (typed FeaturePython)
  Placement = pos=(-74.0937,33.3499,-202.48) rot=(-1,0,0;4.71239rad)
  a2p_Version = V0.1
  fixedPosition = false
  objectType = a2pPart
  sourceFile = ./OTS/OTS-0009_pneumatic-splitter-URY6M-4M.STEP
  subassemblyImport = false
  timeLastImport = 1.64082e+09
  updateColors = true
FEATURE [App::DocumentObjectGroup] Group003  label="Plate"
  Group = -> [b_FDM_0019_up_light_mount_001_,b_FDM_0020_up_camera_mount_001_,Screw174,Screw175,Screw176,Screw177,Nut052,Nut053,Nut054,Nut055,Screw139,Screw142,Nut057,Nut058,Screw178,Screw179,Screw180,Screw134,Screw152,Screw153,Screw154,Screw155,b_FDM_0024_nozzle_holder_001_,Nut064,Nut065,Nut066,Screw156,Screw157,Screw158,b_OTS_0002_00_usb_webcam_001_001,Screw159,Screw160,Screw161,Screw162,+60 more]
FEATURE [Part::FeaturePython] b_FST_0017_M3_cap_nut1_001_  label="FST-0017_M3-cap-nut1_001"  # a2plus imported part (geometry in sourceFile) (typed FeaturePython)
  Placement = pos=(89.5237,100.422,-575.135) rot=(0,1,0;1.5708rad)
  a2p_Version = V0.1
  fixedPosition = false
  objectType = a2pPart
  sourceFile = ./FST/FST-0017_M3-cap-nut.STEP
  subassemblyImport = false
  timeLastImport = 1.64563e+09
  updateColors = true
FEATURE [App::DocumentObjectGroup] Group005  label="Front-Right-Leg"
  Group = -> [b_FDM_0002_front_right_leg_001_001,b_M5_tslot_nut1_001_014,b_front_leg_tensioner_001_002,b_Gates_2GT_20T_Toothed_Idler1_001_003,Nut046,Screw062,Nut047,Screw063,Nut049,Screw064,Screw070,Screw071,Screw072,b_M5_tslot_nut1_001_012,b_M5_tslot_nut1_001_013,b_FST_0017_M3_cap_nut1_001_,b_M5_tslot_nut1_001_015,Screw061]
FEATURE [Part::FeaturePython] b_FST_0017_M3_cap_nut1_001_001  label="FST-0017_M3-cap-nut1_002"  # a2plus imported part (geometry in sourceFile) (typed FeaturePython)
  Placement = pos=(-224.192,144.277,-626.288) rot=(0,1,0;3.14159rad)
  a2p_Version = V0.1
  fixedPosition = false
  objectType = a2pPart
  sourceFile = ./FST/FST-0017_M3-cap-nut.STEP
  subassemblyImport = false
  timeLastImport = 1.64563e+09
  updateColors = true
FEATURE [App::DocumentObjectGroup] Group001  label="Y Gantry"
  Group = -> [b_MakerBot_LimitSwitchBoard1_001_001,b_FDM_0005_y_gantry_001_,b_OTS_0009_20x20_v_slot_600mm1_001_003,b_FDM_0005_y_gantry_001_001,b_FDM_0006_x_motor_mount_001_,b_FDM_0013_x_idler_mount_001_,b_FDM_0010_y_gantry_umbilical_mount_001_,b_FDM_0008_y_gantry_support_001_,b_FDM_0008_y_gantry_support_001_001,b_FDM_0009_roller_spacer_001_,b_v_slot_roller1_001_,b_v_slot_roller1_001_001,+86 more]
FEATURE [Part::FeaturePython] b_FST_0017_M3_cap_nut1_001_002  label="FST-0017_M3-cap-nut1_003"  # a2plus imported part (geometry in sourceFile) (typed FeaturePython)
  Placement = pos=(89.3507,100.008,-25.0268) rot=(0,1,0;1.5708rad)
  a2p_Version = V0.1
  fixedPosition = false
  objectType = a2pPart
  sourceFile = ./FST/FST-0017_M3-cap-nut.STEP
  subassemblyImport = false
  timeLastImport = 1.64563e+09
  updateColors = true
FEATURE [App::DocumentObjectGroup] Group004  label="Front-Left-Leg"
  Group = -> [Screw125,Screw126,Screw101,Screw102,b_M5_tslot_nut1_001_008,Nut048,Nut045,b_Gates_2GT_20T_Toothed_Idler1_001_001,Nut033,Screw052,Screw053,Screw054,Screw035,Screw036,Screw037,Screw051,b_M5_tslot_nut1_001_009,b_M5_tslot_nut1_001_010,b_M5_tslot_nut1_001_011,b_FDM_0001_front_left_leg_001_,b_front_leg_tensioner_001_,b_FDM_0007_frame_umbilical_mount_001_,b_MakerBot_LimitSwitchBoard1_001_,+11 more]
FEATURE [App::DocumentObjectGroup] Group  label="Base Frame"
  Group = -> [Group004,Group005,Group006,Group007,Group008]
FEATURE [Spreadsheet::Sheet] Fasteners_BOM
  cells = A1=Type; B1=Qty; A2=DIN985 Nut M5; B2=7; A3=ISO4032 Nut M3; B3=43; A4=ISO4032 Nut M5; B4=31; A5=ISO4762 Screw M2.5x20; B5=4; A6=ISO4762 Screw M2.5x8; B6=8; A7=ISO4762 Screw M3x16; B7=11; A8=ISO4762 Screw M3x30; B8=9; A9=ISO4762 Screw M5x10; B9=30; A10=ISO4762 Screw M5x25; B10=14; A11=ISO4762 Screw M5x40; B11=14; A12=ISO7380-1 Screw M3x10; B12=10; A13=ISO7380-1 Screw M3x14; B13=14; A14=ISO7380-1 Screw M3x8; B14=39; A15=ISO7380-1 Screw M5x8; B15=16
FEATURE [Part::FeaturePython] b_OTS_0014_linear_rail_100mm_LML9B1_001_  label="OTS-0014_linear-rail-100mm-LML9B1_001"  # a2plus imported part (geometry in sourceFile) (typed FeaturePython)
  Placement = pos=(-183.899,191.455,-256.908) rot=(0,0,1;4.71239rad)
  a2p_Version = V0.1
  fixedPosition = false
  objectType = a2pPart
  sourceFile = ./OTS/OTS-0014_linear-rail-100mm-LML9B.step
  subassemblyImport = false
  timeLastImport = 1.64563e+09
  updateColors = true
FEATURE [Part::FeaturePython] b_OTS_0014_linear_rail_100mm_LML9B1_001_001  label="OTS-0014_linear-rail-100mm-LML9B1_002"  # a2plus imported part (geometry in sourceFile) (typed FeaturePython)
  Placement = pos=(-184.099,191.555,-216.808) rot=(0,0,1;4.71239rad)
  a2p_Version = V0.1
  fixedPosition = false
  objectType = a2pPart
  sourceFile = ./OTS/OTS-0014_linear-rail-100mm-LML9B.step
  subassemblyImport = false
  timeLastImport = 1.64563e+09
  updateColors = true
FEATURE [App::DocumentObjectGroup] Group015  label="XBaseFrame"
  Group = -> [Nut,b_FDM_0011_x_gantry_front_001_,b_FDM_0012_x_gantry_back_001_,b_v_slot_roller1_001_003,b_v_slot_roller1_001_004,b_Gates_2GT_20T_Toothed_Idler1_001_,b_v_slot_roller1_001_005,Screw044,b_FDM_0009_roller_spacer_001_005,b_FDM_0009_roller_spacer_001_004,b_OTS_0005_00_zip_tie_001_006,b_OTS_0005_00_zip_tie_001_007,b_FDM_0043_001_,b_FDM_0043_001_001,Screw164,Screw165,Screw166,Screw167,Screw,Screw168,+31 more]
FEATURE [App::DocumentObjectGroup] Group002  label="X Gantry"
  Group = -> [Group015,Group009,Group010,Group012,Group014,Group016,Group013]
FEATURE [Spreadsheet::Sheet] _PARTSLIST_  label="#PARTSLIST#"
  cells = A1=POS; B1=QTY; C1=IDENTNO; D1=DESCRIPTION; E1=SUPPLIER; F1=SUPP.IDENTNO; G1=SUPP.DESCRIPTION; H1=(FILENAME); A2=1; B2=3; C2=*; D2=*; E2=*; F2=*; G2=*; H2=OTS-0019_limit-switch-PCBA.STEP; A3=2; B3=2; C3=*; D3=*; E3=*; F3=*; G3=*; H3=FDM-0005_y-gantry.FCStd; A4=3; B4=7; C4=*; D4=*; E4=*; F4=*; G4=*; H4=OTS-0010_20x20-v-slot-600mm.step; A5=4; B5=1; C5=*; D5=*; E5=*; F5=*; G5=*; H5=FDM-0006_x-motor-mount.FCStd; A6=5; B6=1; C6=*; D6=*; E6=*; F6=*; G6=*; H6=FDM-0013_x-idler-mount.FCStd; A7=6; B7=1; C7=*; D7=*; E7=*; F7=*; G7=*; H7=FDM-0010_y-gantry-umbilical-mount.FCStd; A8=7; B8=2; C8=*; D8=*; E8=*; F8=*; G8=*; H8=FDM-0008_y-gantry-support.FCStd; A9=8; B9=4; C9=*; D9=*; E9=*; F9=*; G9=*; H9=FDM-0009_roller-spacer.FCStd; A10=9; B10=9; C10=*; D10=*; E10=*; F10=*; G10=*; H10=OTS-0011_v-slot-roller.step; A11=10; B11=34; C11=*; D11=*; E11=*; F11=*; G11=*; H11=FST-0016_M5-tslot-nut.step; A12=11; B12=6; C12=*; D12=*; E12=*; F12=*; G12=*; H12=FDM-0027_belt-clamp.FCStd; A13=12; B13=3; C13=*; D13=*; E13=*; F13=*; G13=*; H13=FDM-0037_belt-tension-arm.FCStd; A14=13; B14=4; C14=*; D14=*; E14=*; F14=*; G14=*; H14=OTS-0012_nema17-stepper.step; A15=14; B15=4; C15=*; D15=*; E15=*; F15=*; G15=*; H15=OTS-0017_GT2-20-tooth-pulley.STEP; A16=15; B16=4; C16=*; D16=*; E16=*; F16=*; G16=*; H16=OTS-0016_GT2-20-tooth-idler.STEP; A17=16; B17=10; C17=*; D17=*; E17=*; F17=*; G17=*; H17=OTS-0005-00_zip-tie.FCStd; A18=17; B18=2; C18=*; D18=*; E18=*; F18=*; G18=*; H18=OTS-0002-00_usb-webcam.FCStd; A19=18; B19=1; C19=*; D19=*; E19=*; F19=*; G19=*; H19=FDM-0011_x-gantry-front.FCStd; A20=19; B20=1; C20=*; D20=*; E20=*; F20=*; G20=*; H20=FDM-0012_x-gantry-back.FCStd; A21=20; B21=1; C21=*; D21=*; E21=*; F21=*; G21=*; H21=FDM-0014_down-camera-mount.FCStd; A22=21; B22=1; C22=*; D22=*; E22=*; F22=*; G22=*; H22=FDM-0015_down-light-mount.FCStd; A23=22; B23=1; C23=*; D23=*; E23=*; F23=*; G23=*; H23=FDM-0040_z-gantry-backplate-left.FCStd; A24=23; B24=1; C24=*; D24=*; E24=*; F24=*; G24=*; H24=FDM-0017_z-gantry-left.FCStd; A25=24; B25=1; C25=*; D25=*; E25=*; F25=*; G25=*; H25=OTS-0001-00_CP40-nozzle-holder.FCStd; +264 more cells
